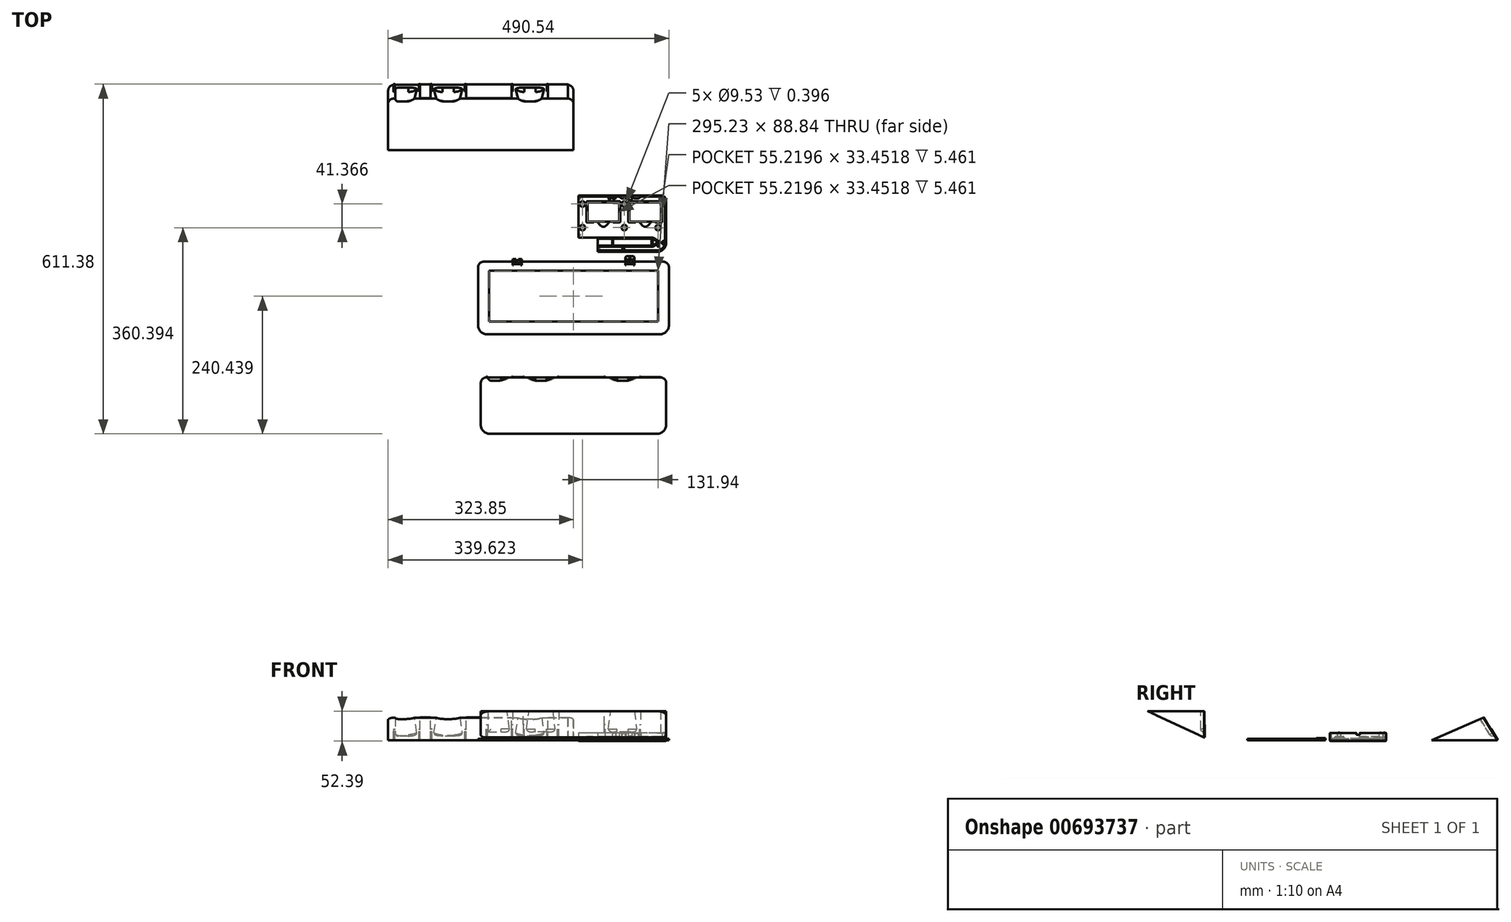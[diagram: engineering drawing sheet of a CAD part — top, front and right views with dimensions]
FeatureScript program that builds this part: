
annotation { "Feature Type Name" : "Feature", "Feature Type Description" : "" }
export const myFeature = defineFeature(function(context is Context, id is Id, definition is map)
    precondition{}
    {
        {
            var Q0;
            Q0=qCreatedBy(makeId("Top.planeOp"),FACE);
            var sketch = newSketch(context, id + "F0", { "sketchPlane" : qUnion([Q0])});
            skLineSegment(sketch, "E0.bottom", {"start": v(161.93, -49.21) * mm, "end": v(-161.93, -49.21) * mm});
            skLineSegment(sketch, "E0.top", {"start": v(161.93, 49.21) * mm, "end": v(-161.93, 49.21) * mm});
            skLineSegment(sketch, "E0.left", {"start": v(161.93, -49.21) * mm, "end": v(161.93, 49.21) * mm});
            skLineSegment(sketch, "E0.right", {"start": v(-161.93, -49.21) * mm, "end": v(-161.93, 49.21) * mm});
            skPoint(sketch, "E0.middle", {"position": v(0, 0) * mm});
            skSolve(sketch);
        }
        {
            var Q0;
            Q0=makeQuery(id+"F0.imprint","IMPRINT",FACE,{"disambiguationData":[TD([[makeQuery(id+"F0.imprint","IMPRINT",EDGE,{"derivedFrom":sQuery(id+"F0.wireOp",EDGE,"E0.bottom")}),-1.0]])]});
            extrude(context, id + "F1", {"entities" : qUnion([Q0]), "depth" : 3.17 * mm, "offsetDistance" : 25.4 * mm});
        }
        {
            var Q0;
            Q0=makeQuery(id+"F1.opExtrude","SWEPT_EDGE",EDGE,{"disambiguationData":[OSD([sQuery(id+"F0.wireOp",EDGE,"E0.bottom"),sQuery(id+"F0.wireOp",EDGE,"E0.right")])]});
            var Q1;
            Q1=makeQuery(id+"F1.opExtrude","SWEPT_EDGE",EDGE,{"disambiguationData":[OSD([sQuery(id+"F0.wireOp",EDGE,"E0.bottom"),sQuery(id+"F0.wireOp",EDGE,"E0.left")])]});
            fillet(context, id + "F2", {"entities" : qUnion([Q0, Q1]), "radius" : 15.88 * mm, "tangentPropagation" : true, "allowEdgeOverflow" : false});
        }
        {
            var Q0;
            Q0=makeQuery(id+"F1.opExtrude","SWEPT_EDGE",EDGE,{"disambiguationData":[OSD([sQuery(id+"F0.wireOp",EDGE,"E0.top"),sQuery(id+"F0.wireOp",EDGE,"E0.right")])]});
            var Q1;
            Q1=makeQuery(id+"F1.opExtrude","SWEPT_EDGE",EDGE,{"disambiguationData":[OSD([sQuery(id+"F0.wireOp",EDGE,"E0.top"),sQuery(id+"F0.wireOp",EDGE,"E0.left")])]});
            fillet(context, id + "F3", {"entities" : qUnion([Q0, Q1]), "radius" : 9.52 * mm, "tangentPropagation" : true, "allowEdgeOverflow" : false});
        }
        {
            var Q0;
            Q0=makeQuery(id+"F1.opExtrude","CAP_FACE",FACE,{"disambiguationData":[OSD([sQuery(id+"F0.wireOp",EDGE,"E0.bottom"),sQuery(id+"F0.wireOp",EDGE,"E0.top"),sQuery(id+"F0.wireOp",EDGE,"E0.left"),sQuery(id+"F0.wireOp",EDGE,"E0.right")])],"isStart":false});
            var sketch = newSketch(context, id + "F4", { "sketchPlane" : qUnion([Q0])});
            skArc(sketch, "E1.0", {"start": v(-152.4, 46.93) * mm, "mid": v(-157.52, 44.8) * mm, "end": v(-159.64, 39.69) * mm});
            skArc(sketch, "E2.0", {"start": v(-159.64, -33.34) * mm, "mid": v(-155.66, -42.95) * mm, "end": v(-146.05, -46.93) * mm});
            skLineSegment(sketch, "E3.0", {"start": v(-159.64, -33.34) * mm, "end": v(-159.64, 39.69) * mm});
            skArc(sketch, "E4.0", {"start": v(146.05, -46.93) * mm, "mid": v(155.66, -42.95) * mm, "end": v(159.64, -33.34) * mm});
            skArc(sketch, "E5.0", {"start": v(159.64, 39.69) * mm, "mid": v(157.52, 44.8) * mm, "end": v(152.4, 46.93) * mm});
            skLineSegment(sketch, "E6.0", {"start": v(159.64, -33.34) * mm, "end": v(159.64, 39.69) * mm});
            skLineSegment(sketch, "E7.0", {"start": v(152.4, 46.93) * mm, "end": v(-152.4, 46.93) * mm});
            skLineSegment(sketch, "E8.0", {"start": v(146.05, -46.93) * mm, "end": v(-146.05, -46.93) * mm});
            skSolve(sketch);
        }
        {
            var Q0;
            Q0=makeQuery(id+"F4.imprint","IMPRINT",FACE,{"disambiguationData":[TD([[makeQuery(id+"F4.imprint","IMPRINT",EDGE,{"derivedFrom":sQuery(id+"F4.wireOp",EDGE,"E1.0")}),-1.0]])]});
            extrude(context, id + "F5", {"entities" : qUnion([Q0]), "operationType" : NewBodyOperationType.ADD, "depth" : 9.52 * mm, "offsetDistance" : 25.4 * mm});
        }
        {
            var Q0;
            Q0=makeQuery(id+"F1.opExtrude","CAP_FACE",FACE,{"disambiguationData":[OSD([sQuery(id+"F0.wireOp",EDGE,"E0.bottom"),sQuery(id+"F0.wireOp",EDGE,"E0.top"),sQuery(id+"F0.wireOp",EDGE,"E0.left"),sQuery(id+"F0.wireOp",EDGE,"E0.right")])],"isStart":false});
            var sketch = newSketch(context, id + "F6", { "sketchPlane" : qUnion([Q0])});
            skCircle(sketch, "E9", {"center": v(-158.52, -33.34) * mm, "radius": 3.18 * mm});
            skLineSegment(sketch, "E10", {"start": v(-158.52, -33.34) * mm, "end": v(-158.52, 39.69) * mm, "construction": true});
            skCircle(sketch, "E11", {"center": v(-158.52, 39.69) * mm, "radius": 3.18 * mm});
            skCircle(sketch, "E12", {"center": v(158.23, 39.4) * mm, "radius": 3.18 * mm});
            skCircle(sketch, "E13", {"center": v(157.67, -33.34) * mm, "radius": 3.18 * mm});
            skCircle(sketch, "E14", {"center": v(70.74, 45.8) * mm, "radius": 3.18 * mm});
            skCircle(sketch, "E15", {"center": v(-2.29, 45.8) * mm, "radius": 3.29 * mm});
            skCircle(sketch, "E16", {"center": v(31.57, -45.8) * mm, "radius": 3.18 * mm});
            skCircle(sketch, "E17", {"center": v(-68.96, -45.8) * mm, "radius": 3.18 * mm});
            skSolve(sketch);
        }
        {
            var Q0;
            {var subQ0=sQuery(id+"F6.wireOp",EDGE,"E9");var subQ1=makeQuery(id+"F5.opExtrude","CAP_EDGE",EDGE,{"disambiguationData":[OSD([sQuery(id+"F4.wireOp",EDGE,"E2.0")])],"isStart":true});var subQ2=makeQuery(id+"F6.imprint","INTERSECT",VERTEX,{"derivedFrom":[subQ1,subQ0]});Q0=makeQuery(id+"F6.imprint","IMPRINT",FACE,{"disambiguationData":[TD([[makeQuery(id+"F6.imprint","IMPRINT",EDGE,{"disambiguationData":[TD([[subQ2,-1.0]])],"derivedFrom":subQ0}),1.0]])]});}
            var Q1;
            {var subQ0=sQuery(id+"F6.wireOp",EDGE,"E11");var subQ1=makeQuery(id+"F5.opExtrude","CAP_EDGE",EDGE,{"disambiguationData":[OSD([sQuery(id+"F4.wireOp",EDGE,"E1.0")])],"isStart":true});var subQ2=makeQuery(id+"F6.imprint","INTERSECT",VERTEX,{"derivedFrom":[subQ1,subQ0]});Q1=makeQuery(id+"F6.imprint","IMPRINT",FACE,{"disambiguationData":[TD([[makeQuery(id+"F6.imprint","IMPRINT",EDGE,{"disambiguationData":[TD([[subQ2,1.0]])],"derivedFrom":subQ0}),1.0]])]});}
            var Q2;
            {var subQ0=sQuery(id+"F6.wireOp",EDGE,"E15");var subQ1=makeQuery(id+"F5.opExtrude","CAP_EDGE",EDGE,{"disambiguationData":[OSD([sQuery(id+"F4.wireOp",EDGE,"E7.0")])],"isStart":true});var subQ2=makeQuery(id+"F6.imprint","INTERSECT",VERTEX,{"disambiguationData":[OD(0.0)],"derivedFrom":[subQ1,subQ0]});Q2=makeQuery(id+"F6.imprint","IMPRINT",FACE,{"disambiguationData":[TD([[makeQuery(id+"F6.imprint","IMPRINT",EDGE,{"disambiguationData":[TD([[subQ2,-1.0]])],"derivedFrom":subQ0}),1.0]])]});}
            var Q3;
            {var subQ0=sQuery(id+"F6.wireOp",EDGE,"E14");var subQ1=makeQuery(id+"F5.opExtrude","CAP_EDGE",EDGE,{"disambiguationData":[OSD([sQuery(id+"F4.wireOp",EDGE,"E7.0")])],"isStart":true});var subQ2=makeQuery(id+"F6.imprint","INTERSECT",VERTEX,{"disambiguationData":[OD(0.0)],"derivedFrom":[subQ1,subQ0]});Q3=makeQuery(id+"F6.imprint","IMPRINT",FACE,{"disambiguationData":[TD([[makeQuery(id+"F6.imprint","IMPRINT",EDGE,{"disambiguationData":[TD([[subQ2,1.0]])],"derivedFrom":subQ0}),1.0]])]});}
            var Q4;
            {var subQ0=sQuery(id+"F6.wireOp",EDGE,"E17");var subQ1=makeQuery(id+"F5.opExtrude","CAP_EDGE",EDGE,{"disambiguationData":[OSD([sQuery(id+"F4.wireOp",EDGE,"E8.0")])],"isStart":true});var subQ2=makeQuery(id+"F6.imprint","INTERSECT",VERTEX,{"disambiguationData":[OD(0.0)],"derivedFrom":[subQ1,subQ0]});Q4=makeQuery(id+"F6.imprint","IMPRINT",FACE,{"disambiguationData":[TD([[makeQuery(id+"F6.imprint","IMPRINT",EDGE,{"disambiguationData":[TD([[subQ2,1.0]])],"derivedFrom":subQ0}),1.0]])]});}
            var Q5;
            {var subQ0=sQuery(id+"F6.wireOp",EDGE,"E16");var subQ1=makeQuery(id+"F5.opExtrude","CAP_EDGE",EDGE,{"disambiguationData":[OSD([sQuery(id+"F4.wireOp",EDGE,"E8.0")])],"isStart":true});var subQ2=makeQuery(id+"F6.imprint","INTERSECT",VERTEX,{"disambiguationData":[OD(0.0)],"derivedFrom":[subQ1,subQ0]});Q5=makeQuery(id+"F6.imprint","IMPRINT",FACE,{"disambiguationData":[TD([[makeQuery(id+"F6.imprint","IMPRINT",EDGE,{"disambiguationData":[TD([[subQ2,-1.0]])],"derivedFrom":subQ0}),1.0]])]});}
            var Q6;
            {var subQ0=sQuery(id+"F6.wireOp",EDGE,"E13");var subQ1=makeQuery(id+"F5.opExtrude","CAP_EDGE",EDGE,{"disambiguationData":[OSD([sQuery(id+"F4.wireOp",EDGE,"E4.0")])],"isStart":true});var subQ2=makeQuery(id+"F6.imprint","INTERSECT",VERTEX,{"derivedFrom":[subQ1,subQ0]});Q6=makeQuery(id+"F6.imprint","IMPRINT",FACE,{"disambiguationData":[TD([[makeQuery(id+"F6.imprint","IMPRINT",EDGE,{"disambiguationData":[TD([[subQ2,1.0]])],"derivedFrom":subQ0}),1.0]])]});}
            var Q7;
            {var subQ0=sQuery(id+"F6.wireOp",EDGE,"E12");var subQ1=makeQuery(id+"F5.opExtrude","CAP_EDGE",EDGE,{"disambiguationData":[OSD([sQuery(id+"F4.wireOp",EDGE,"E5.0")])],"isStart":true});var subQ2=makeQuery(id+"F6.imprint","INTERSECT",VERTEX,{"derivedFrom":[subQ1,subQ0]});Q7=makeQuery(id+"F6.imprint","IMPRINT",FACE,{"disambiguationData":[TD([[makeQuery(id+"F6.imprint","IMPRINT",EDGE,{"disambiguationData":[TD([[subQ2,-1.0]])],"derivedFrom":subQ0}),1.0]])]});}
            extrude(context, id + "F7", {"entities" : qUnion([Q0, Q1, Q2, Q3, Q4, Q5, Q6, Q7]), "operationType" : NewBodyOperationType.ADD, "depth" : 9.52 * mm, "offsetDistance" : 25.4 * mm});
        }
        {
            var Q0;
            {var subQ0=sQuery(id+"F4.wireOp",EDGE,"E8.0");var subQ1=sQuery(id+"F4.wireOp",EDGE,"E7.0");var subQ2=sQuery(id+"F4.wireOp",EDGE,"E6.0");var subQ3=sQuery(id+"F4.wireOp",EDGE,"E4.0");var subQ4=sQuery(id+"F4.wireOp",EDGE,"E5.0");var subQ5=sQuery(id+"F4.wireOp",EDGE,"E3.0");var subQ6=sQuery(id+"F4.wireOp",EDGE,"E1.0");var subQ7=sQuery(id+"F4.wireOp",EDGE,"E2.0");Q0=makeQuery(id+"F7.boolean.opBoolean","MERGE",FACE,{"derivedFrom":[makeQuery(id+"F5.opExtrude","CAP_FACE",FACE,{"disambiguationData":[OSD([sQuery(id+"F0.wireOp",EDGE,"E0.bottom"),sQuery(id+"F0.wireOp",EDGE,"E0.top"),sQuery(id+"F0.wireOp",EDGE,"E0.left"),sQuery(id+"F0.wireOp",EDGE,"E0.right"),subQ6,subQ7,subQ5,subQ3,subQ4,subQ2,subQ1,subQ0])],"isStart":false}),makeQuery(id+"F7.opExtrude","CAP_FACE",FACE,{"disambiguationData":[OSD([subQ7,subQ5,sQuery(id+"F6.wireOp",EDGE,"E9")])],"isStart":false}),makeQuery(id+"F7.opExtrude","CAP_FACE",FACE,{"disambiguationData":[OSD([subQ6,subQ5,sQuery(id+"F6.wireOp",EDGE,"E11")])],"isStart":false}),makeQuery(id+"F7.opExtrude","CAP_FACE",FACE,{"disambiguationData":[OSD([subQ4,subQ2,sQuery(id+"F6.wireOp",EDGE,"E12")])],"isStart":false}),makeQuery(id+"F7.opExtrude","CAP_FACE",FACE,{"disambiguationData":[OSD([subQ3,subQ2,sQuery(id+"F6.wireOp",EDGE,"E13")])],"isStart":false}),makeQuery(id+"F7.opExtrude","CAP_FACE",FACE,{"disambiguationData":[OSD([subQ1,sQuery(id+"F6.wireOp",EDGE,"E14")])],"isStart":false}),makeQuery(id+"F7.opExtrude","CAP_FACE",FACE,{"disambiguationData":[OSD([subQ1,sQuery(id+"F6.wireOp",EDGE,"E15")])],"isStart":false}),makeQuery(id+"F7.opExtrude","CAP_FACE",FACE,{"disambiguationData":[OSD([subQ0,sQuery(id+"F6.wireOp",EDGE,"E16")])],"isStart":false}),makeQuery(id+"F7.opExtrude","CAP_FACE",FACE,{"disambiguationData":[OSD([subQ0,sQuery(id+"F6.wireOp",EDGE,"E17")])],"isStart":false})]});}
            var sketch = newSketch(context, id + "F8", { "sketchPlane" : qUnion([Q0])});
            skCircle(sketch, "E18", {"center": v(-2.29, 45.8) * mm, "radius": 1.03 * mm});
            skCircle(sketch, "E19", {"center": v(70.74, 45.8) * mm, "radius": 1.03 * mm});
            skCircle(sketch, "E20", {"center": v(158.23, 39.4) * mm, "radius": 1.03 * mm});
            skCircle(sketch, "E21", {"center": v(157.67, -33.34) * mm, "radius": 1.03 * mm});
            skCircle(sketch, "E22", {"center": v(31.57, -45.8) * mm, "radius": 1.03 * mm});
            skCircle(sketch, "E23", {"center": v(-68.96, -45.8) * mm, "radius": 1.03 * mm});
            skCircle(sketch, "E24", {"center": v(-158.52, -33.34) * mm, "radius": 1.03 * mm});
            skCircle(sketch, "E25", {"center": v(-158.52, 39.69) * mm, "radius": 1.03 * mm});
            skSolve(sketch);
        }
        {
            var Q0;
            Q0=makeQuery(id+"F8.imprint","IMPRINT",FACE,{"disambiguationData":[TD([[makeQuery(id+"F8.imprint","IMPRINT",EDGE,{"derivedFrom":sQuery(id+"F8.wireOp",EDGE,"E24")}),1.0]])]});
            var Q1;
            Q1=makeQuery(id+"F8.imprint","IMPRINT",FACE,{"disambiguationData":[TD([[makeQuery(id+"F8.imprint","IMPRINT",EDGE,{"derivedFrom":sQuery(id+"F8.wireOp",EDGE,"E23")}),1.0]])]});
            var Q2;
            Q2=makeQuery(id+"F8.imprint","IMPRINT",FACE,{"disambiguationData":[TD([[makeQuery(id+"F8.imprint","IMPRINT",EDGE,{"derivedFrom":sQuery(id+"F8.wireOp",EDGE,"E22")}),1.0]])]});
            var Q3;
            Q3=makeQuery(id+"F8.imprint","IMPRINT",FACE,{"disambiguationData":[TD([[makeQuery(id+"F8.imprint","IMPRINT",EDGE,{"derivedFrom":sQuery(id+"F8.wireOp",EDGE,"E21")}),1.0]])]});
            var Q4;
            Q4=makeQuery(id+"F8.imprint","IMPRINT",FACE,{"disambiguationData":[TD([[makeQuery(id+"F8.imprint","IMPRINT",EDGE,{"derivedFrom":sQuery(id+"F8.wireOp",EDGE,"E20")}),1.0]])]});
            var Q5;
            Q5=makeQuery(id+"F8.imprint","IMPRINT",FACE,{"disambiguationData":[TD([[makeQuery(id+"F8.imprint","IMPRINT",EDGE,{"derivedFrom":sQuery(id+"F8.wireOp",EDGE,"E19")}),1.0]])]});
            var Q6;
            Q6=makeQuery(id+"F8.imprint","IMPRINT",FACE,{"disambiguationData":[TD([[makeQuery(id+"F8.imprint","IMPRINT",EDGE,{"derivedFrom":sQuery(id+"F8.wireOp",EDGE,"E18")}),1.0]])]});
            var Q7;
            Q7=makeQuery(id+"F8.imprint","IMPRINT",FACE,{"disambiguationData":[TD([[makeQuery(id+"F8.imprint","IMPRINT",EDGE,{"derivedFrom":sQuery(id+"F8.wireOp",EDGE,"E25")}),1.0]])]});
            extrude(context, id + "F9", {"entities" : qUnion([Q0, Q1, Q2, Q3, Q4, Q5, Q6, Q7]), "operationType" : NewBodyOperationType.ADD, "depth" : 0.79 * mm, "offsetDistance" : 25.4 * mm});
        }
        {
            var Q0;
            Q0=makeQuery(id+"F1.opExtrude","CAP_FACE",FACE,{"disambiguationData":[OSD([sQuery(id+"F0.wireOp",EDGE,"E0.bottom"),sQuery(id+"F0.wireOp",EDGE,"E0.top"),sQuery(id+"F0.wireOp",EDGE,"E0.left"),sQuery(id+"F0.wireOp",EDGE,"E0.right")])],"isStart":false});
            var sketch = newSketch(context, id + "F10", { "sketchPlane" : qUnion([Q0])});
            skLineSegment(sketch, "E26", {"start": v(80.06, 46.93) * mm, "end": v(83.88, 43.75) * mm});
            skLineSegment(sketch, "E27", {"start": v(83.88, 43.75) * mm, "end": v(92.11, 43.75) * mm});
            skLineSegment(sketch, "E28", {"start": v(92.11, 43.75) * mm, "end": v(95.94, 46.93) * mm});
            skLineSegment(sketch, "E29", {"start": v(95.94, 46.93) * mm, "end": v(80.06, 46.93) * mm});
            skLineSegment(sketch, "E30", {"start": v(88, 46.93) * mm, "end": v(88, 43.23) * mm, "construction": true});
            skLineSegment(sketch, "E31", {"start": v(88, 43.75) * mm, "end": v(88, 44.46) * mm, "construction": true});
            skLineSegment(sketch, "E32", {"start": v(83.88, 45.62) * mm, "end": v(83.88, 43.16) * mm, "construction": true});
            skLineSegment(sketch, "E33", {"start": v(92.11, 45.79) * mm, "end": v(92.11, 43.52) * mm, "construction": true});
            skLineSegment(sketch, "E34", {"start": v(102.29, 46.93) * mm, "end": v(106.04, 43.75) * mm});
            skLineSegment(sketch, "E35", {"start": v(106.04, 43.75) * mm, "end": v(114.27, 43.75) * mm});
            skLineSegment(sketch, "E36", {"start": v(114.27, 43.75) * mm, "end": v(118.03, 46.93) * mm});
            skLineSegment(sketch, "E37", {"start": v(118.03, 46.93) * mm, "end": v(102.29, 46.93) * mm});
            skLineSegment(sketch, "E38", {"start": v(110.16, 46.93) * mm, "end": v(110.16, 43.75) * mm, "construction": true});
            skLineSegment(sketch, "E39", {"start": v(106.04, 45.04) * mm, "end": v(106.04, 42.78) * mm, "construction": true});
            skLineSegment(sketch, "E40", {"start": v(114.27, 44.82) * mm, "end": v(114.27, 43.03) * mm, "construction": true});
            skLineSegment(sketch, "E41", {"start": v(102.29, 47.44) * mm, "end": v(102.29, 46.4) * mm, "construction": true});
            skLineSegment(sketch, "E42", {"start": v(-67.48, 46.93) * mm, "end": v(-63.72, 43.75) * mm});
            skLineSegment(sketch, "E43", {"start": v(-63.72, 43.75) * mm, "end": v(-55.5, 43.75) * mm});
            skLineSegment(sketch, "E44", {"start": v(-55.5, 43.75) * mm, "end": v(-51.73, 46.93) * mm});
            skLineSegment(sketch, "E45", {"start": v(-51.73, 46.93) * mm, "end": v(-67.48, 46.93) * mm});
            skLineSegment(sketch, "E46", {"start": v(-59.6, 46.93) * mm, "end": v(-59.6, 41.87) * mm, "construction": true});
            skPoint(sketch, "E46.startSnap0", {"position": v(-59.6, 43.75) * mm});
            skLineSegment(sketch, "E47", {"start": v(-144.62, 46.93) * mm, "end": v(-140.86, 43.75) * mm});
            skLineSegment(sketch, "E48", {"start": v(-140.86, 43.75) * mm, "end": v(-132.63, 43.75) * mm});
            skLineSegment(sketch, "E49", {"start": v(-132.63, 43.75) * mm, "end": v(-128.87, 46.93) * mm});
            skLineSegment(sketch, "E50", {"start": v(-128.87, 46.93) * mm, "end": v(-144.62, 46.93) * mm});
            skLineSegment(sketch, "E51", {"start": v(-136.74, 46.93) * mm, "end": v(-136.74, 41.02) * mm, "construction": true});
            skSolve(sketch);
        }
        {
            var Q0;
            Q0=makeQuery(id+"F10.imprint","IMPRINT",FACE,{"disambiguationData":[TD([[makeQuery(id+"F10.imprint","IMPRINT",EDGE,{"derivedFrom":sQuery(id+"F10.wireOp",EDGE,"E47")}),1.0]])]});
            var Q1;
            Q1=makeQuery(id+"F10.imprint","IMPRINT",FACE,{"disambiguationData":[TD([[makeQuery(id+"F10.imprint","IMPRINT",EDGE,{"derivedFrom":sQuery(id+"F10.wireOp",EDGE,"E42")}),1.0]])]});
            var Q2;
            Q2=makeQuery(id+"F10.imprint","IMPRINT",FACE,{"disambiguationData":[TD([[makeQuery(id+"F10.imprint","IMPRINT",EDGE,{"derivedFrom":sQuery(id+"F10.wireOp",EDGE,"E26")}),1.0]])]});
            var Q3;
            Q3=makeQuery(id+"F10.imprint","IMPRINT",FACE,{"disambiguationData":[TD([[makeQuery(id+"F10.imprint","IMPRINT",EDGE,{"derivedFrom":sQuery(id+"F10.wireOp",EDGE,"E34")}),1.0]])]});
            extrude(context, id + "F11", {"entities" : qUnion([Q0, Q1, Q2, Q3]), "operationType" : NewBodyOperationType.ADD, "depth" : 9.52 * mm, "offsetDistance" : 25.4 * mm});
        }
        {
            var Q0;
            {var subQ0=sQuery(id+"F4.wireOp",EDGE,"E8.0");var subQ1=makeQuery(id+"F7.opExtrude","CAP_FACE",FACE,{"disambiguationData":[OSD([subQ0,sQuery(id+"F6.wireOp",EDGE,"E17")])],"isStart":false});var subQ2=makeQuery(id+"F7.opExtrude","CAP_FACE",FACE,{"disambiguationData":[OSD([subQ0,sQuery(id+"F6.wireOp",EDGE,"E16")])],"isStart":false});var subQ3=sQuery(id+"F4.wireOp",EDGE,"E7.0");var subQ4=makeQuery(id+"F7.opExtrude","CAP_FACE",FACE,{"disambiguationData":[OSD([subQ3,sQuery(id+"F6.wireOp",EDGE,"E15")])],"isStart":false});var subQ5=sQuery(id+"F6.wireOp",EDGE,"E14");var subQ6=makeQuery(id+"F7.opExtrude","CAP_FACE",FACE,{"disambiguationData":[OSD([subQ3,subQ5])],"isStart":false});var subQ7=sQuery(id+"F4.wireOp",EDGE,"E6.0");var subQ8=sQuery(id+"F4.wireOp",EDGE,"E4.0");var subQ9=makeQuery(id+"F7.opExtrude","CAP_FACE",FACE,{"disambiguationData":[OSD([subQ8,subQ7,sQuery(id+"F6.wireOp",EDGE,"E13")])],"isStart":false});var subQ11=sQuery(id+"F0.wireOp",EDGE,"E0.right");var subQ12=sQuery(id+"F0.wireOp",EDGE,"E0.left");var subQ13=sQuery(id+"F0.wireOp",EDGE,"E0.top");var subQ14=sQuery(id+"F0.wireOp",EDGE,"E0.bottom");var subQ15=makeQuery(id+"F1.opExtrude","CAP_FACE",FACE,{"disambiguationData":[OSD([subQ14,subQ13,subQ12,subQ11])],"isStart":false});var subQ16=sQuery(id+"F4.wireOp",EDGE,"E5.0");var subQ17=makeQuery(id+"F7.opExtrude","CAP_FACE",FACE,{"disambiguationData":[OSD([subQ16,subQ7,sQuery(id+"F6.wireOp",EDGE,"E12")])],"isStart":false});var subQ18=sQuery(id+"F4.wireOp",EDGE,"E3.0");var subQ19=sQuery(id+"F4.wireOp",EDGE,"E2.0");var subQ20=sQuery(id+"F4.wireOp",EDGE,"E1.0");var subQ21=makeQuery(id+"F5.opExtrude","CAP_FACE",FACE,{"disambiguationData":[OSD([subQ14,subQ13,subQ12,subQ11,subQ20,subQ19,subQ18,subQ8,subQ16,subQ7,subQ3,subQ0])],"isStart":false});var subQ22=makeQuery(id+"F7.opExtrude","CAP_FACE",FACE,{"disambiguationData":[OSD([subQ19,subQ18,sQuery(id+"F6.wireOp",EDGE,"E9")])],"isStart":false});var subQ23=makeQuery(id+"F7.opExtrude","CAP_FACE",FACE,{"disambiguationData":[OSD([subQ20,subQ18,sQuery(id+"F6.wireOp",EDGE,"E11")])],"isStart":false});var subQ24=sQuery(id+"F10.wireOp",EDGE,"E28");Q0=makeQuery(id+"F11.boolean.opBoolean","SPLIT",FACE,{"disambiguationData":[TD([makeQuery(id+"F11.opExtrude","SWEPT_FACE",FACE,{"disambiguationData":[OSD([subQ24])]})])],"derivedFrom":makeQuery(id+"F7.boolean.opBoolean","SPLIT",FACE,{"disambiguationData":[TD([subQ15,subQ21,makeQuery(id+"F5.opExtrude","SWEPT_FACE",FACE,{"disambiguationData":[OSD([subQ16])]}),subQ22,subQ23,subQ17,subQ9,makeQuery(id+"F7.opExtrude","SWEPT_FACE",FACE,{"disambiguationData":[OSD([subQ5])]}),subQ6,subQ4,subQ2,subQ1])],"derivedFrom":makeQuery(id+"F5.opExtrude","SWEPT_FACE",FACE,{"disambiguationData":[OSD([subQ3])]})})});}
            var sketch = newSketch(context, id + "F12", { "sketchPlane" : qUnion([Q0])});
            skCircle(sketch, "E52", {"center": v(-148.66, 3.04) * mm, "radius": 3.18 * mm});
            skCircle(sketch, "E53", {"center": v(99.9, 3.18) * mm, "radius": 3.18 * mm});
            skSolve(sketch);
        }
        {
            var Q0;
            Q0=makeQuery(id+"F12.imprint","IMPRINT",FACE,{"disambiguationData":[TD([[makeQuery(id+"F12.imprint","IMPRINT",EDGE,{"derivedFrom":sQuery(id+"F12.wireOp",EDGE,"E52")}),1.0]])]});
            extrude(context, id + "F13", {"entities" : qUnion([Q0]), "operationType" : NewBodyOperationType.ADD, "depth" : 6.35 * mm, "offsetDistance" : 25.4 * mm});
        }
        {
            var Q0;
            {var subQ0=sQuery(id+"F12.wireOp",EDGE,"E52");Q0=makeQuery(id+"F13.boolean.opBoolean","SPLIT",EDGE,{"disambiguationData":[TD([makeQuery(id+"F1.opExtrude","CAP_FACE",FACE,{"disambiguationData":[OSD([sQuery(id+"F0.wireOp",EDGE,"E0.bottom"),sQuery(id+"F0.wireOp",EDGE,"E0.top"),sQuery(id+"F0.wireOp",EDGE,"E0.left"),sQuery(id+"F0.wireOp",EDGE,"E0.right")])],"isStart":false})])],"derivedFrom":makeQuery(id+"F13.opExtrude","CAP_EDGE",EDGE,{"disambiguationData":[OSD([subQ0])],"isStart":false})});}
            fillet(context, id + "F14", {"entities" : qUnion([Q0]), "radius" : 2.54 * mm, "tangentPropagation" : true, "allowEdgeOverflow" : false});
        }
        {
            var Q0;
            {var subQ0=sQuery(id+"F4.wireOp",EDGE,"E8.0");var subQ1=makeQuery(id+"F7.opExtrude","CAP_FACE",FACE,{"disambiguationData":[OSD([subQ0,sQuery(id+"F6.wireOp",EDGE,"E17")])],"isStart":false});var subQ2=makeQuery(id+"F7.opExtrude","CAP_FACE",FACE,{"disambiguationData":[OSD([subQ0,sQuery(id+"F6.wireOp",EDGE,"E16")])],"isStart":false});var subQ3=sQuery(id+"F4.wireOp",EDGE,"E7.0");var subQ4=makeQuery(id+"F7.opExtrude","CAP_FACE",FACE,{"disambiguationData":[OSD([subQ3,sQuery(id+"F6.wireOp",EDGE,"E15")])],"isStart":false});var subQ5=sQuery(id+"F6.wireOp",EDGE,"E14");var subQ6=makeQuery(id+"F7.opExtrude","CAP_FACE",FACE,{"disambiguationData":[OSD([subQ3,subQ5])],"isStart":false});var subQ7=sQuery(id+"F4.wireOp",EDGE,"E6.0");var subQ8=sQuery(id+"F4.wireOp",EDGE,"E4.0");var subQ9=makeQuery(id+"F7.opExtrude","CAP_FACE",FACE,{"disambiguationData":[OSD([subQ8,subQ7,sQuery(id+"F6.wireOp",EDGE,"E13")])],"isStart":false});var subQ11=sQuery(id+"F0.wireOp",EDGE,"E0.right");var subQ12=sQuery(id+"F0.wireOp",EDGE,"E0.left");var subQ13=sQuery(id+"F0.wireOp",EDGE,"E0.top");var subQ14=sQuery(id+"F0.wireOp",EDGE,"E0.bottom");var subQ15=makeQuery(id+"F1.opExtrude","CAP_FACE",FACE,{"disambiguationData":[OSD([subQ14,subQ13,subQ12,subQ11])],"isStart":false});var subQ16=sQuery(id+"F4.wireOp",EDGE,"E5.0");var subQ17=makeQuery(id+"F7.opExtrude","CAP_FACE",FACE,{"disambiguationData":[OSD([subQ16,subQ7,sQuery(id+"F6.wireOp",EDGE,"E12")])],"isStart":false});var subQ18=sQuery(id+"F4.wireOp",EDGE,"E3.0");var subQ19=sQuery(id+"F4.wireOp",EDGE,"E2.0");var subQ20=sQuery(id+"F4.wireOp",EDGE,"E1.0");var subQ21=makeQuery(id+"F5.opExtrude","CAP_FACE",FACE,{"disambiguationData":[OSD([subQ14,subQ13,subQ12,subQ11,subQ20,subQ19,subQ18,subQ8,subQ16,subQ7,subQ3,subQ0])],"isStart":false});var subQ22=makeQuery(id+"F7.opExtrude","CAP_FACE",FACE,{"disambiguationData":[OSD([subQ19,subQ18,sQuery(id+"F6.wireOp",EDGE,"E9")])],"isStart":false});var subQ23=makeQuery(id+"F7.opExtrude","CAP_FACE",FACE,{"disambiguationData":[OSD([subQ20,subQ18,sQuery(id+"F6.wireOp",EDGE,"E11")])],"isStart":false});var subQ24=sQuery(id+"F10.wireOp",EDGE,"E28");Q0=makeQuery(id+"F11.boolean.opBoolean","SPLIT",FACE,{"disambiguationData":[TD([makeQuery(id+"F11.opExtrude","SWEPT_FACE",FACE,{"disambiguationData":[OSD([subQ24])]})])],"derivedFrom":makeQuery(id+"F7.boolean.opBoolean","SPLIT",FACE,{"disambiguationData":[TD([subQ15,subQ21,makeQuery(id+"F5.opExtrude","SWEPT_FACE",FACE,{"disambiguationData":[OSD([subQ16])]}),subQ22,subQ23,subQ17,subQ9,makeQuery(id+"F7.opExtrude","SWEPT_FACE",FACE,{"disambiguationData":[OSD([subQ5])]}),subQ6,subQ4,subQ2,subQ1])],"derivedFrom":makeQuery(id+"F5.opExtrude","SWEPT_FACE",FACE,{"disambiguationData":[OSD([subQ3])]})})});}
            var sketch = newSketch(context, id + "F15", { "sketchPlane" : qUnion([Q0])});
            skCircle(sketch, "E54", {"center": v(99.11, 3.18) * mm, "radius": 2.92 * mm});
            skSolve(sketch);
        }
        {
            var Q0;
            {var subQ0=sQuery(id+"F15.wireOp",EDGE,"E54");var subQ1=makeQuery(id+"F1.opExtrude","CAP_FACE",FACE,{"disambiguationData":[OSD([sQuery(id+"F0.wireOp",EDGE,"E0.bottom"),sQuery(id+"F0.wireOp",EDGE,"E0.top"),sQuery(id+"F0.wireOp",EDGE,"E0.left"),sQuery(id+"F0.wireOp",EDGE,"E0.right")])],"isStart":false});var subQ2=sQuery(id+"F4.wireOp",EDGE,"E7.0");var subQ3=makeQuery(id+"F5.opExtrude","SWEPT_FACE",FACE,{"disambiguationData":[OSD([subQ2])]});var subQ4=makeQuery(id+"F11.boolean.opBoolean","SPLIT",EDGE,{"disambiguationData":[TD([makeQuery(id+"F11.opExtrude","SWEPT_FACE",FACE,{"disambiguationData":[OSD([sQuery(id+"F10.wireOp",EDGE,"E28")])]})])],"derivedFrom":makeQuery(id+"F7.boolean.opBoolean","SPLIT",EDGE,{"disambiguationData":[TD([subQ1,makeQuery(id+"F5.opExtrude","SWEPT_FACE",FACE,{"disambiguationData":[OSD([sQuery(id+"F4.wireOp",EDGE,"E5.0")])]}),subQ3,makeQuery(id+"F7.opExtrude","SWEPT_FACE",FACE,{"disambiguationData":[OSD([sQuery(id+"F6.wireOp",EDGE,"E14")])]})])],"derivedFrom":makeQuery(id+"F5.opExtrude","CAP_EDGE",EDGE,{"disambiguationData":[OSD([subQ2])],"isStart":true})})});var subQ5=makeQuery(id+"F15.imprint","INTERSECT",VERTEX,{"disambiguationData":[OD(0.0)],"derivedFrom":[subQ4,subQ0]});Q0=makeQuery(id+"F15.imprint","IMPRINT",FACE,{"disambiguationData":[TD([[makeQuery(id+"F15.imprint","IMPRINT",EDGE,{"disambiguationData":[TD([[subQ5,1.0]])],"derivedFrom":subQ0}),1.0]])]});}
            var Q1;
            Q1=sQuery(id+"F15.wireOp",EDGE,"E54");
            extrude(context, id + "F16", {"entities" : qUnion([Q0]), "operationType" : NewBodyOperationType.ADD, "surfaceEntities" : qUnion([Q1]), "depth" : 6.35 * mm, "offsetDistance" : 25.4 * mm});
        }
        {
            var Q0;
            Q0=makeQuery(id+"F16.opExtrude","CAP_EDGE",EDGE,{"disambiguationData":[OSD([sQuery(id+"F15.wireOp",EDGE,"E54")])],"isStart":false});
            fillet(context, id + "F17", {"entities" : qUnion([Q0]), "radius" : 2.54 * mm, "tangentPropagation" : true, "allowEdgeOverflow" : false});
        }
        {
            var Q0;
            {var subQ0=sQuery(id+"F4.wireOp",EDGE,"E8.0");var subQ1=makeQuery(id+"F7.opExtrude","CAP_FACE",FACE,{"disambiguationData":[OSD([subQ0,sQuery(id+"F6.wireOp",EDGE,"E16")])],"isStart":false});var subQ2=sQuery(id+"F6.wireOp",EDGE,"E15");var subQ3=sQuery(id+"F4.wireOp",EDGE,"E7.0");var subQ4=makeQuery(id+"F7.opExtrude","CAP_FACE",FACE,{"disambiguationData":[OSD([subQ3,subQ2])],"isStart":false});var subQ6=makeQuery(id+"F7.opExtrude","SWEPT_FACE",FACE,{"disambiguationData":[OSD([subQ2])]});var subQ7=makeQuery(id+"F7.opExtrude","CAP_FACE",FACE,{"disambiguationData":[OSD([subQ3,sQuery(id+"F6.wireOp",EDGE,"E14")])],"isStart":false});var subQ8=sQuery(id+"F4.wireOp",EDGE,"E6.0");var subQ9=sQuery(id+"F4.wireOp",EDGE,"E4.0");var subQ10=makeQuery(id+"F7.opExtrude","CAP_FACE",FACE,{"disambiguationData":[OSD([subQ9,subQ8,sQuery(id+"F6.wireOp",EDGE,"E13")])],"isStart":false});var subQ11=sQuery(id+"F0.wireOp",EDGE,"E0.right");var subQ12=sQuery(id+"F0.wireOp",EDGE,"E0.left");var subQ13=sQuery(id+"F0.wireOp",EDGE,"E0.top");var subQ14=sQuery(id+"F0.wireOp",EDGE,"E0.bottom");var subQ15=makeQuery(id+"F1.opExtrude","CAP_FACE",FACE,{"disambiguationData":[OSD([subQ14,subQ13,subQ12,subQ11])],"isStart":false});var subQ16=sQuery(id+"F4.wireOp",EDGE,"E5.0");var subQ17=makeQuery(id+"F7.opExtrude","CAP_FACE",FACE,{"disambiguationData":[OSD([subQ16,subQ8,sQuery(id+"F6.wireOp",EDGE,"E12")])],"isStart":false});var subQ18=sQuery(id+"F4.wireOp",EDGE,"E3.0");var subQ19=sQuery(id+"F4.wireOp",EDGE,"E2.0");var subQ20=sQuery(id+"F4.wireOp",EDGE,"E1.0");var subQ21=makeQuery(id+"F5.opExtrude","CAP_FACE",FACE,{"disambiguationData":[OSD([subQ14,subQ13,subQ12,subQ11,subQ20,subQ19,subQ18,subQ9,subQ16,subQ8,subQ3,subQ0])],"isStart":false});var subQ22=makeQuery(id+"F7.opExtrude","CAP_FACE",FACE,{"disambiguationData":[OSD([subQ19,subQ18,sQuery(id+"F6.wireOp",EDGE,"E9")])],"isStart":false});var subQ23=makeQuery(id+"F7.opExtrude","CAP_FACE",FACE,{"disambiguationData":[OSD([subQ20,subQ18,sQuery(id+"F6.wireOp",EDGE,"E11")])],"isStart":false});var subQ24=makeQuery(id+"F7.opExtrude","CAP_FACE",FACE,{"disambiguationData":[OSD([subQ0,sQuery(id+"F6.wireOp",EDGE,"E17")])],"isStart":false});Q0=makeQuery(id+"F11.boolean.opBoolean","SPLIT",FACE,{"disambiguationData":[TD([subQ6])],"derivedFrom":makeQuery(id+"F7.boolean.opBoolean","SPLIT",FACE,{"disambiguationData":[TD([subQ15,makeQuery(id+"F5.opExtrude","SWEPT_FACE",FACE,{"disambiguationData":[OSD([subQ20])]}),subQ21,subQ22,subQ23,subQ17,subQ10,subQ7,subQ6,subQ4,subQ1,subQ24])],"derivedFrom":makeQuery(id+"F5.opExtrude","SWEPT_FACE",FACE,{"disambiguationData":[OSD([subQ3])]})})});}
            var sketch = newSketch(context, id + "F18", { "sketchPlane" : qUnion([Q0])});
            skCircle(sketch, "E55", {"center": v(-47.86, 3.18) * mm, "radius": 3.18 * mm});
            skSolve(sketch);
        }
        {
            var Q0;
            {var subQ0=sQuery(id+"F18.wireOp",EDGE,"E55");var subQ1=makeQuery(id+"F1.opExtrude","CAP_FACE",FACE,{"disambiguationData":[OSD([sQuery(id+"F0.wireOp",EDGE,"E0.bottom"),sQuery(id+"F0.wireOp",EDGE,"E0.top"),sQuery(id+"F0.wireOp",EDGE,"E0.left"),sQuery(id+"F0.wireOp",EDGE,"E0.right")])],"isStart":false});var subQ2=sQuery(id+"F4.wireOp",EDGE,"E7.0");var subQ3=makeQuery(id+"F5.opExtrude","SWEPT_FACE",FACE,{"disambiguationData":[OSD([subQ2])]});var subQ4=makeQuery(id+"F7.opExtrude","SWEPT_FACE",FACE,{"disambiguationData":[OSD([sQuery(id+"F6.wireOp",EDGE,"E15")])]});var subQ5=makeQuery(id+"F11.boolean.opBoolean","SPLIT",EDGE,{"disambiguationData":[TD([subQ4])],"derivedFrom":makeQuery(id+"F7.boolean.opBoolean","SPLIT",EDGE,{"disambiguationData":[TD([subQ1,makeQuery(id+"F5.opExtrude","SWEPT_FACE",FACE,{"disambiguationData":[OSD([sQuery(id+"F4.wireOp",EDGE,"E1.0")])]}),subQ3,subQ4])],"derivedFrom":makeQuery(id+"F5.opExtrude","CAP_EDGE",EDGE,{"disambiguationData":[OSD([subQ2])],"isStart":true})})});var subQ6=makeQuery(id+"F18.imprint","INTERSECT",VERTEX,{"disambiguationData":[OD(0.0)],"derivedFrom":[subQ5,subQ0]});Q0=makeQuery(id+"F18.imprint","IMPRINT",FACE,{"disambiguationData":[TD([[makeQuery(id+"F18.imprint","IMPRINT",EDGE,{"disambiguationData":[TD([[subQ6,-1.0]])],"derivedFrom":subQ0}),1.0]])]});}
            extrude(context, id + "F19", {"entities" : qUnion([Q0]), "operationType" : NewBodyOperationType.ADD, "depth" : 6.35 * mm, "offsetDistance" : 25.4 * mm});
        }
        {
            var Q0;
            Q0=makeQuery(id+"F19.opExtrude","CAP_EDGE",EDGE,{"disambiguationData":[OSD([sQuery(id+"F18.wireOp",EDGE,"E55")])],"isStart":false});
            fillet(context, id + "F20", {"entities" : qUnion([Q0]), "radius" : 2.54 * mm, "tangentPropagation" : true, "allowEdgeOverflow" : false});
        }
        {
            var Q0;
            Q0=makeQuery(id+"F1.opExtrude","CAP_FACE",FACE,{"disambiguationData":[OSD([sQuery(id+"F0.wireOp",EDGE,"E0.bottom"),sQuery(id+"F0.wireOp",EDGE,"E0.top"),sQuery(id+"F0.wireOp",EDGE,"E0.left"),sQuery(id+"F0.wireOp",EDGE,"E0.right")])],"isStart":false});
            var sketch = newSketch(context, id + "F21", { "sketchPlane" : qUnion([Q0])});
            skLineSegment(sketch, "E56.bottom", {"start": v(154.86, 38.99) * mm, "end": v(95.94, 38.99) * mm});
            skLineSegment(sketch, "E56.top", {"start": v(154.86, 1.83) * mm, "end": v(95.94, 1.83) * mm});
            skLineSegment(sketch, "E56.left", {"start": v(154.86, 38.99) * mm, "end": v(154.86, 1.83) * mm});
            skLineSegment(sketch, "E56.right", {"start": v(95.94, 38.99) * mm, "end": v(95.94, 1.83) * mm});
            skPoint(sketch, "E57.MirrorCS.start.orphan", {"position": v(95.94, 38.99) * mm});
            skPoint(sketch, "E58.MirrorCS.start.orphan", {"position": v(154.86, 38.99) * mm});
            skSolve(sketch);
        }
        {
            var Q0;
            Q0=makeQuery(id+"F21.imprint","IMPRINT",FACE,{"disambiguationData":[TD([[makeQuery(id+"F21.imprint","IMPRINT",EDGE,{"derivedFrom":sQuery(id+"F21.wireOp",EDGE,"E56.bottom")}),1.0]])]});
            extrude(context, id + "F22", {"entities" : qUnion([Q0]), "operationType" : NewBodyOperationType.ADD, "depth" : 2.83 * mm, "offsetDistance" : 25.4 * mm});
        }
        {
            var Q0;
            Q0=makeQuery(id+"F22.opExtrude","SWEPT_EDGE",EDGE,{"disambiguationData":[OSD([sQuery(id+"F21.wireOp",EDGE,"E56.top"),sQuery(id+"F21.wireOp",EDGE,"E56.right")])]});
            var Q1;
            Q1=makeQuery(id+"F22.opExtrude","SWEPT_EDGE",EDGE,{"disambiguationData":[OSD([sQuery(id+"F21.wireOp",EDGE,"E56.bottom"),sQuery(id+"F21.wireOp",EDGE,"E56.right")])]});
            var Q2;
            Q2=makeQuery(id+"F22.opExtrude","SWEPT_EDGE",EDGE,{"disambiguationData":[OSD([sQuery(id+"F21.wireOp",EDGE,"E56.bottom"),sQuery(id+"F21.wireOp",EDGE,"E56.left")])]});
            var Q3;
            Q3=makeQuery(id+"F22.opExtrude","SWEPT_EDGE",EDGE,{"disambiguationData":[OSD([sQuery(id+"F21.wireOp",EDGE,"E56.top"),sQuery(id+"F21.wireOp",EDGE,"E56.left")])]});
            fillet(context, id + "F23", {"entities" : qUnion([Q0, Q1, Q2, Q3]), "radius" : 1.27 * mm, "tangentPropagation" : true, "allowEdgeOverflow" : false});
        }
        {
            var Q0;
            Q0=makeQuery(id+"F22.opExtrude","CAP_FACE",FACE,{"disambiguationData":[OSD([sQuery(id+"F21.wireOp",EDGE,"E56.bottom"),sQuery(id+"F21.wireOp",EDGE,"E56.top"),sQuery(id+"F21.wireOp",EDGE,"E56.left"),sQuery(id+"F21.wireOp",EDGE,"E56.right")])],"isStart":false});
            var sketch = newSketch(context, id + "F24", { "sketchPlane" : qUnion([Q0])});
            skLineSegment(sketch, "E59.0", {"start": v(97.79, 3.68) * mm, "end": v(153, 3.68) * mm});
            skLineSegment(sketch, "E59.1", {"start": v(97.79, 37.13) * mm, "end": v(97.79, 3.68) * mm});
            skLineSegment(sketch, "E59.2", {"start": v(153, 37.13) * mm, "end": v(97.79, 37.13) * mm});
            skLineSegment(sketch, "E59.3", {"start": v(153, 3.68) * mm, "end": v(153, 37.13) * mm});
            skSolve(sketch);
        }
        {
            var Q0;
            Q0=makeQuery(id+"F24.imprint","IMPRINT",FACE,{"disambiguationData":[TD([[makeQuery(id+"F24.imprint","IMPRINT",EDGE,{"derivedFrom":sQuery(id+"F24.wireOp",EDGE,"E59.0")}),1.0]])]});
            extrude(context, id + "F25", {"entities" : qUnion([Q0]), "operationType" : NewBodyOperationType.REMOVE, "oppositeDirection" : true, "depth" : 5.7 * mm, "offsetDistance" : 25.4 * mm});
        }
        {
            var Q0;
            Q0=makeQuery(id+"F1.opExtrude","CAP_FACE",FACE,{"disambiguationData":[OSD([sQuery(id+"F0.wireOp",EDGE,"E0.bottom"),sQuery(id+"F0.wireOp",EDGE,"E0.top"),sQuery(id+"F0.wireOp",EDGE,"E0.left"),sQuery(id+"F0.wireOp",EDGE,"E0.right")])],"isStart":false});
            var sketch = newSketch(context, id + "F26", { "sketchPlane" : qUnion([Q0])});
            skLineSegment(sketch, "E60.bottom", {"start": v(81.65, 38.98) * mm, "end": v(22.72, 38.98) * mm});
            skLineSegment(sketch, "E60.top", {"start": v(81.65, 1.82) * mm, "end": v(22.72, 1.82) * mm});
            skLineSegment(sketch, "E60.left", {"start": v(81.65, 38.98) * mm, "end": v(81.65, 1.82) * mm});
            skLineSegment(sketch, "E60.right", {"start": v(22.72, 38.98) * mm, "end": v(22.72, 1.82) * mm});
            skSolve(sketch);
        }
        {
            var Q0;
            Q0=makeQuery(id+"F26.imprint","IMPRINT",FACE,{"disambiguationData":[TD([[makeQuery(id+"F26.imprint","IMPRINT",EDGE,{"derivedFrom":sQuery(id+"F26.wireOp",EDGE,"E60.bottom")}),1.0]])]});
            extrude(context, id + "F27", {"entities" : qUnion([Q0]), "operationType" : NewBodyOperationType.ADD, "depth" : 2.84 * mm, "offsetDistance" : 25.4 * mm});
        }
        {
            var Q0;
            Q0=makeQuery(id+"F27.opExtrude","SWEPT_EDGE",EDGE,{"disambiguationData":[OSD([sQuery(id+"F26.wireOp",EDGE,"E60.top"),sQuery(id+"F26.wireOp",EDGE,"E60.right")])]});
            var Q1;
            Q1=makeQuery(id+"F27.opExtrude","SWEPT_EDGE",EDGE,{"disambiguationData":[OSD([sQuery(id+"F26.wireOp",EDGE,"E60.top"),sQuery(id+"F26.wireOp",EDGE,"E60.left")])]});
            var Q2;
            Q2=makeQuery(id+"F27.opExtrude","SWEPT_EDGE",EDGE,{"disambiguationData":[OSD([sQuery(id+"F26.wireOp",EDGE,"E60.bottom"),sQuery(id+"F26.wireOp",EDGE,"E60.left")])]});
            var Q3;
            Q3=makeQuery(id+"F27.opExtrude","SWEPT_EDGE",EDGE,{"disambiguationData":[OSD([sQuery(id+"F26.wireOp",EDGE,"E60.bottom"),sQuery(id+"F26.wireOp",EDGE,"E60.right")])]});
            fillet(context, id + "F28", {"entities" : qUnion([Q0, Q1, Q2, Q3]), "radius" : 1.27 * mm, "tangentPropagation" : true, "allowEdgeOverflow" : false});
        }
        {
            var Q0;
            Q0=makeQuery(id+"F27.opExtrude","CAP_FACE",FACE,{"disambiguationData":[OSD([sQuery(id+"F26.wireOp",EDGE,"E60.bottom"),sQuery(id+"F26.wireOp",EDGE,"E60.top"),sQuery(id+"F26.wireOp",EDGE,"E60.left"),sQuery(id+"F26.wireOp",EDGE,"E60.right")])],"isStart":false});
            var sketch = newSketch(context, id + "F29", { "sketchPlane" : qUnion([Q0])});
            skLineSegment(sketch, "E61.0", {"start": v(24.57, 3.67) * mm, "end": v(79.8, 3.67) * mm});
            skLineSegment(sketch, "E61.1", {"start": v(24.57, 37.12) * mm, "end": v(24.57, 3.67) * mm});
            skLineSegment(sketch, "E61.2", {"start": v(79.8, 37.12) * mm, "end": v(24.57, 37.12) * mm});
            skLineSegment(sketch, "E61.3", {"start": v(79.8, 3.67) * mm, "end": v(79.8, 37.12) * mm});
            skSolve(sketch);
        }
        {
            var Q0;
            Q0=makeQuery(id+"F29.imprint","IMPRINT",FACE,{"disambiguationData":[TD([[makeQuery(id+"F29.imprint","IMPRINT",EDGE,{"derivedFrom":sQuery(id+"F29.wireOp",EDGE,"E61.0")}),1.0]])]});
            extrude(context, id + "F30", {"entities" : qUnion([Q0]), "operationType" : NewBodyOperationType.REMOVE, "oppositeDirection" : true, "depth" : 5.7 * mm, "offsetDistance" : 25.4 * mm});
        }
        {
            var Q0;
            Q0=makeQuery(id+"F22.opExtrude","SWEPT_FACE",FACE,{"disambiguationData":[OSD([sQuery(id+"F21.wireOp",EDGE,"E56.top")])]});
            var sketch = newSketch(context, id + "F31", { "sketchPlane" : qUnion([Q0])});
            skLineSegment(sketch, "E62.bottom", {"start": v(103.17, 3.18) * mm, "end": v(147.62, 3.18) * mm});
            skLineSegment(sketch, "E62.top", {"start": v(103.17, 17.48) * mm, "end": v(147.62, 17.48) * mm});
            skLineSegment(sketch, "E62.left", {"start": v(103.17, 3.17) * mm, "end": v(103.17, 17.48) * mm});
            skLineSegment(sketch, "E62.right", {"start": v(147.62, 3.18) * mm, "end": v(147.62, 17.48) * mm});
            skLineSegment(sketch, "E63", {"start": v(125.4, 6) * mm, "end": v(124.34, 16.54) * mm, "construction": true});
            skLineSegment(sketch, "E64", {"start": v(125.4, 17.48) * mm, "end": v(125.4, 3.18) * mm, "construction": true});
            skSolve(sketch);
        }
        {
            var Q0;
            Q0=makeQuery(id+"F27.opExtrude","SWEPT_FACE",FACE,{"disambiguationData":[OSD([sQuery(id+"F26.wireOp",EDGE,"E60.top")])]});
            var sketch = newSketch(context, id + "F32", { "sketchPlane" : qUnion([Q0])});
            skLineSegment(sketch, "E65.bottom", {"start": v(29.96, 3.18) * mm, "end": v(74.4, 3.18) * mm});
            skLineSegment(sketch, "E65.top", {"start": v(29.96, 17.48) * mm, "end": v(74.4, 17.48) * mm});
            skLineSegment(sketch, "E65.left", {"start": v(29.96, 3.17) * mm, "end": v(29.96, 17.48) * mm});
            skLineSegment(sketch, "E65.right", {"start": v(74.4, 3.18) * mm, "end": v(74.4, 17.48) * mm});
            skPoint(sketch, "E66.orphan", {"position": v(52.18, 17.48) * mm});
            skPoint(sketch, "E67.start.orphan", {"position": v(52.18, 3.18) * mm});
            skSolve(sketch);
        }
        {
            var Q0;
            {var subQ0=sQuery(id+"F31.wireOp",EDGE,"E62.top");Q0=makeQuery(id+"F31.imprint","IMPRINT",FACE,{"disambiguationData":[TD([[makeQuery(id+"F31.imprint","IMPRINT",EDGE,{"derivedFrom":subQ0}),-1.0]])]});}
            var Q1;
            {var subQ0=sQuery(id+"F32.wireOp",EDGE,"E65.top");Q1=makeQuery(id+"F32.imprint","IMPRINT",FACE,{"disambiguationData":[TD([[makeQuery(id+"F32.imprint","IMPRINT",EDGE,{"derivedFrom":subQ0}),-1.0]])]});}
            extrude(context, id + "F33", {"entities" : qUnion([Q0, Q1]), "operationType" : NewBodyOperationType.ADD, "oppositeDirection" : true, "depth" : 2.3 * mm, "offsetDistance" : 25.4 * mm});
        }
        {
            var Q0;
            {var subQ0=sQuery(id+"F21.wireOp",EDGE,"E56.top");Q0=makeQuery(id+"F33.boolean.opBoolean","MERGE",FACE,{"derivedFrom":[makeQuery(id+"F22.opExtrude","SWEPT_FACE",FACE,{"disambiguationData":[OSD([subQ0])]}),makeQuery(id+"F33.opExtrude","CAP_FACE",FACE,{"disambiguationData":[OSD([subQ0,sQuery(id+"F31.wireOp",EDGE,"E62.top"),sQuery(id+"F31.wireOp",EDGE,"E62.left"),sQuery(id+"F31.wireOp",EDGE,"E62.right")])],"isStart":true})]});}
            var sketch = newSketch(context, id + "F34", { "sketchPlane" : qUnion([Q0])});
            skArc(sketch, "E68", {"start": v(103.17, 6) * mm, "mid": v(105.54, 3.9) * mm, "end": v(108.64, 3.17) * mm});
            skArc(sketch, "E69", {"start": v(142.16, 3.18) * mm, "mid": v(145.26, 3.9) * mm, "end": v(147.62, 6) * mm});
            skLineSegment(sketch, "E70", {"start": v(108.64, 3.17) * mm, "end": v(142.16, 3.18) * mm});
            skLineSegment(sketch, "E71", {"start": v(147.62, 6) * mm, "end": v(147.62, 17.48) * mm});
            skLineSegment(sketch, "E72", {"start": v(147.62, 17.48) * mm, "end": v(103.17, 17.48) * mm});
            skLineSegment(sketch, "E73", {"start": v(103.17, 17.48) * mm, "end": v(103.17, 6) * mm});
            skSolve(sketch);
        }
        {
            var Q0;
            {var subQ0=sQuery(id+"F26.wireOp",EDGE,"E60.top");Q0=makeQuery(id+"F33.boolean.opBoolean","MERGE",FACE,{"derivedFrom":[makeQuery(id+"F27.opExtrude","SWEPT_FACE",FACE,{"disambiguationData":[OSD([subQ0])]}),makeQuery(id+"F33.opExtrude","CAP_FACE",FACE,{"disambiguationData":[OSD([subQ0,sQuery(id+"F32.wireOp",EDGE,"E65.top"),sQuery(id+"F32.wireOp",EDGE,"E65.left"),sQuery(id+"F32.wireOp",EDGE,"E65.right")])],"isStart":true})]});}
            var sketch = newSketch(context, id + "F35", { "sketchPlane" : qUnion([Q0])});
            skPoint(sketch, "E74.end.orphan", {"position": v(35.42, 3.18) * mm});
            skArc(sketch, "E75", {"start": v(29.96, 6.02) * mm, "mid": v(32.33, 3.9) * mm, "end": v(35.42, 3.17) * mm});
            skPoint(sketch, "E76.start.orphan", {"position": v(68.95, 3.18) * mm});
            skArc(sketch, "E77", {"start": v(68.95, 3.18) * mm, "mid": v(72.04, 3.9) * mm, "end": v(74.4, 6.02) * mm});
            skLineSegment(sketch, "E78", {"start": v(35.42, 3.18) * mm, "end": v(68.95, 3.18) * mm});
            skLineSegment(sketch, "E79", {"start": v(74.4, 6.02) * mm, "end": v(74.4, 17.48) * mm});
            skLineSegment(sketch, "E80", {"start": v(74.4, 17.48) * mm, "end": v(29.96, 17.48) * mm});
            skLineSegment(sketch, "E81", {"start": v(29.96, 17.48) * mm, "end": v(29.96, 6.02) * mm});
            skSolve(sketch);
        }
        {
            var Q0;
            {var subQ0=sQuery(id+"F35.wireOp",EDGE,"E78");Q0=makeQuery(id+"F35.imprint","IMPRINT",FACE,{"disambiguationData":[TD([[makeQuery(id+"F35.imprint","IMPRINT",EDGE,{"derivedFrom":subQ0}),-1.0]])]});}
            extrude(context, id + "F36", {"entities" : qUnion([Q0]), "operationType" : NewBodyOperationType.REMOVE, "oppositeDirection" : true, "depth" : 2.54 * mm, "offsetDistance" : 25.4 * mm});
        }
        {
            var Q0;
            {var subQ0=sQuery(id+"F34.wireOp",EDGE,"E70");Q0=makeQuery(id+"F34.imprint","IMPRINT",FACE,{"disambiguationData":[TD([[makeQuery(id+"F34.imprint","IMPRINT",EDGE,{"derivedFrom":subQ0}),-1.0]])]});}
            extrude(context, id + "F37", {"entities" : qUnion([Q0]), "operationType" : NewBodyOperationType.REMOVE, "oppositeDirection" : true, "depth" : 2.54 * mm, "offsetDistance" : 25.4 * mm});
        }
        {
            var Q0;
            Q0=makeQuery(id+"F37.boolean.opBoolean","MERGE",FACE,{"derivedFrom":[makeQuery(id+"F36.boolean.opBoolean","MERGE",FACE,{"derivedFrom":[makeQuery(id+"F1.opExtrude","CAP_FACE",FACE,{"disambiguationData":[OSD([sQuery(id+"F0.wireOp",EDGE,"E0.bottom"),sQuery(id+"F0.wireOp",EDGE,"E0.top"),sQuery(id+"F0.wireOp",EDGE,"E0.left"),sQuery(id+"F0.wireOp",EDGE,"E0.right")])],"isStart":false}),makeQuery(id+"F36.opExtrude","SWEPT_FACE",FACE,{"disambiguationData":[OSD([sQuery(id+"F26.wireOp",EDGE,"E60.top"),sQuery(id+"F35.wireOp",EDGE,"E78")])]})]}),makeQuery(id+"F37.opExtrude","SWEPT_FACE",FACE,{"disambiguationData":[OSD([sQuery(id+"F21.wireOp",EDGE,"E56.top"),sQuery(id+"F34.wireOp",EDGE,"E70")])]})]});
            var sketch = newSketch(context, id + "F38", { "sketchPlane" : qUnion([Q0])});
            skLineSegment(sketch, "E82.bottom", {"start": v(8.62, 38.98) * mm, "end": v(-50.44, 38.98) * mm});
            skLineSegment(sketch, "E82.top", {"start": v(8.62, -16.01) * mm, "end": v(-50.44, -16.01) * mm});
            skLineSegment(sketch, "E82.left", {"start": v(8.62, 38.98) * mm, "end": v(8.62, -16.01) * mm});
            skLineSegment(sketch, "E82.right", {"start": v(-50.44, 38.98) * mm, "end": v(-50.44, -16.01) * mm});
            skSolve(sketch);
        }
        {
            var Q0;
            Q0=makeQuery(id+"F38.imprint","IMPRINT",FACE,{"disambiguationData":[TD([[makeQuery(id+"F38.imprint","IMPRINT",EDGE,{"derivedFrom":sQuery(id+"F38.wireOp",EDGE,"E82.bottom")}),1.0]])]});
            extrude(context, id + "F39", {"entities" : qUnion([Q0]), "operationType" : NewBodyOperationType.ADD, "depth" : 2.84 * mm, "offsetDistance" : 25.4 * mm});
        }
        {
            var Q0;
            Q0=makeQuery(id+"F39.opExtrude","SWEPT_EDGE",EDGE,{"disambiguationData":[OSD([sQuery(id+"F38.wireOp",EDGE,"E82.top"),sQuery(id+"F38.wireOp",EDGE,"E82.left")])]});
            var Q1;
            Q1=makeQuery(id+"F39.opExtrude","SWEPT_EDGE",EDGE,{"disambiguationData":[OSD([sQuery(id+"F38.wireOp",EDGE,"E82.top"),sQuery(id+"F38.wireOp",EDGE,"E82.right")])]});
            var Q2;
            Q2=makeQuery(id+"F39.opExtrude","SWEPT_EDGE",EDGE,{"disambiguationData":[OSD([sQuery(id+"F38.wireOp",EDGE,"E82.bottom"),sQuery(id+"F38.wireOp",EDGE,"E82.left")])]});
            var Q3;
            Q3=makeQuery(id+"F39.opExtrude","SWEPT_EDGE",EDGE,{"disambiguationData":[OSD([sQuery(id+"F38.wireOp",EDGE,"E82.bottom"),sQuery(id+"F38.wireOp",EDGE,"E82.right")])]});
            fillet(context, id + "F40", {"entities" : qUnion([Q0, Q1, Q2, Q3]), "radius" : 1.27 * mm, "tangentPropagation" : true, "allowEdgeOverflow" : false});
        }
        {
            var Q0;
            Q0=makeQuery(id+"F39.opExtrude","CAP_FACE",FACE,{"disambiguationData":[OSD([sQuery(id+"F38.wireOp",EDGE,"E82.bottom"),sQuery(id+"F38.wireOp",EDGE,"E82.top"),sQuery(id+"F38.wireOp",EDGE,"E82.left"),sQuery(id+"F38.wireOp",EDGE,"E82.right")])],"isStart":false});
            var sketch = newSketch(context, id + "F41", { "sketchPlane" : qUnion([Q0])});
            skLineSegment(sketch, "E83.bottom", {"start": v(-48.6, 37.12) * mm, "end": v(6.77, 37.12) * mm});
            skLineSegment(sketch, "E83.top", {"start": v(-48.6, -14.16) * mm, "end": v(6.77, -14.16) * mm});
            skLineSegment(sketch, "E83.left", {"start": v(-48.6, 37.12) * mm, "end": v(-48.6, -14.16) * mm});
            skLineSegment(sketch, "E83.right", {"start": v(6.77, 37.12) * mm, "end": v(6.77, -14.16) * mm});
            skSolve(sketch);
        }
        {
            var Q0;
            Q0=makeQuery(id+"F41.imprint","IMPRINT",FACE,{"disambiguationData":[TD([[makeQuery(id+"F41.imprint","IMPRINT",EDGE,{"derivedFrom":sQuery(id+"F41.wireOp",EDGE,"E83.bottom")}),-1.0]])]});
            extrude(context, id + "F42", {"entities" : qUnion([Q0]), "operationType" : NewBodyOperationType.REMOVE, "oppositeDirection" : true, "depth" : 5.7 * mm, "offsetDistance" : 25.4 * mm});
        }
        {
            var Q0;
            Q0=makeQuery(id+"F37.boolean.opBoolean","MERGE",FACE,{"derivedFrom":[makeQuery(id+"F36.boolean.opBoolean","MERGE",FACE,{"derivedFrom":[makeQuery(id+"F1.opExtrude","CAP_FACE",FACE,{"disambiguationData":[OSD([sQuery(id+"F0.wireOp",EDGE,"E0.bottom"),sQuery(id+"F0.wireOp",EDGE,"E0.top"),sQuery(id+"F0.wireOp",EDGE,"E0.left"),sQuery(id+"F0.wireOp",EDGE,"E0.right")])],"isStart":false}),makeQuery(id+"F36.opExtrude","SWEPT_FACE",FACE,{"disambiguationData":[OSD([sQuery(id+"F26.wireOp",EDGE,"E60.top"),sQuery(id+"F35.wireOp",EDGE,"E78")])]})]}),makeQuery(id+"F37.opExtrude","SWEPT_FACE",FACE,{"disambiguationData":[OSD([sQuery(id+"F21.wireOp",EDGE,"E56.top"),sQuery(id+"F34.wireOp",EDGE,"E70")])]})]});
            var sketch = newSketch(context, id + "F43", { "sketchPlane" : qUnion([Q0])});
            skLineSegment(sketch, "E84.bottom", {"start": v(-64.54, 38.98) * mm, "end": v(-153.44, 38.98) * mm});
            skLineSegment(sketch, "E84.top", {"start": v(-64.54, -40.4) * mm, "end": v(-100.58, -40.4) * mm});
            skLineSegment(sketch, "E84.left", {"start": v(-64.54, 38.98) * mm, "end": v(-64.54, -40.4) * mm});
            skLineSegment(sketch, "E84.right", {"start": v(-153.44, 38.98) * mm, "end": v(-153.44, -40.4) * mm});
            skLineSegment(sketch, "E85.top", {"start": v(-117.37, -31.61) * mm, "end": v(-100.58, -31.61) * mm});
            skLineSegment(sketch, "E85.left", {"start": v(-117.37, -40.4) * mm, "end": v(-117.37, -31.61) * mm});
            skLineSegment(sketch, "E85.right", {"start": v(-100.58, -40.4) * mm, "end": v(-100.58, -31.61) * mm});
            skLineSegment(sketch, "E86.trimOffspring", {"start": v(-117.37, -40.4) * mm, "end": v(-153.44, -40.4) * mm});
            skSolve(sketch);
        }
        {
            var Q0;
            Q0=makeQuery(id+"F43.imprint","IMPRINT",FACE,{"disambiguationData":[TD([[makeQuery(id+"F43.imprint","IMPRINT",EDGE,{"derivedFrom":sQuery(id+"F43.wireOp",EDGE,"E84.bottom")}),1.0]])]});
            extrude(context, id + "F44", {"entities" : qUnion([Q0]), "operationType" : NewBodyOperationType.ADD, "depth" : 2.84 * mm, "offsetDistance" : 25.4 * mm});
        }
        {
            var Q0;
            Q0=makeQuery(id+"F44.opExtrude","SWEPT_EDGE",EDGE,{"disambiguationData":[OSD([sQuery(id+"F43.wireOp",EDGE,"E84.top"),sQuery(id+"F43.wireOp",EDGE,"E84.left")])]});
            var Q1;
            Q1=makeQuery(id+"F44.opExtrude","SWEPT_EDGE",EDGE,{"disambiguationData":[OSD([sQuery(id+"F43.wireOp",EDGE,"E84.top"),sQuery(id+"F43.wireOp",EDGE,"E85.right")])]});
            var Q2;
            Q2=makeQuery(id+"F44.opExtrude","SWEPT_EDGE",EDGE,{"disambiguationData":[OSD([sQuery(id+"F43.wireOp",EDGE,"E85.top"),sQuery(id+"F43.wireOp",EDGE,"E85.right")])]});
            var Q3;
            Q3=makeQuery(id+"F44.opExtrude","SWEPT_EDGE",EDGE,{"disambiguationData":[OSD([sQuery(id+"F43.wireOp",EDGE,"E85.top"),sQuery(id+"F43.wireOp",EDGE,"E85.left")])]});
            var Q4;
            Q4=makeQuery(id+"F44.opExtrude","SWEPT_EDGE",EDGE,{"disambiguationData":[OSD([sQuery(id+"F43.wireOp",EDGE,"E85.left"),sQuery(id+"F43.wireOp",EDGE,"E86.trimOffspring")])]});
            var Q5;
            Q5=makeQuery(id+"F44.opExtrude","SWEPT_EDGE",EDGE,{"disambiguationData":[OSD([sQuery(id+"F43.wireOp",EDGE,"E84.right"),sQuery(id+"F43.wireOp",EDGE,"E86.trimOffspring")])]});
            var Q6;
            Q6=makeQuery(id+"F44.opExtrude","SWEPT_EDGE",EDGE,{"disambiguationData":[OSD([sQuery(id+"F43.wireOp",EDGE,"E84.bottom"),sQuery(id+"F43.wireOp",EDGE,"E84.left")])]});
            var Q7;
            Q7=makeQuery(id+"F44.opExtrude","SWEPT_EDGE",EDGE,{"disambiguationData":[OSD([sQuery(id+"F43.wireOp",EDGE,"E84.bottom"),sQuery(id+"F43.wireOp",EDGE,"E84.right")])]});
            fillet(context, id + "F45", {"entities" : qUnion([Q0, Q1, Q2, Q3, Q4, Q5, Q6, Q7]), "radius" : 1.27 * mm, "tangentPropagation" : true, "allowEdgeOverflow" : false});
        }
        {
            var Q0;
            Q0=makeQuery(id+"F44.opExtrude","CAP_FACE",FACE,{"disambiguationData":[OSD([sQuery(id+"F43.wireOp",EDGE,"E84.bottom"),sQuery(id+"F43.wireOp",EDGE,"E84.top"),sQuery(id+"F43.wireOp",EDGE,"E84.left"),sQuery(id+"F43.wireOp",EDGE,"E84.right"),sQuery(id+"F43.wireOp",EDGE,"E85.top"),sQuery(id+"F43.wireOp",EDGE,"E85.left"),sQuery(id+"F43.wireOp",EDGE,"E85.right"),sQuery(id+"F43.wireOp",EDGE,"E86.trimOffspring")])],"isStart":false});
            var sketch = newSketch(context, id + "F46", { "sketchPlane" : qUnion([Q0])});
            skArc(sketch, "E87.0", {"start": v(-101.85, -29.76) * mm, "mid": v(-99.64, -30.67) * mm, "end": v(-98.73, -32.88) * mm});
            skLineSegment(sketch, "E87.1", {"start": v(-116.1, -29.76) * mm, "end": v(-101.85, -29.76) * mm});
            skLineSegment(sketch, "E87.2", {"start": v(-98.73, -32.88) * mm, "end": v(-98.73, -38.54) * mm});
            skArc(sketch, "E87.3", {"start": v(-119.23, -32.88) * mm, "mid": v(-118.31, -30.67) * mm, "end": v(-116.1, -29.76) * mm});
            skLineSegment(sketch, "E87.4", {"start": v(-119.23, -38.54) * mm, "end": v(-119.23, -32.88) * mm});
            skLineSegment(sketch, "E87.5", {"start": v(-151.59, -38.54) * mm, "end": v(-119.23, -38.54) * mm});
            skLineSegment(sketch, "E87.6", {"start": v(-98.73, -38.54) * mm, "end": v(-66.4, -38.54) * mm});
            skLineSegment(sketch, "E87.7", {"start": v(-66.4, -38.54) * mm, "end": v(-66.4, 37.12) * mm});
            skLineSegment(sketch, "E87.8", {"start": v(-66.4, 37.12) * mm, "end": v(-151.59, 37.12) * mm});
            skLineSegment(sketch, "E87.9", {"start": v(-151.59, 37.12) * mm, "end": v(-151.59, -38.54) * mm});
            skSolve(sketch);
        }
        {
            var Q0;
            Q0=makeQuery(id+"F46.imprint","IMPRINT",FACE,{"disambiguationData":[TD([[makeQuery(id+"F46.imprint","IMPRINT",EDGE,{"derivedFrom":sQuery(id+"F46.wireOp",EDGE,"E87.0")}),1.0]])]});
            extrude(context, id + "F47", {"entities" : qUnion([Q0]), "operationType" : NewBodyOperationType.REMOVE, "oppositeDirection" : true, "depth" : 5.7 * mm, "offsetDistance" : 25.4 * mm});
        }
        {
            var Q0;
            Q0=makeQuery(id+"F37.boolean.opBoolean","MERGE",FACE,{"derivedFrom":[makeQuery(id+"F36.boolean.opBoolean","MERGE",FACE,{"derivedFrom":[makeQuery(id+"F1.opExtrude","CAP_FACE",FACE,{"disambiguationData":[OSD([sQuery(id+"F0.wireOp",EDGE,"E0.bottom"),sQuery(id+"F0.wireOp",EDGE,"E0.top"),sQuery(id+"F0.wireOp",EDGE,"E0.left"),sQuery(id+"F0.wireOp",EDGE,"E0.right")])],"isStart":false}),makeQuery(id+"F36.opExtrude","SWEPT_FACE",FACE,{"disambiguationData":[OSD([sQuery(id+"F26.wireOp",EDGE,"E60.top"),sQuery(id+"F35.wireOp",EDGE,"E78")])]})]}),makeQuery(id+"F37.opExtrude","SWEPT_FACE",FACE,{"disambiguationData":[OSD([sQuery(id+"F21.wireOp",EDGE,"E56.top"),sQuery(id+"F34.wireOp",EDGE,"E70")])]})]});
            var sketch = newSketch(context, id + "F48", { "sketchPlane" : qUnion([Q0])});
            skLineSegment(sketch, "E88", {"start": v(63.1, 3.67) * mm, "end": v(52.18, -9.03) * mm});
            skPoint(sketch, "E88.endSnap0", {"position": v(52.18, 3.67) * mm});
            skLineSegment(sketch, "E89", {"start": v(52.18, -9.03) * mm, "end": v(41.26, 3.67) * mm});
            skLineSegment(sketch, "E90", {"start": v(41.26, 3.67) * mm, "end": v(63.1, 3.67) * mm});
            skLineSegment(sketch, "E91", {"start": v(136.33, 3.68) * mm, "end": v(125.4, -9.02) * mm});
            skLineSegment(sketch, "E92", {"start": v(125.4, -9.02) * mm, "end": v(114.48, 3.68) * mm});
            skSolve(sketch);
        }
        {
            var Q0;
            Q0=makeQuery(id+"F48.imprint","IMPRINT",FACE,{"disambiguationData":[TD([[makeQuery(id+"F48.imprint","IMPRINT",EDGE,{"derivedFrom":sQuery(id+"F48.wireOp",EDGE,"E88")}),-1.0]])]});
            var Q1;
            {var subQ0=sQuery(id+"F48.wireOp",EDGE,"E91");Q1=makeQuery(id+"F48.imprint","IMPRINT",FACE,{"disambiguationData":[TD([[makeQuery(id+"F48.imprint","IMPRINT",EDGE,{"derivedFrom":subQ0}),-1.0]])]});}
            extrude(context, id + "F49", {"entities" : qUnion([Q0, Q1]), "operationType" : NewBodyOperationType.REMOVE, "oppositeDirection" : true, "depth" : 0.4 * mm, "offsetDistance" : 25.4 * mm});
        }
        {
            var Q0;
            Q0=makeQuery(id+"F49.boolean.opBoolean","COPY",EDGE,{"derivedFrom":makeQuery(id+"F49.opExtrude","SWEPT_EDGE",EDGE,{"disambiguationData":[OSD([sQuery(id+"F48.wireOp",EDGE,"E91"),sQuery(id+"F48.wireOp",EDGE,"E92")])]})});
            var Q1;
            Q1=makeQuery(id+"F49.boolean.opBoolean","COPY",EDGE,{"derivedFrom":makeQuery(id+"F49.opExtrude","SWEPT_EDGE",EDGE,{"disambiguationData":[OSD([sQuery(id+"F48.wireOp",EDGE,"E88"),sQuery(id+"F48.wireOp",EDGE,"E89")])]})});
            fillet(context, id + "F50", {"entities" : qUnion([Q0, Q1]), "radius" : 6.35 * mm, "tangentPropagation" : true, "allowEdgeOverflow" : false});
        }
        {
            var Q0;
            Q0=makeQuery(id+"F37.boolean.opBoolean","MERGE",FACE,{"derivedFrom":[makeQuery(id+"F36.boolean.opBoolean","MERGE",FACE,{"derivedFrom":[makeQuery(id+"F1.opExtrude","CAP_FACE",FACE,{"disambiguationData":[OSD([sQuery(id+"F0.wireOp",EDGE,"E0.bottom"),sQuery(id+"F0.wireOp",EDGE,"E0.top"),sQuery(id+"F0.wireOp",EDGE,"E0.left"),sQuery(id+"F0.wireOp",EDGE,"E0.right")])],"isStart":false}),makeQuery(id+"F36.opExtrude","SWEPT_FACE",FACE,{"disambiguationData":[OSD([sQuery(id+"F26.wireOp",EDGE,"E60.top"),sQuery(id+"F35.wireOp",EDGE,"E78")])]})]}),makeQuery(id+"F37.opExtrude","SWEPT_FACE",FACE,{"disambiguationData":[OSD([sQuery(id+"F21.wireOp",EDGE,"E56.top"),sQuery(id+"F34.wireOp",EDGE,"E70")])]})]});
            var sketch = newSketch(context, id + "F51", { "sketchPlane" : qUnion([Q0])});
            skCircle(sketch, "E93", {"center": v(-57.4, 34.24) * mm, "radius": 4.76 * mm});
            skCircle(sketch, "E94", {"center": v(-57.4, -7.04) * mm, "radius": 4.76 * mm});
            skCircle(sketch, "E95", {"center": v(15.77, -7.05) * mm, "radius": 4.76 * mm});
            skCircle(sketch, "E96", {"center": v(15.77, 34.23) * mm, "radius": 4.76 * mm});
            skCircle(sketch, "E97", {"center": v(88.8, 34.24) * mm, "radius": 4.76 * mm});
            skCircle(sketch, "E98", {"center": v(88.8, -7.04) * mm, "radius": 4.76 * mm});
            skCircle(sketch, "E99", {"center": v(147.71, -7.13) * mm, "radius": 4.76 * mm});
            skLineSegment(sketch, "E100", {"start": v(16.63, -2.36) * mm, "end": v(152.77, -2.36) * mm, "construction": true});
            skSolve(sketch);
        }
        {
            var Q0;
            Q0=makeQuery(id+"F51.imprint","IMPRINT",FACE,{"disambiguationData":[TD([[makeQuery(id+"F51.imprint","IMPRINT",EDGE,{"derivedFrom":sQuery(id+"F51.wireOp",EDGE,"E93")}),1.0]])]});
            var Q1;
            Q1=makeQuery(id+"F51.imprint","IMPRINT",FACE,{"disambiguationData":[TD([[makeQuery(id+"F51.imprint","IMPRINT",EDGE,{"derivedFrom":sQuery(id+"F51.wireOp",EDGE,"E94")}),1.0]])]});
            var Q2;
            Q2=makeQuery(id+"F51.imprint","IMPRINT",FACE,{"disambiguationData":[TD([[makeQuery(id+"F51.imprint","IMPRINT",EDGE,{"derivedFrom":sQuery(id+"F51.wireOp",EDGE,"E96")}),1.0]])]});
            var Q3;
            Q3=makeQuery(id+"F51.imprint","IMPRINT",FACE,{"disambiguationData":[TD([[makeQuery(id+"F51.imprint","IMPRINT",EDGE,{"derivedFrom":sQuery(id+"F51.wireOp",EDGE,"E95")}),1.0]])]});
            var Q4;
            Q4=makeQuery(id+"F51.imprint","IMPRINT",FACE,{"disambiguationData":[TD([[makeQuery(id+"F51.imprint","IMPRINT",EDGE,{"derivedFrom":sQuery(id+"F51.wireOp",EDGE,"E98")}),1.0]])]});
            var Q5;
            Q5=makeQuery(id+"F51.imprint","IMPRINT",FACE,{"disambiguationData":[TD([[makeQuery(id+"F51.imprint","IMPRINT",EDGE,{"derivedFrom":sQuery(id+"F51.wireOp",EDGE,"E97")}),1.0]])]});
            var Q6;
            Q6=makeQuery(id+"F51.imprint","IMPRINT",FACE,{"disambiguationData":[TD([[makeQuery(id+"F51.imprint","IMPRINT",EDGE,{"derivedFrom":sQuery(id+"F51.wireOp",EDGE,"E99")}),1.0]])]});
            extrude(context, id + "F52", {"entities" : qUnion([Q0, Q1, Q2, Q3, Q4, Q5, Q6]), "operationType" : NewBodyOperationType.REMOVE, "oppositeDirection" : true, "depth" : 0.4 * mm, "offsetDistance" : 25.4 * mm});
        }
        {
            var Q0;
            Q0=makeQuery(id+"F37.boolean.opBoolean","MERGE",FACE,{"derivedFrom":[makeQuery(id+"F36.boolean.opBoolean","MERGE",FACE,{"derivedFrom":[makeQuery(id+"F1.opExtrude","CAP_FACE",FACE,{"disambiguationData":[OSD([sQuery(id+"F0.wireOp",EDGE,"E0.bottom"),sQuery(id+"F0.wireOp",EDGE,"E0.top"),sQuery(id+"F0.wireOp",EDGE,"E0.left"),sQuery(id+"F0.wireOp",EDGE,"E0.right")])],"isStart":false}),makeQuery(id+"F36.opExtrude","SWEPT_FACE",FACE,{"disambiguationData":[OSD([sQuery(id+"F26.wireOp",EDGE,"E60.top"),sQuery(id+"F35.wireOp",EDGE,"E78")])]})]}),makeQuery(id+"F37.opExtrude","SWEPT_FACE",FACE,{"disambiguationData":[OSD([sQuery(id+"F21.wireOp",EDGE,"E56.top"),sQuery(id+"F34.wireOp",EDGE,"E70")])]})]});
            var sketch = newSketch(context, id + "F53", { "sketchPlane" : qUnion([Q0])});
            skCircle(sketch, "E101", {"center": v(-108.98, -37.17) * mm, "radius": 2.39 * mm});
            skPoint(sketch, "E101.centerSnap0", {"position": v(-108.98, -31.61) * mm});
            skSolve(sketch);
        }
        {
            var Q0;
            Q0=makeQuery(id+"F53.imprint","IMPRINT",FACE,{"disambiguationData":[TD([[makeQuery(id+"F53.imprint","IMPRINT",EDGE,{"derivedFrom":sQuery(id+"F53.wireOp",EDGE,"E101")}),1.0]])]});
            extrude(context, id + "F54", {"entities" : qUnion([Q0]), "operationType" : NewBodyOperationType.REMOVE, "oppositeDirection" : true, "depth" : 2.54 * mm, "offsetDistance" : 25.4 * mm});
        }
        {
            var Q0;
            Q0=makeQuery(id+"F37.boolean.opBoolean","MERGE",FACE,{"derivedFrom":[makeQuery(id+"F36.boolean.opBoolean","MERGE",FACE,{"derivedFrom":[makeQuery(id+"F1.opExtrude","CAP_FACE",FACE,{"disambiguationData":[OSD([sQuery(id+"F0.wireOp",EDGE,"E0.bottom"),sQuery(id+"F0.wireOp",EDGE,"E0.top"),sQuery(id+"F0.wireOp",EDGE,"E0.left"),sQuery(id+"F0.wireOp",EDGE,"E0.right")])],"isStart":false}),makeQuery(id+"F36.opExtrude","SWEPT_FACE",FACE,{"disambiguationData":[OSD([sQuery(id+"F26.wireOp",EDGE,"E60.top"),sQuery(id+"F35.wireOp",EDGE,"E78")])]})]}),makeQuery(id+"F37.opExtrude","SWEPT_FACE",FACE,{"disambiguationData":[OSD([sQuery(id+"F21.wireOp",EDGE,"E56.top"),sQuery(id+"F34.wireOp",EDGE,"E70")])]})]});
            var sketch = newSketch(context, id + "F55", { "sketchPlane" : qUnion([Q0])});
            skLineSegment(sketch, "E102.bottom", {"start": v(-29.34, -24.7) * mm, "end": v(138.93, -24.7) * mm});
            skLineSegment(sketch, "E102.top", {"start": v(-29.34, -40.58) * mm, "end": v(138.93, -40.58) * mm});
            skLineSegment(sketch, "E103", {"start": v(-29.34, -40.58) * mm, "end": v(-42.04, -32.64) * mm});
            skPoint(sketch, "E103.endSnap0", {"position": v(-29.34, -32.64) * mm});
            skLineSegment(sketch, "E104", {"start": v(-42.04, -32.64) * mm, "end": v(-29.34, -24.7) * mm});
            skLineSegment(sketch, "E105", {"start": v(138.93, -40.58) * mm, "end": v(151.63, -32.64) * mm});
            skPoint(sketch, "E105.endSnap0", {"position": v(138.93, -32.64) * mm});
            skLineSegment(sketch, "E106", {"start": v(151.63, -32.64) * mm, "end": v(138.93, -24.7) * mm});
            skSolve(sketch);
        }
        {
            var Q0;
            Q0=makeQuery(id+"F55.imprint","IMPRINT",FACE,{"disambiguationData":[TD([[makeQuery(id+"F55.imprint","IMPRINT",EDGE,{"derivedFrom":sQuery(id+"F55.wireOp",EDGE,"E102.bottom")}),-1.0]])]});
            extrude(context, id + "F56", {"entities" : qUnion([Q0]), "operationType" : NewBodyOperationType.ADD, "depth" : 2.84 * mm, "offsetDistance" : 25.4 * mm});
        }
        {
            var Q0;
            Q0=makeQuery(id+"F56.opExtrude","SWEPT_EDGE",EDGE,{"disambiguationData":[OSD([sQuery(id+"F55.wireOp",EDGE,"E103"),sQuery(id+"F55.wireOp",EDGE,"E104")])]});
            var Q1;
            Q1=makeQuery(id+"F56.opExtrude","SWEPT_EDGE",EDGE,{"disambiguationData":[OSD([sQuery(id+"F55.wireOp",EDGE,"E102.top"),sQuery(id+"F55.wireOp",EDGE,"E103")])]});
            var Q2;
            Q2=makeQuery(id+"F56.opExtrude","SWEPT_EDGE",EDGE,{"disambiguationData":[OSD([sQuery(id+"F55.wireOp",EDGE,"E102.bottom"),sQuery(id+"F55.wireOp",EDGE,"E104")])]});
            var Q3;
            Q3=makeQuery(id+"F56.opExtrude","SWEPT_EDGE",EDGE,{"disambiguationData":[OSD([sQuery(id+"F55.wireOp",EDGE,"E105"),sQuery(id+"F55.wireOp",EDGE,"E106")])]});
            var Q4;
            Q4=makeQuery(id+"F56.opExtrude","SWEPT_EDGE",EDGE,{"disambiguationData":[OSD([sQuery(id+"F55.wireOp",EDGE,"E102.top"),sQuery(id+"F55.wireOp",EDGE,"E105")])]});
            var Q5;
            Q5=makeQuery(id+"F56.opExtrude","SWEPT_EDGE",EDGE,{"disambiguationData":[OSD([sQuery(id+"F55.wireOp",EDGE,"E102.bottom"),sQuery(id+"F55.wireOp",EDGE,"E106")])]});
            fillet(context, id + "F57", {"entities" : qUnion([Q0, Q1, Q2, Q3, Q4, Q5]), "radius" : 1.27 * mm, "tangentPropagation" : true, "allowEdgeOverflow" : false});
        }
        {
            var Q0;
            Q0=makeQuery(id+"F56.opExtrude","CAP_FACE",FACE,{"disambiguationData":[OSD([sQuery(id+"F55.wireOp",EDGE,"E102.bottom"),sQuery(id+"F55.wireOp",EDGE,"E102.top"),sQuery(id+"F55.wireOp",EDGE,"E103"),sQuery(id+"F55.wireOp",EDGE,"E104"),sQuery(id+"F55.wireOp",EDGE,"E105"),sQuery(id+"F55.wireOp",EDGE,"E106")])],"isStart":false});
            var sketch = newSketch(context, id + "F58", { "sketchPlane" : qUnion([Q0])});
            skLineSegment(sketch, "E107", {"start": v(54.8, -24.7) * mm, "end": v(54.8, -40.58) * mm, "construction": true});
            skLineSegment(sketch, "E108.bottom", {"start": v(67.5, -26.56) * mm, "end": v(42.1, -26.56) * mm});
            skLineSegment(sketch, "E108.top", {"start": v(67.5, -38.72) * mm, "end": v(42.1, -38.72) * mm});
            skLineSegment(sketch, "E108.left", {"start": v(67.5, -26.56) * mm, "end": v(67.5, -38.72) * mm});
            skLineSegment(sketch, "E108.right", {"start": v(42.1, -26.56) * mm, "end": v(42.1, -38.72) * mm});
            skPoint(sketch, "E108.middle", {"position": v(54.8, -32.64) * mm});
            skLineSegment(sketch, "E109.bottom", {"start": v(69.35, -26.56) * mm, "end": v(136.56, -26.56) * mm});
            skLineSegment(sketch, "E109.top", {"start": v(69.35, -38.72) * mm, "end": v(136.56, -38.72) * mm});
            skLineSegment(sketch, "E109.left", {"start": v(69.35, -26.56) * mm, "end": v(69.35, -38.72) * mm});
            skLineSegment(sketch, "E109.right", {"start": v(136.56, -26.56) * mm, "end": v(136.56, -38.72) * mm});
            skLineSegment(sketch, "E110.bottom", {"start": v(40.24, -26.56) * mm, "end": v(-27.12, -26.56) * mm});
            skLineSegment(sketch, "E110.top", {"start": v(40.24, -38.72) * mm, "end": v(-27.12, -38.72) * mm});
            skLineSegment(sketch, "E110.left", {"start": v(40.24, -26.56) * mm, "end": v(40.24, -38.72) * mm});
            skLineSegment(sketch, "E110.right", {"start": v(-27.12, -26.56) * mm, "end": v(-27.12, -38.72) * mm});
            skLineSegment(sketch, "E111", {"start": v(138.42, -38.72) * mm, "end": v(138.42, -26.56) * mm});
            skLineSegment(sketch, "E112", {"start": v(138.42, -26.56) * mm, "end": v(148.12, -32.64) * mm});
            skPoint(sketch, "E112.endSnap0", {"position": v(138.42, -32.64) * mm});
            skLineSegment(sketch, "E113", {"start": v(148.12, -32.64) * mm, "end": v(138.42, -38.72) * mm});
            skLineSegment(sketch, "E114", {"start": v(-28.98, -38.72) * mm, "end": v(-28.98, -26.56) * mm});
            skLineSegment(sketch, "E115", {"start": v(-28.98, -26.56) * mm, "end": v(-38.4, -32.64) * mm});
            skPoint(sketch, "E115.endSnap0", {"position": v(-27.12, -32.64) * mm});
            skLineSegment(sketch, "E116", {"start": v(-38.4, -32.64) * mm, "end": v(-28.98, -38.72) * mm});
            skSolve(sketch);
        }
        {
            var Q0;
            Q0=makeQuery(id+"F58.imprint","IMPRINT",FACE,{"disambiguationData":[TD([[makeQuery(id+"F58.imprint","IMPRINT",EDGE,{"derivedFrom":sQuery(id+"F58.wireOp",EDGE,"E114")}),1.0]])]});
            var Q1;
            Q1=makeQuery(id+"F58.imprint","IMPRINT",FACE,{"disambiguationData":[TD([[makeQuery(id+"F58.imprint","IMPRINT",EDGE,{"derivedFrom":sQuery(id+"F58.wireOp",EDGE,"E110.bottom")}),1.0]])]});
            var Q2;
            Q2=makeQuery(id+"F58.imprint","IMPRINT",FACE,{"disambiguationData":[TD([[makeQuery(id+"F58.imprint","IMPRINT",EDGE,{"derivedFrom":sQuery(id+"F58.wireOp",EDGE,"E108.bottom")}),1.0]])]});
            var Q3;
            Q3=makeQuery(id+"F58.imprint","IMPRINT",FACE,{"disambiguationData":[TD([[makeQuery(id+"F58.imprint","IMPRINT",EDGE,{"derivedFrom":sQuery(id+"F58.wireOp",EDGE,"E109.bottom")}),-1.0]])]});
            var Q4;
            Q4=makeQuery(id+"F58.imprint","IMPRINT",FACE,{"disambiguationData":[TD([[makeQuery(id+"F58.imprint","IMPRINT",EDGE,{"derivedFrom":sQuery(id+"F58.wireOp",EDGE,"E111")}),-1.0]])]});
            extrude(context, id + "F59", {"entities" : qUnion([Q0, Q1, Q2, Q3, Q4]), "operationType" : NewBodyOperationType.REMOVE, "oppositeDirection" : true, "depth" : 5.7 * mm, "offsetDistance" : 25.4 * mm});
        }
        {
            var Q0;
            Q0=makeQuery(id+"F59.boolean.opBoolean","COPY",EDGE,{"derivedFrom":makeQuery(id+"F59.opExtrude","SWEPT_EDGE",EDGE,{"disambiguationData":[OSD([sQuery(id+"F58.wireOp",EDGE,"E115"),sQuery(id+"F58.wireOp",EDGE,"E116")])]})});
            var Q1;
            Q1=makeQuery(id+"F59.boolean.opBoolean","COPY",EDGE,{"derivedFrom":makeQuery(id+"F59.opExtrude","SWEPT_EDGE",EDGE,{"disambiguationData":[OSD([sQuery(id+"F58.wireOp",EDGE,"E114"),sQuery(id+"F58.wireOp",EDGE,"E116")])]})});
            var Q2;
            Q2=makeQuery(id+"F59.boolean.opBoolean","COPY",EDGE,{"derivedFrom":makeQuery(id+"F59.opExtrude","SWEPT_EDGE",EDGE,{"disambiguationData":[OSD([sQuery(id+"F58.wireOp",EDGE,"E114"),sQuery(id+"F58.wireOp",EDGE,"E115")])]})});
            var Q3;
            Q3=makeQuery(id+"F59.boolean.opBoolean","COPY",EDGE,{"derivedFrom":makeQuery(id+"F59.opExtrude","SWEPT_EDGE",EDGE,{"disambiguationData":[OSD([sQuery(id+"F58.wireOp",EDGE,"E110.bottom"),sQuery(id+"F58.wireOp",EDGE,"E110.right")])]})});
            var Q4;
            Q4=makeQuery(id+"F59.boolean.opBoolean","COPY",EDGE,{"derivedFrom":makeQuery(id+"F59.opExtrude","SWEPT_EDGE",EDGE,{"disambiguationData":[OSD([sQuery(id+"F58.wireOp",EDGE,"E110.top"),sQuery(id+"F58.wireOp",EDGE,"E110.right")])]})});
            var Q5;
            Q5=makeQuery(id+"F59.boolean.opBoolean","COPY",EDGE,{"derivedFrom":makeQuery(id+"F59.opExtrude","SWEPT_EDGE",EDGE,{"disambiguationData":[OSD([sQuery(id+"F58.wireOp",EDGE,"E109.top"),sQuery(id+"F58.wireOp",EDGE,"E109.left")])]})});
            var Q6;
            Q6=makeQuery(id+"F59.boolean.opBoolean","COPY",EDGE,{"derivedFrom":makeQuery(id+"F59.opExtrude","SWEPT_EDGE",EDGE,{"disambiguationData":[OSD([sQuery(id+"F58.wireOp",EDGE,"E108.top"),sQuery(id+"F58.wireOp",EDGE,"E108.right")])]})});
            var Q7;
            Q7=makeQuery(id+"F59.boolean.opBoolean","COPY",EDGE,{"derivedFrom":makeQuery(id+"F59.opExtrude","SWEPT_EDGE",EDGE,{"disambiguationData":[OSD([sQuery(id+"F58.wireOp",EDGE,"E108.bottom"),sQuery(id+"F58.wireOp",EDGE,"E108.right")])]})});
            var Q8;
            Q8=makeQuery(id+"F59.boolean.opBoolean","COPY",EDGE,{"derivedFrom":makeQuery(id+"F59.opExtrude","SWEPT_EDGE",EDGE,{"disambiguationData":[OSD([sQuery(id+"F58.wireOp",EDGE,"E109.bottom"),sQuery(id+"F58.wireOp",EDGE,"E109.left")])]})});
            var Q9;
            Q9=makeQuery(id+"F59.boolean.opBoolean","COPY",EDGE,{"derivedFrom":makeQuery(id+"F59.opExtrude","SWEPT_EDGE",EDGE,{"disambiguationData":[OSD([sQuery(id+"F58.wireOp",EDGE,"E108.bottom"),sQuery(id+"F58.wireOp",EDGE,"E108.left")])]})});
            var Q10;
            Q10=makeQuery(id+"F59.boolean.opBoolean","COPY",EDGE,{"derivedFrom":makeQuery(id+"F59.opExtrude","SWEPT_EDGE",EDGE,{"disambiguationData":[OSD([sQuery(id+"F58.wireOp",EDGE,"E110.bottom"),sQuery(id+"F58.wireOp",EDGE,"E110.left")])]})});
            var Q11;
            Q11=makeQuery(id+"F59.boolean.opBoolean","COPY",EDGE,{"derivedFrom":makeQuery(id+"F59.opExtrude","SWEPT_EDGE",EDGE,{"disambiguationData":[OSD([sQuery(id+"F58.wireOp",EDGE,"E110.top"),sQuery(id+"F58.wireOp",EDGE,"E110.left")])]})});
            var Q12;
            Q12=makeQuery(id+"F59.boolean.opBoolean","COPY",EDGE,{"derivedFrom":makeQuery(id+"F59.opExtrude","SWEPT_EDGE",EDGE,{"disambiguationData":[OSD([sQuery(id+"F58.wireOp",EDGE,"E108.top"),sQuery(id+"F58.wireOp",EDGE,"E108.left")])]})});
            var Q13;
            Q13=makeQuery(id+"F59.boolean.opBoolean","COPY",EDGE,{"derivedFrom":makeQuery(id+"F59.opExtrude","SWEPT_EDGE",EDGE,{"disambiguationData":[OSD([sQuery(id+"F58.wireOp",EDGE,"E109.top"),sQuery(id+"F58.wireOp",EDGE,"E109.right")])]})});
            var Q14;
            Q14=makeQuery(id+"F59.boolean.opBoolean","COPY",EDGE,{"derivedFrom":makeQuery(id+"F59.opExtrude","SWEPT_EDGE",EDGE,{"disambiguationData":[OSD([sQuery(id+"F58.wireOp",EDGE,"E109.bottom"),sQuery(id+"F58.wireOp",EDGE,"E109.right")])]})});
            var Q15;
            Q15=makeQuery(id+"F59.boolean.opBoolean","COPY",EDGE,{"derivedFrom":makeQuery(id+"F59.opExtrude","SWEPT_EDGE",EDGE,{"disambiguationData":[OSD([sQuery(id+"F58.wireOp",EDGE,"E112"),sQuery(id+"F58.wireOp",EDGE,"E113")])]})});
            var Q16;
            Q16=makeQuery(id+"F59.boolean.opBoolean","COPY",EDGE,{"derivedFrom":makeQuery(id+"F59.opExtrude","SWEPT_EDGE",EDGE,{"disambiguationData":[OSD([sQuery(id+"F58.wireOp",EDGE,"E111"),sQuery(id+"F58.wireOp",EDGE,"E112")])]})});
            var Q17;
            Q17=makeQuery(id+"F59.boolean.opBoolean","COPY",EDGE,{"derivedFrom":makeQuery(id+"F59.opExtrude","SWEPT_EDGE",EDGE,{"disambiguationData":[OSD([sQuery(id+"F58.wireOp",EDGE,"E111"),sQuery(id+"F58.wireOp",EDGE,"E113")])]})});
            fillet(context, id + "F60", {"entities" : qUnion([Q0, Q1, Q2, Q3, Q4, Q5, Q6, Q7, Q8, Q9, Q10, Q11, Q12, Q13, Q14, Q15, Q16, Q17]), "radius" : 0.25 * mm, "tangentPropagation" : true, "allowEdgeOverflow" : false});
        }
        {
            var Q0;
            Q0=makeQuery(id+"F37.boolean.opBoolean","MERGE",FACE,{"derivedFrom":[makeQuery(id+"F36.boolean.opBoolean","MERGE",FACE,{"derivedFrom":[makeQuery(id+"F1.opExtrude","CAP_FACE",FACE,{"disambiguationData":[OSD([sQuery(id+"F0.wireOp",EDGE,"E0.bottom"),sQuery(id+"F0.wireOp",EDGE,"E0.top"),sQuery(id+"F0.wireOp",EDGE,"E0.left"),sQuery(id+"F0.wireOp",EDGE,"E0.right")])],"isStart":false}),makeQuery(id+"F36.opExtrude","SWEPT_FACE",FACE,{"disambiguationData":[OSD([sQuery(id+"F26.wireOp",EDGE,"E60.top"),sQuery(id+"F35.wireOp",EDGE,"E78")])]})]}),makeQuery(id+"F37.opExtrude","SWEPT_FACE",FACE,{"disambiguationData":[OSD([sQuery(id+"F21.wireOp",EDGE,"E56.top"),sQuery(id+"F34.wireOp",EDGE,"E70")])]})]});
            var sketch = newSketch(context, id + "F61", { "sketchPlane" : qUnion([Q0])});
            skCircle(sketch, "E117", {"center": v(-57.47, -40.58) * mm, "radius": 3.18 * mm});
            skCircle(sketch, "E118", {"center": v(23.9, -43.74) * mm, "radius": 1.59 * mm});
            skCircle(sketch, "E119", {"center": v(39.23, -43.74) * mm, "radius": 1.59 * mm});
            skCircle(sketch, "E120", {"center": v(86.86, -43.74) * mm, "radius": 1.59 * mm});
            skCircle(sketch, "E121", {"center": v(147.88, -38.74) * mm, "radius": 1.59 * mm});
            skCircle(sketch, "E122", {"center": v(-10.07, 43.74) * mm, "radius": 1.59 * mm});
            skCircle(sketch, "E123", {"center": v(5.5, 43.74) * mm, "radius": 1.59 * mm});
            skCircle(sketch, "E124", {"center": v(63.08, 43.74) * mm, "radius": 1.59 * mm});
            skCircle(sketch, "E125", {"center": v(-109, 43.74) * mm, "radius": 1.59 * mm});
            skPoint(sketch, "E125.centerSnap0", {"position": v(-109, 38.98) * mm});
            skSolve(sketch);
        }
        {
            var Q0;
            Q0=makeQuery(id+"F61.imprint","IMPRINT",FACE,{"disambiguationData":[TD([[makeQuery(id+"F61.imprint","IMPRINT",EDGE,{"derivedFrom":sQuery(id+"F61.wireOp",EDGE,"E125")}),1.0]])]});
            var Q1;
            Q1=makeQuery(id+"F61.imprint","IMPRINT",FACE,{"disambiguationData":[TD([[makeQuery(id+"F61.imprint","IMPRINT",EDGE,{"derivedFrom":sQuery(id+"F61.wireOp",EDGE,"E122")}),1.0]])]});
            var Q2;
            Q2=makeQuery(id+"F61.imprint","IMPRINT",FACE,{"disambiguationData":[TD([[makeQuery(id+"F61.imprint","IMPRINT",EDGE,{"derivedFrom":sQuery(id+"F61.wireOp",EDGE,"E123")}),1.0]])]});
            var Q3;
            Q3=makeQuery(id+"F61.imprint","IMPRINT",FACE,{"disambiguationData":[TD([[makeQuery(id+"F61.imprint","IMPRINT",EDGE,{"derivedFrom":sQuery(id+"F61.wireOp",EDGE,"E117")}),1.0]])]});
            var Q4;
            Q4=makeQuery(id+"F61.imprint","IMPRINT",FACE,{"disambiguationData":[TD([[makeQuery(id+"F61.imprint","IMPRINT",EDGE,{"derivedFrom":sQuery(id+"F61.wireOp",EDGE,"E118")}),1.0]])]});
            var Q5;
            Q5=makeQuery(id+"F61.imprint","IMPRINT",FACE,{"disambiguationData":[TD([[makeQuery(id+"F61.imprint","IMPRINT",EDGE,{"derivedFrom":sQuery(id+"F61.wireOp",EDGE,"E119")}),1.0]])]});
            var Q6;
            Q6=makeQuery(id+"F61.imprint","IMPRINT",FACE,{"disambiguationData":[TD([[makeQuery(id+"F61.imprint","IMPRINT",EDGE,{"derivedFrom":sQuery(id+"F61.wireOp",EDGE,"E120")}),1.0]])]});
            var Q7;
            Q7=makeQuery(id+"F61.imprint","IMPRINT",FACE,{"disambiguationData":[TD([[makeQuery(id+"F61.imprint","IMPRINT",EDGE,{"derivedFrom":sQuery(id+"F61.wireOp",EDGE,"E124")}),1.0]])]});
            var Q8;
            Q8=makeQuery(id+"F61.imprint","IMPRINT",FACE,{"disambiguationData":[TD([[makeQuery(id+"F61.imprint","IMPRINT",EDGE,{"derivedFrom":sQuery(id+"F61.wireOp",EDGE,"E121")}),1.0]])]});
            extrude(context, id + "F62", {"entities" : qUnion([Q0, Q1, Q2, Q3, Q4, Q5, Q6, Q7, Q8]), "operationType" : NewBodyOperationType.REMOVE, "oppositeDirection" : true, "depth" : 0.4 * mm, "offsetDistance" : 25.4 * mm});
        }
        {
            var Q0;
            {var subQ0=sQuery(id+"F0.wireOp",EDGE,"E0.bottom");Q0=makeQuery(id+"F5.boolean.opBoolean","MERGE",FACE,{"derivedFrom":[makeQuery(id+"F1.opExtrude","SWEPT_FACE",FACE,{"disambiguationData":[OSD([subQ0])]}),makeQuery(id+"F5.opExtrude","SWEPT_FACE",FACE,{"disambiguationData":[OSD([subQ0])]})]});}
            var sketch = newSketch(context, id + "F63", { "sketchPlane" : qUnion([Q0])});
            skLineSegment(sketch, "E126.bottom", {"start": v(-8.04, 12.7) * mm, "end": v(-1.7, 12.7) * mm});
            skLineSegment(sketch, "E126.top", {"start": v(-8.04, 9.53) * mm, "end": v(-1.7, 9.53) * mm});
            skLineSegment(sketch, "E126.left", {"start": v(-8.04, 12.7) * mm, "end": v(-8.04, 9.53) * mm});
            skLineSegment(sketch, "E126.right", {"start": v(-1.7, 12.7) * mm, "end": v(-1.7, 9.53) * mm});
            skSolve(sketch);
        }
        {
            var Q0;
            Q0=makeQuery(id+"F63.imprint","IMPRINT",FACE,{"disambiguationData":[TD([[makeQuery(id+"F63.imprint","IMPRINT",EDGE,{"derivedFrom":sQuery(id+"F63.wireOp",EDGE,"E126.bottom")}),1.0]])]});
            extrude(context, id + "F64", {"entities" : qUnion([Q0]), "operationType" : NewBodyOperationType.REMOVE, "oppositeDirection" : true, "depth" : 2.54 * mm, "offsetDistance" : 25.4 * mm});
        }
        {
            var Q0;
            {var subQ0=sQuery(id+"F0.wireOp",EDGE,"E0.top");Q0=makeQuery(id+"F5.boolean.opBoolean","MERGE",FACE,{"derivedFrom":[makeQuery(id+"F1.opExtrude","SWEPT_FACE",FACE,{"disambiguationData":[OSD([subQ0])]}),makeQuery(id+"F5.opExtrude","SWEPT_FACE",FACE,{"disambiguationData":[OSD([subQ0])]})]});}
            var sketch = newSketch(context, id + "F65", { "sketchPlane" : qUnion([Q0])});
            skLineSegment(sketch, "E127.bottom", {"start": v(4.01, 12.7) * mm, "end": v(0.84, 12.7) * mm});
            skLineSegment(sketch, "E127.top", {"start": v(4.01, 0) * mm, "end": v(0.84, 0) * mm});
            skLineSegment(sketch, "E127.left", {"start": v(4.01, 12.7) * mm, "end": v(4.01, 0) * mm});
            skLineSegment(sketch, "E127.right", {"start": v(0.84, 12.7) * mm, "end": v(0.84, 0) * mm});
            skSolve(sketch);
        }
        {
            var Q0;
            Q0=makeQuery(id+"F65.imprint","IMPRINT",FACE,{"disambiguationData":[TD([[makeQuery(id+"F65.imprint","IMPRINT",EDGE,{"derivedFrom":sQuery(id+"F65.wireOp",EDGE,"E127.bottom")}),-1.0]])]});
            extrude(context, id + "F66", {"entities" : qUnion([Q0]), "operationType" : NewBodyOperationType.REMOVE, "oppositeDirection" : true, "depth" : 1.27 * mm, "offsetDistance" : 25.4 * mm});
        }
        {
            var Q0;
            {var subQ0=sQuery(id+"F0.wireOp",EDGE,"E0.left");Q0=makeQuery(id+"F5.boolean.opBoolean","MERGE",FACE,{"derivedFrom":[makeQuery(id+"F1.opExtrude","SWEPT_FACE",FACE,{"disambiguationData":[OSD([subQ0])]}),makeQuery(id+"F5.opExtrude","SWEPT_FACE",FACE,{"disambiguationData":[OSD([subQ0])]})]});}
            var sketch = newSketch(context, id + "F67", { "sketchPlane" : qUnion([Q0])});
            skLineSegment(sketch, "E128.top", {"start": v(3.18, 9.53) * mm, "end": v(-3.17, 9.53) * mm});
            skLineSegment(sketch, "E128.left", {"start": v(3.18, 15.88) * mm, "end": v(3.18, 9.53) * mm});
            skLineSegment(sketch, "E128.right", {"start": v(-3.17, 15.88) * mm, "end": v(-3.17, 9.53) * mm});
            skPoint(sketch, "E128.middle", {"position": v(0, 12.7) * mm});
            skSolve(sketch);
        }
        {
            var Q0;
            {var subQ0=sQuery(id+"F67.wireOp",EDGE,"E128.bottom");Q0=makeQuery(id+"F67.imprint","IMPRINT",FACE,{"disambiguationData":[TD([[makeQuery(id+"F67.imprint","IMPRINT",EDGE,{"derivedFrom":subQ0}),1.0]])]});}
            var Q1;
            {var subQ0=sQuery(id+"F67.wireOp",EDGE,"E128.top");Q1=makeQuery(id+"F67.imprint","IMPRINT",FACE,{"disambiguationData":[TD([[makeQuery(id+"F67.imprint","IMPRINT",EDGE,{"derivedFrom":subQ0}),-1.0]])]});}
            extrude(context, id + "F68", {"entities" : qUnion([Q0, Q1]), "operationType" : NewBodyOperationType.REMOVE, "endBound" : BoundingType.THROUGH_ALL, "oppositeDirection" : true, "depth" : 25.4 * mm, "offsetDistance" : 25.4 * mm});
        }
        {
            var Q0;
            {var subQ7=sQuery(id+"F0.wireOp",EDGE,"E0.top");Q0=makeQuery(id+"F66.boolean.opBoolean","SPLIT",FACE,{"disambiguationData":[TD([makeQuery(id+"F66.opExtrude","SWEPT_FACE",FACE,{"disambiguationData":[OSD([sQuery(id+"F65.wireOp",EDGE,"E127.left")])]})])],"derivedFrom":makeQuery(id+"F5.boolean.opBoolean","MERGE",FACE,{"derivedFrom":[makeQuery(id+"F1.opExtrude","SWEPT_FACE",FACE,{"disambiguationData":[OSD([subQ7])]}),makeQuery(id+"F5.opExtrude","SWEPT_FACE",FACE,{"disambiguationData":[OSD([subQ7])]})]})});}
            var sketch = newSketch(context, id + "F69", { "sketchPlane" : qUnion([Q0])});
            skLineSegment(sketch, "E129.bottom", {"start": v(132.57, 11.1) * mm, "end": v(140.5, 11.1) * mm});
            skLineSegment(sketch, "E129.top", {"start": v(132.57, 0) * mm, "end": v(140.5, 0) * mm});
            skLineSegment(sketch, "E129.left", {"start": v(132.57, 11.1) * mm, "end": v(132.57, 0) * mm});
            skLineSegment(sketch, "E129.right", {"start": v(140.5, 11.1) * mm, "end": v(140.5, 0) * mm});
            skLineSegment(sketch, "E130.bottom", {"start": v(55.43, 11.1) * mm, "end": v(63.37, 11.1) * mm});
            skLineSegment(sketch, "E130.top", {"start": v(55.43, 0) * mm, "end": v(63.37, 0) * mm});
            skLineSegment(sketch, "E130.left", {"start": v(55.43, 11.1) * mm, "end": v(55.43, 0) * mm});
            skLineSegment(sketch, "E130.right", {"start": v(63.37, 11.1) * mm, "end": v(63.37, 0) * mm});
            skLineSegment(sketch, "E131.bottom", {"start": v(-91.79, 11.1) * mm, "end": v(-83.85, 11.1) * mm});
            skLineSegment(sketch, "E131.top", {"start": v(-91.79, 0) * mm, "end": v(-83.85, 0) * mm});
            skLineSegment(sketch, "E131.left", {"start": v(-91.79, 11.1) * mm, "end": v(-91.79, 0) * mm});
            skLineSegment(sketch, "E131.right", {"start": v(-83.85, 11.1) * mm, "end": v(-83.85, 0) * mm});
            skLineSegment(sketch, "E132.bottom", {"start": v(-114.17, 11.1) * mm, "end": v(-106.23, 11.1) * mm});
            skLineSegment(sketch, "E132.top", {"start": v(-114.17, 0) * mm, "end": v(-106.23, 0) * mm});
            skLineSegment(sketch, "E132.left", {"start": v(-114.17, 11.1) * mm, "end": v(-114.17, 0) * mm});
            skLineSegment(sketch, "E132.right", {"start": v(-106.23, 11.1) * mm, "end": v(-106.23, 0) * mm});
            skSolve(sketch);
        }
        {
            var Q0;
            Q0=makeQuery(id+"F69.imprint","IMPRINT",FACE,{"disambiguationData":[TD([[makeQuery(id+"F69.imprint","IMPRINT",EDGE,{"derivedFrom":sQuery(id+"F69.wireOp",EDGE,"E132.bottom")}),-1.0]])]});
            var Q1;
            Q1=makeQuery(id+"F69.imprint","IMPRINT",FACE,{"disambiguationData":[TD([[makeQuery(id+"F69.imprint","IMPRINT",EDGE,{"derivedFrom":sQuery(id+"F69.wireOp",EDGE,"E131.bottom")}),-1.0]])]});
            var Q2;
            Q2=makeQuery(id+"F69.imprint","IMPRINT",FACE,{"disambiguationData":[TD([[makeQuery(id+"F69.imprint","IMPRINT",EDGE,{"derivedFrom":sQuery(id+"F69.wireOp",EDGE,"E130.bottom")}),-1.0]])]});
            var Q3;
            Q3=makeQuery(id+"F69.imprint","IMPRINT",FACE,{"disambiguationData":[TD([[makeQuery(id+"F69.imprint","IMPRINT",EDGE,{"derivedFrom":sQuery(id+"F69.wireOp",EDGE,"E129.bottom")}),-1.0]])]});
            extrude(context, id + "F70", {"entities" : qUnion([Q0, Q1, Q2, Q3]), "operationType" : NewBodyOperationType.REMOVE, "oppositeDirection" : true, "depth" : 1.6 * mm, "offsetDistance" : 25.4 * mm});
        }
        {
            var Q0;
            Q0=makeQuery(id+"F70.boolean.opBoolean","COPY",EDGE,{"derivedFrom":makeQuery(id+"F70.opExtrude","CAP_EDGE",EDGE,{"disambiguationData":[OSD([sQuery(id+"F69.wireOp",EDGE,"E132.left")])],"isStart":false})});
            var Q1;
            Q1=makeQuery(id+"F70.boolean.opBoolean","COPY",EDGE,{"derivedFrom":makeQuery(id+"F70.opExtrude","CAP_EDGE",EDGE,{"disambiguationData":[OSD([sQuery(id+"F69.wireOp",EDGE,"E131.left")])],"isStart":false})});
            var Q2;
            Q2=makeQuery(id+"F70.boolean.opBoolean","COPY",EDGE,{"derivedFrom":makeQuery(id+"F70.opExtrude","CAP_EDGE",EDGE,{"disambiguationData":[OSD([sQuery(id+"F69.wireOp",EDGE,"E130.left")])],"isStart":false})});
            var Q3;
            Q3=makeQuery(id+"F70.boolean.opBoolean","COPY",EDGE,{"derivedFrom":makeQuery(id+"F70.opExtrude","CAP_EDGE",EDGE,{"disambiguationData":[OSD([sQuery(id+"F69.wireOp",EDGE,"E129.left")])],"isStart":false})});
            var Q4;
            Q4=makeQuery(id+"F70.boolean.opBoolean","COPY",EDGE,{"derivedFrom":makeQuery(id+"F70.opExtrude","CAP_EDGE",EDGE,{"disambiguationData":[OSD([sQuery(id+"F69.wireOp",EDGE,"E129.right")])],"isStart":false})});
            var Q5;
            Q5=makeQuery(id+"F70.boolean.opBoolean","COPY",EDGE,{"derivedFrom":makeQuery(id+"F70.opExtrude","CAP_EDGE",EDGE,{"disambiguationData":[OSD([sQuery(id+"F69.wireOp",EDGE,"E130.right")])],"isStart":false})});
            var Q6;
            Q6=makeQuery(id+"F70.boolean.opBoolean","COPY",EDGE,{"derivedFrom":makeQuery(id+"F70.opExtrude","CAP_EDGE",EDGE,{"disambiguationData":[OSD([sQuery(id+"F69.wireOp",EDGE,"E131.right")])],"isStart":false})});
            var Q7;
            Q7=makeQuery(id+"F70.boolean.opBoolean","COPY",EDGE,{"derivedFrom":makeQuery(id+"F70.opExtrude","CAP_EDGE",EDGE,{"disambiguationData":[OSD([sQuery(id+"F69.wireOp",EDGE,"E132.right")])],"isStart":false})});
            chamfer(context, id + "F71", {"entities" : qUnion([Q0, Q1, Q2, Q3, Q4, Q5, Q6, Q7]), "width" : 1.6 * mm, "tangentPropagation" : true});
        }
        {
            var Q0;
            {var subQ7=sQuery(id+"F0.wireOp",EDGE,"E0.top");Q0=makeQuery(id+"F66.boolean.opBoolean","SPLIT",FACE,{"disambiguationData":[TD([makeQuery(id+"F66.opExtrude","SWEPT_FACE",FACE,{"disambiguationData":[OSD([sQuery(id+"F65.wireOp",EDGE,"E127.left")])]})])],"derivedFrom":makeQuery(id+"F5.boolean.opBoolean","MERGE",FACE,{"derivedFrom":[makeQuery(id+"F1.opExtrude","SWEPT_FACE",FACE,{"disambiguationData":[OSD([subQ7])]}),makeQuery(id+"F5.opExtrude","SWEPT_FACE",FACE,{"disambiguationData":[OSD([subQ7])]})]})});}
            var sketch = newSketch(context, id + "F72", { "sketchPlane" : qUnion([Q0])});
            skCircle(sketch, "E133", {"center": v(148.63, 3.96) * mm, "radius": 3.3 * mm});
            skCircle(sketch, "E134", {"center": v(47.74, 3.96) * mm, "radius": 3.3 * mm});
            skCircle(sketch, "E135", {"center": v(-99.24, 3.96) * mm, "radius": 3.3 * mm});
            skSolve(sketch);
        }
        {
            var Q0;
            Q0=makeQuery(id+"F72.imprint","IMPRINT",FACE,{"disambiguationData":[TD([[makeQuery(id+"F72.imprint","IMPRINT",EDGE,{"derivedFrom":sQuery(id+"F72.wireOp",EDGE,"E135")}),1.0]])]});
            var Q1;
            Q1=makeQuery(id+"F72.imprint","IMPRINT",FACE,{"disambiguationData":[TD([[makeQuery(id+"F72.imprint","IMPRINT",EDGE,{"derivedFrom":sQuery(id+"F72.wireOp",EDGE,"E134")}),1.0]])]});
            var Q2;
            Q2=makeQuery(id+"F72.imprint","IMPRINT",FACE,{"disambiguationData":[TD([[makeQuery(id+"F72.imprint","IMPRINT",EDGE,{"derivedFrom":sQuery(id+"F72.wireOp",EDGE,"E133")}),1.0]])]});
            extrude(context, id + "F73", {"entities" : qUnion([Q0, Q1, Q2]), "operationType" : NewBodyOperationType.REMOVE, "oppositeDirection" : true, "depth" : 1.52 * mm, "offsetDistance" : 25.4 * mm});
        }
        {
            var Q0;
            Q0=qCreatedBy(makeId("Top.planeOp"),FACE);
            var sketch = newSketch(context, id + "F74", { "sketchPlane" : qUnion([Q0])});
            skLineSegment(sketch, "E136.bottom", {"start": v(166.69, -66.76) * mm, "end": v(-166.69, -66.76) * mm});
            skLineSegment(sketch, "E136.top", {"start": v(166.69, -193.76) * mm, "end": v(-166.69, -193.76) * mm});
            skLineSegment(sketch, "E136.left", {"start": v(166.69, -66.76) * mm, "end": v(166.69, -193.76) * mm});
            skLineSegment(sketch, "E136.right", {"start": v(-166.69, -66.76) * mm, "end": v(-166.69, -193.76) * mm});
            skPoint(sketch, "E136.middle", {"position": v(0, -130.26) * mm});
            skLineSegment(sketch, "E137.bottom", {"start": v(-106.36, -66.76) * mm, "end": v(-90.49, -66.76) * mm});
            skLineSegment(sketch, "E137.top", {"start": v(-106.36, -57.23) * mm, "end": v(-90.49, -57.23) * mm});
            skLineSegment(sketch, "E137.left", {"start": v(-106.36, -66.76) * mm, "end": v(-106.36, -57.23) * mm});
            skLineSegment(sketch, "E137.right", {"start": v(-90.49, -66.76) * mm, "end": v(-90.49, -57.23) * mm});
            skLineSegment(sketch, "E138.bottom", {"start": v(90.49, -66.76) * mm, "end": v(106.36, -66.76) * mm});
            skLineSegment(sketch, "E138.top", {"start": v(90.49, -57.23) * mm, "end": v(106.36, -57.23) * mm});
            skLineSegment(sketch, "E138.left", {"start": v(90.49, -66.76) * mm, "end": v(90.49, -57.23) * mm});
            skLineSegment(sketch, "E138.right", {"start": v(106.36, -66.76) * mm, "end": v(106.36, -57.23) * mm});
            skSolve(sketch);
        }
        {
            var Q0;
            Q0=makeQuery(id+"F74.imprint","IMPRINT",FACE,{"disambiguationData":[TD([[makeQuery(id+"F74.imprint","IMPRINT",EDGE,{"derivedFrom":sQuery(id+"F74.wireOp",EDGE,"E137.top")}),-1.0]])]});
            var Q1;
            Q1=makeQuery(id+"F74.imprint","IMPRINT",FACE,{"disambiguationData":[TD([[makeQuery(id+"F74.imprint","IMPRINT",EDGE,{"derivedFrom":sQuery(id+"F74.wireOp",EDGE,"E138.top")}),-1.0]])]});
            var Q2;
            Q2=makeQuery(id+"F74.imprint","IMPRINT",FACE,{"disambiguationData":[TD([[makeQuery(id+"F74.imprint","IMPRINT",EDGE,{"derivedFrom":sQuery(id+"F74.wireOp",EDGE,"E136.top")}),-1.0]])]});
            extrude(context, id + "F75", {"entities" : qUnion([Q0, Q1, Q2]), "depth" : 2.38 * mm, "offsetDistance" : 25.4 * mm});
        }
        {
            var Q0;
            Q0=makeQuery(id+"F75.opExtrude","CAP_FACE",FACE,{"disambiguationData":[OSD([sQuery(id+"F74.wireOp",EDGE,"E136.bottom"),sQuery(id+"F74.wireOp",EDGE,"E136.top"),sQuery(id+"F74.wireOp",EDGE,"E136.left"),sQuery(id+"F74.wireOp",EDGE,"E136.right"),sQuery(id+"F74.wireOp",EDGE,"E137.top"),sQuery(id+"F74.wireOp",EDGE,"E137.left"),sQuery(id+"F74.wireOp",EDGE,"E137.right"),sQuery(id+"F74.wireOp",EDGE,"E138.top"),sQuery(id+"F74.wireOp",EDGE,"E138.left"),sQuery(id+"F74.wireOp",EDGE,"E138.right")])],"isStart":false});
            var sketch = newSketch(context, id + "F76", { "sketchPlane" : qUnion([Q0])});
            skPoint(sketch, "E139.oppositeSnap0", {"position": v(-90.49, -62) * mm});
            skLineSegment(sketch, "E139.bottom", {"start": v(-106.36, -57.23) * mm, "end": v(-90.49, -57.23) * mm});
            skLineSegment(sketch, "E139.top", {"start": v(-106.36, -73.1) * mm, "end": v(-90.49, -73.1) * mm});
            skLineSegment(sketch, "E139.left", {"start": v(-106.36, -57.23) * mm, "end": v(-106.36, -73.1) * mm});
            skLineSegment(sketch, "E139.right", {"start": v(-90.49, -57.23) * mm, "end": v(-90.49, -73.1) * mm});
            skLineSegment(sketch, "E140.bottom", {"start": v(106.36, -57.23) * mm, "end": v(90.49, -57.23) * mm});
            skLineSegment(sketch, "E140.top", {"start": v(106.36, -73.1) * mm, "end": v(90.49, -73.1) * mm});
            skLineSegment(sketch, "E140.left", {"start": v(106.36, -57.23) * mm, "end": v(106.36, -73.1) * mm});
            skLineSegment(sketch, "E140.right", {"start": v(90.49, -57.23) * mm, "end": v(90.49, -73.1) * mm});
            skLineSegment(sketch, "E141", {"start": v(92.07, -73.1) * mm, "end": v(92.07, -62) * mm});
            skLineSegment(sketch, "E142", {"start": v(92.07, -62) * mm, "end": v(93.66, -62) * mm});
            skLineSegment(sketch, "E143", {"start": v(93.66, -62) * mm, "end": v(93.66, -70.72) * mm});
            skLineSegment(sketch, "E144", {"start": v(93.66, -70.72) * mm, "end": v(103.19, -70.72) * mm});
            skLineSegment(sketch, "E145", {"start": v(103.19, -70.72) * mm, "end": v(103.19, -62) * mm});
            skLineSegment(sketch, "E146", {"start": v(103.19, -62) * mm, "end": v(104.77, -62) * mm});
            skLineSegment(sketch, "E147", {"start": v(104.77, -62) * mm, "end": v(104.77, -73.1) * mm});
            skLineSegment(sketch, "E148", {"start": v(-104.76, -73.1) * mm, "end": v(-104.76, -62) * mm});
            skLineSegment(sketch, "E149", {"start": v(-104.76, -62) * mm, "end": v(-103.16, -62) * mm});
            skLineSegment(sketch, "E150", {"start": v(-103.16, -62) * mm, "end": v(-103.16, -70.72) * mm});
            skLineSegment(sketch, "E151", {"start": v(-103.16, -70.72) * mm, "end": v(-93.69, -70.72) * mm});
            skLineSegment(sketch, "E152", {"start": v(-93.69, -70.72) * mm, "end": v(-93.69, -62) * mm});
            skLineSegment(sketch, "E153", {"start": v(-93.69, -62) * mm, "end": v(-92.09, -62) * mm});
            skLineSegment(sketch, "E154", {"start": v(-92.09, -62) * mm, "end": v(-92.09, -73.1) * mm});
            skSolve(sketch);
        }
        {
            var Q0;
            {var subQ9=sQuery(id+"F76.wireOp",EDGE,"E139.bottom");Q0=makeQuery(id+"F76.imprint","IMPRINT",FACE,{"disambiguationData":[TD([[makeQuery(id+"F76.imprint","IMPRINT",EDGE,{"derivedFrom":subQ9}),-1.0]])]});}
            var Q1;
            {var subQ7=sQuery(id+"F76.wireOp",EDGE,"E140.bottom");Q1=makeQuery(id+"F76.imprint","IMPRINT",FACE,{"disambiguationData":[TD([[makeQuery(id+"F76.imprint","IMPRINT",EDGE,{"derivedFrom":subQ7}),-1.0]])]});}
            extrude(context, id + "F77", {"entities" : qUnion([Q0, Q1]), "operationType" : NewBodyOperationType.ADD, "depth" : 1.59 * mm, "offsetDistance" : 25.4 * mm});
        }
        {
            var Q0;
            Q0=makeQuery(id+"F77.opExtrude","CAP_EDGE",EDGE,{"disambiguationData":[OSD([sQuery(id+"F76.wireOp",EDGE,"E151")])],"isStart":false});
            var Q1;
            Q1=makeQuery(id+"F77.opExtrude","CAP_EDGE",EDGE,{"disambiguationData":[OSD([sQuery(id+"F76.wireOp",EDGE,"E144")])],"isStart":false});
            var Q2;
            Q2=makeQuery(id+"F77.opExtrude","CAP_EDGE",EDGE,{"disambiguationData":[OSD([sQuery(id+"F76.wireOp",EDGE,"E142")])],"isStart":true});
            var Q3;
            Q3=makeQuery(id+"F77.opExtrude","CAP_EDGE",EDGE,{"disambiguationData":[OSD([sQuery(id+"F76.wireOp",EDGE,"E146")])],"isStart":true});
            var Q4;
            Q4=makeQuery(id+"F77.opExtrude","CAP_EDGE",EDGE,{"disambiguationData":[OSD([sQuery(id+"F76.wireOp",EDGE,"E153")])],"isStart":true});
            var Q5;
            Q5=makeQuery(id+"F77.opExtrude","CAP_EDGE",EDGE,{"disambiguationData":[OSD([sQuery(id+"F76.wireOp",EDGE,"E149")])],"isStart":true});
            chamfer(context, id + "F78", {"entities" : qUnion([Q0, Q1, Q2, Q3, Q4, Q5]), "width" : 1.65 * mm, "tangentPropagation" : true});
        }
        {
            var Q0;
            Q0=makeQuery(id+"F77.boolean.opBoolean","MERGE",EDGE,{"derivedFrom":[makeQuery(id+"F75.opExtrude","SWEPT_EDGE",EDGE,{"disambiguationData":[OSD([sQuery(id+"F74.wireOp",EDGE,"E137.top"),sQuery(id+"F74.wireOp",EDGE,"E137.left")])]}),makeQuery(id+"F77.opExtrude","SWEPT_EDGE",EDGE,{"disambiguationData":[OSD([sQuery(id+"F76.wireOp",EDGE,"E139.bottom"),sQuery(id+"F76.wireOp",EDGE,"E139.left")])]})]});
            var Q1;
            Q1=makeQuery(id+"F77.boolean.opBoolean","MERGE",EDGE,{"derivedFrom":[makeQuery(id+"F75.opExtrude","SWEPT_EDGE",EDGE,{"disambiguationData":[OSD([sQuery(id+"F74.wireOp",EDGE,"E137.top"),sQuery(id+"F74.wireOp",EDGE,"E137.right")])]}),makeQuery(id+"F77.opExtrude","SWEPT_EDGE",EDGE,{"disambiguationData":[OSD([sQuery(id+"F76.wireOp",EDGE,"E139.bottom"),sQuery(id+"F76.wireOp",EDGE,"E139.right")])]})]});
            var Q2;
            Q2=makeQuery(id+"F77.boolean.opBoolean","MERGE",EDGE,{"derivedFrom":[makeQuery(id+"F75.opExtrude","SWEPT_EDGE",EDGE,{"disambiguationData":[OSD([sQuery(id+"F74.wireOp",EDGE,"E138.top"),sQuery(id+"F74.wireOp",EDGE,"E138.right")])]}),makeQuery(id+"F77.opExtrude","SWEPT_EDGE",EDGE,{"disambiguationData":[OSD([sQuery(id+"F76.wireOp",EDGE,"E140.bottom"),sQuery(id+"F76.wireOp",EDGE,"E140.left")])]})]});
            var Q3;
            Q3=makeQuery(id+"F77.boolean.opBoolean","MERGE",EDGE,{"derivedFrom":[makeQuery(id+"F75.opExtrude","SWEPT_EDGE",EDGE,{"disambiguationData":[OSD([sQuery(id+"F74.wireOp",EDGE,"E138.top"),sQuery(id+"F74.wireOp",EDGE,"E138.left")])]}),makeQuery(id+"F77.opExtrude","SWEPT_EDGE",EDGE,{"disambiguationData":[OSD([sQuery(id+"F76.wireOp",EDGE,"E140.bottom"),sQuery(id+"F76.wireOp",EDGE,"E140.right")])]})]});
            chamfer(context, id + "F79", {"entities" : qUnion([Q0, Q1, Q2, Q3]), "width" : 1.9 * mm, "tangentPropagation" : true});
        }
        {
            var Q0;
            Q0=makeQuery(id+"F77.opExtrude","CAP_FACE",FACE,{"disambiguationData":[OSD([sQuery(id+"F76.wireOp",EDGE,"E139.bottom"),sQuery(id+"F76.wireOp",EDGE,"E139.top"),sQuery(id+"F76.wireOp",EDGE,"E139.left"),sQuery(id+"F76.wireOp",EDGE,"E139.right"),sQuery(id+"F76.wireOp",EDGE,"E148"),sQuery(id+"F76.wireOp",EDGE,"E149"),sQuery(id+"F76.wireOp",EDGE,"E150"),sQuery(id+"F76.wireOp",EDGE,"E151"),sQuery(id+"F76.wireOp",EDGE,"E152"),sQuery(id+"F76.wireOp",EDGE,"E153"),sQuery(id+"F76.wireOp",EDGE,"E154")])],"isStart":false});
            var sketch = newSketch(context, id + "F80", { "sketchPlane" : qUnion([Q0])});
            skCircle(sketch, "E155", {"center": v(-98.43, -62.8) * mm, "radius": 2.39 * mm});
            skSolve(sketch);
        }
        {
            var Q0;
            Q0=makeQuery(id+"F80.imprint","IMPRINT",FACE,{"disambiguationData":[TD([[makeQuery(id+"F80.imprint","IMPRINT",EDGE,{"derivedFrom":sQuery(id+"F80.wireOp",EDGE,"E155")}),1.0]])]});
            extrude(context, id + "F81", {"entities" : qUnion([Q0]), "operationType" : NewBodyOperationType.REMOVE, "endBound" : BoundingType.THROUGH_ALL, "oppositeDirection" : true, "depth" : 25.4 * mm, "offsetDistance" : 25.4 * mm});
        }
        {
            var Q0;
            Q0=makeQuery(id+"F77.opExtrude","CAP_FACE",FACE,{"disambiguationData":[OSD([sQuery(id+"F76.wireOp",EDGE,"E140.bottom"),sQuery(id+"F76.wireOp",EDGE,"E140.top"),sQuery(id+"F76.wireOp",EDGE,"E140.left"),sQuery(id+"F76.wireOp",EDGE,"E140.right"),sQuery(id+"F76.wireOp",EDGE,"E141"),sQuery(id+"F76.wireOp",EDGE,"E142"),sQuery(id+"F76.wireOp",EDGE,"E143"),sQuery(id+"F76.wireOp",EDGE,"E144"),sQuery(id+"F76.wireOp",EDGE,"E145"),sQuery(id+"F76.wireOp",EDGE,"E146"),sQuery(id+"F76.wireOp",EDGE,"E147")])],"isStart":false});
            var sketch = newSketch(context, id + "F82", { "sketchPlane" : qUnion([Q0])});
            skCircle(sketch, "E156", {"center": v(98.42, -62.8) * mm, "radius": 2.39 * mm});
            skPoint(sketch, "E156.centerSnap0", {"position": v(98.42, -57.23) * mm});
            skSolve(sketch);
        }
        {
            var Q0;
            Q0=makeQuery(id+"F82.imprint","IMPRINT",FACE,{"disambiguationData":[TD([[makeQuery(id+"F82.imprint","IMPRINT",EDGE,{"derivedFrom":sQuery(id+"F82.wireOp",EDGE,"E156")}),1.0]])]});
            extrude(context, id + "F83", {"entities" : qUnion([Q0]), "operationType" : NewBodyOperationType.REMOVE, "endBound" : BoundingType.THROUGH_ALL, "oppositeDirection" : true, "depth" : 25.4 * mm, "offsetDistance" : 25.4 * mm});
        }
        {
            var Q0;
            Q0=makeQuery(id+"F75.opExtrude","SWEPT_EDGE",EDGE,{"disambiguationData":[OSD([sQuery(id+"F74.wireOp",EDGE,"E136.top"),sQuery(id+"F74.wireOp",EDGE,"E136.right")])]});
            var Q1;
            Q1=makeQuery(id+"F75.opExtrude","SWEPT_EDGE",EDGE,{"disambiguationData":[OSD([sQuery(id+"F74.wireOp",EDGE,"E136.top"),sQuery(id+"F74.wireOp",EDGE,"E136.left")])]});
            fillet(context, id + "F84", {"entities" : qUnion([Q0, Q1]), "radius" : 15.88 * mm, "tangentPropagation" : true, "allowEdgeOverflow" : false});
        }
        {
            var Q0;
            Q0=makeQuery(id+"F75.opExtrude","SWEPT_EDGE",EDGE,{"disambiguationData":[OSD([sQuery(id+"F74.wireOp",EDGE,"E136.bottom"),sQuery(id+"F74.wireOp",EDGE,"E136.right")])]});
            var Q1;
            Q1=makeQuery(id+"F75.opExtrude","SWEPT_EDGE",EDGE,{"disambiguationData":[OSD([sQuery(id+"F74.wireOp",EDGE,"E136.bottom"),sQuery(id+"F74.wireOp",EDGE,"E136.left")])]});
            fillet(context, id + "F85", {"entities" : qUnion([Q0, Q1]), "radius" : 9.52 * mm, "tangentPropagation" : true, "allowEdgeOverflow" : false});
        }
        {
            var Q0;
            Q0=qCreatedBy(makeId("Right.planeOp"),FACE);
            var sketch = newSketch(context, id + "F86", { "sketchPlane" : qUnion([Q0])});
            skLineSegment(sketch, "E157", {"start": v(128.21, 0) * mm, "end": v(242.51, 0) * mm});
            skLineSegment(sketch, "E158", {"start": v(242.51, 0) * mm, "end": v(218.47, 39.26) * mm});
            skLineSegment(sketch, "E159", {"start": v(218.47, 39.26) * mm, "end": v(242.51, 0) * mm, "construction": true});
            skLineSegment(sketch, "E160", {"start": v(218.47, 39.26) * mm, "end": v(128.21, 0) * mm});
            skSolve(sketch);
        }
        {
            var Q0;
            Q0=makeQuery(id+"F86.imprint","IMPRINT",FACE,{"disambiguationData":[TD([[makeQuery(id+"F86.imprint","IMPRINT",EDGE,{"derivedFrom":sQuery(id+"F86.wireOp",EDGE,"E157")}),1.0]])]});
            extrude(context, id + "F87", {"entities" : qUnion([Q0]), "oppositeDirection" : true, "depth" : 323.85 * mm, "offsetDistance" : 25.4 * mm});
        }
        {
            var Q0;
            Q0=makeQuery(id+"F87.opExtrude","CAP_EDGE",EDGE,{"disambiguationData":[OSD([sQuery(id+"F86.wireOp",EDGE,"E158")])],"isStart":true});
            var Q1;
            Q1=makeQuery(id+"F87.opExtrude","CAP_EDGE",EDGE,{"disambiguationData":[OSD([sQuery(id+"F86.wireOp",EDGE,"E158")])],"isStart":false});
            fillet(context, id + "F88", {"entities" : qUnion([Q0, Q1]), "radius" : 9.52 * mm, "tangentPropagation" : true, "allowEdgeOverflow" : false});
        }
        {
            var Q0;
            Q0=makeQuery(id+"F87.opExtrude","SWEPT_FACE",FACE,{"disambiguationData":[OSD([sQuery(id+"F86.wireOp",EDGE,"E158")])]});
            var sketch = newSketch(context, id + "F89", { "sketchPlane" : qUnion([Q0])});
            skLineSegment(sketch, "E161", {"start": v(55.56, -80.62) * mm, "end": v(50.8, -117.13) * mm});
            skLineSegment(sketch, "E162", {"start": v(50.8, -117.13) * mm, "end": v(101.6, -117.13) * mm});
            skLineSegment(sketch, "E163", {"start": v(101.6, -117.13) * mm, "end": v(96.84, -80.62) * mm});
            skLineSegment(sketch, "E164", {"start": v(96.84, -80.62) * mm, "end": v(55.56, -80.62) * mm});
            skLineSegment(sketch, "E165", {"start": v(76.2, -117.13) * mm, "end": v(76.2, -80.62) * mm, "construction": true});
            skLineSegment(sketch, "E166", {"start": v(50.8, -117.13) * mm, "end": v(50.8, -84.8) * mm, "construction": true});
            skLineSegment(sketch, "E167", {"start": v(101.6, -117.13) * mm, "end": v(101.6, -56.53) * mm, "construction": true});
            skLineSegment(sketch, "E168", {"start": v(198.45, -80.62) * mm, "end": v(193.67, -117.13) * mm});
            skLineSegment(sketch, "E169", {"start": v(193.67, -117.13) * mm, "end": v(244.47, -117.13) * mm});
            skLineSegment(sketch, "E170", {"start": v(244.48, -117.13) * mm, "end": v(239.7, -80.62) * mm});
            skLineSegment(sketch, "E171", {"start": v(239.7, -80.62) * mm, "end": v(198.45, -80.62) * mm});
            skLineSegment(sketch, "E172", {"start": v(193.67, -117.13) * mm, "end": v(193.67, -89.33) * mm, "construction": true});
            skLineSegment(sketch, "E173", {"start": v(244.48, -117.13) * mm, "end": v(244.48, -53.54) * mm, "construction": true});
            skLineSegment(sketch, "E174", {"start": v(311.15, -80.62) * mm, "end": v(311.15, -117.13) * mm});
            skLineSegment(sketch, "E175", {"start": v(311.15, -117.13) * mm, "end": v(273.05, -117.13) * mm});
            skLineSegment(sketch, "E176", {"start": v(273.05, -117.13) * mm, "end": v(277.83, -80.62) * mm});
            skLineSegment(sketch, "E177", {"start": v(277.83, -80.62) * mm, "end": v(311.15, -80.62) * mm});
            skLineSegment(sketch, "E178", {"start": v(273.05, -117.13) * mm, "end": v(273.05, -50.37) * mm, "construction": true});
            skSolve(sketch);
        }
        {
            var Q0;
            Q0=makeQuery(id+"F89.imprint","IMPRINT",FACE,{"disambiguationData":[TD([[makeQuery(id+"F89.imprint","IMPRINT",EDGE,{"derivedFrom":sQuery(id+"F89.wireOp",EDGE,"E161")}),1.0]])]});
            var Q1;
            Q1=makeQuery(id+"F89.imprint","IMPRINT",FACE,{"disambiguationData":[TD([[makeQuery(id+"F89.imprint","IMPRINT",EDGE,{"derivedFrom":sQuery(id+"F89.wireOp",EDGE,"E168")}),1.0]])]});
            var Q2;
            Q2=makeQuery(id+"F89.imprint","IMPRINT",FACE,{"disambiguationData":[TD([[makeQuery(id+"F89.imprint","IMPRINT",EDGE,{"derivedFrom":sQuery(id+"F89.wireOp",EDGE,"E174")}),-1.0]])]});
            extrude(context, id + "F90", {"entities" : qUnion([Q0, Q1, Q2]), "operationType" : NewBodyOperationType.REMOVE, "oppositeDirection" : true, "depth" : 5.5 * mm, "offsetDistance" : 25.4 * mm});
        }
        {
            var Q0;
            Q0=makeQuery(id+"F90.boolean.opBoolean","COPY",EDGE,{"derivedFrom":makeQuery(id+"F90.opExtrude","CAP_EDGE",EDGE,{"disambiguationData":[OSD([sQuery(id+"F89.wireOp",EDGE,"E161")])],"isStart":false})});
            var Q1;
            Q1=makeQuery(id+"F90.boolean.opBoolean","COPY",EDGE,{"derivedFrom":makeQuery(id+"F90.opExtrude","CAP_EDGE",EDGE,{"disambiguationData":[OSD([sQuery(id+"F89.wireOp",EDGE,"E163")])],"isStart":false})});
            var Q2;
            Q2=makeQuery(id+"F90.boolean.opBoolean","COPY",EDGE,{"derivedFrom":makeQuery(id+"F90.opExtrude","CAP_EDGE",EDGE,{"disambiguationData":[OSD([sQuery(id+"F89.wireOp",EDGE,"E170")])],"isStart":false})});
            var Q3;
            Q3=makeQuery(id+"F90.boolean.opBoolean","COPY",EDGE,{"derivedFrom":makeQuery(id+"F90.opExtrude","CAP_EDGE",EDGE,{"disambiguationData":[OSD([sQuery(id+"F89.wireOp",EDGE,"E168")])],"isStart":false})});
            var Q4;
            Q4=makeQuery(id+"F90.boolean.opBoolean","COPY",EDGE,{"derivedFrom":makeQuery(id+"F90.opExtrude","CAP_EDGE",EDGE,{"disambiguationData":[OSD([sQuery(id+"F89.wireOp",EDGE,"E176")])],"isStart":false})});
            fillet(context, id + "F91", {"entities" : qUnion([Q0, Q1, Q2, Q3, Q4]), "radius" : 22.86 * mm, "tangentPropagation" : true, "allowEdgeOverflow" : false});
        }
        {
            var Q0;
            Q0=makeQuery(id+"F90.boolean.opBoolean","COPY",EDGE,{"derivedFrom":makeQuery(id+"F90.opExtrude","CAP_EDGE",EDGE,{"disambiguationData":[OSD([sQuery(id+"F89.wireOp",EDGE,"E174")])],"isStart":false})});
            fillet(context, id + "F92", {"entities" : qUnion([Q0]), "radius" : 5.08 * mm, "tangentPropagation" : true, "allowEdgeOverflow" : false});
        }
        {
            var Q0;
            Q0=makeQuery(id+"F90.boolean.opBoolean","COPY",EDGE,{"derivedFrom":makeQuery(id+"F90.opExtrude","CAP_EDGE",EDGE,{"disambiguationData":[OSD([sQuery(id+"F89.wireOp",EDGE,"E169")])],"isStart":false})});
            var Q1;
            Q1=makeQuery(id+"F90.boolean.opBoolean","COPY",EDGE,{"derivedFrom":makeQuery(id+"F90.opExtrude","CAP_EDGE",EDGE,{"disambiguationData":[OSD([sQuery(id+"F89.wireOp",EDGE,"E175")])],"isStart":false})});
            var Q2;
            Q2=makeQuery(id+"F90.boolean.opBoolean","COPY",EDGE,{"derivedFrom":makeQuery(id+"F90.opExtrude","CAP_EDGE",EDGE,{"disambiguationData":[OSD([sQuery(id+"F89.wireOp",EDGE,"E162")])],"isStart":false})});
            fillet(context, id + "F93", {"entities" : qUnion([Q0, Q1, Q2]), "radius" : 5.08 * mm, "tangentPropagation" : true, "allowEdgeOverflow" : false});
        }
        {
            var Q0;
            Q0=makeQuery(id+"F90.boolean.opBoolean","COPY",FACE,{"derivedFrom":makeQuery(id+"F90.opExtrude","SWEPT_FACE",FACE,{"disambiguationData":[OSD([sQuery(id+"F89.wireOp",EDGE,"E164")])]})});
            var Q1;
            Q1=makeQuery(id+"F90.boolean.opBoolean","COPY",FACE,{"derivedFrom":makeQuery(id+"F90.opExtrude","SWEPT_FACE",FACE,{"disambiguationData":[OSD([sQuery(id+"F89.wireOp",EDGE,"E171")])]})});
            var Q2;
            Q2=makeQuery(id+"F90.boolean.opBoolean","COPY",FACE,{"derivedFrom":makeQuery(id+"F90.opExtrude","SWEPT_FACE",FACE,{"disambiguationData":[OSD([sQuery(id+"F89.wireOp",EDGE,"E177")])]})});
            extrude(context, id + "F94", {"entities" : qUnion([Q0, Q1, Q2]), "operationType" : NewBodyOperationType.REMOVE, "endBound" : BoundingType.THROUGH_ALL, "oppositeDirection" : true, "depth" : 25.4 * mm, "offsetDistance" : 25.4 * mm});
        }
        {
            var Q0;
            Q0=makeQuery(id+"F87.opExtrude","SWEPT_FACE",FACE,{"disambiguationData":[OSD([sQuery(id+"F86.wireOp",EDGE,"E158")])]});
            var sketch = newSketch(context, id + "F95", { "sketchPlane" : qUnion([Q0])});
            skLineSegment(sketch, "E179.bottom", {"start": v(46.8, -126.66) * mm, "end": v(44.42, -126.66) * mm});
            skLineSegment(sketch, "E179.top", {"start": v(46.8, -104.43) * mm, "end": v(44.42, -104.43) * mm});
            skLineSegment(sketch, "E179.left", {"start": v(46.8, -126.66) * mm, "end": v(46.8, -104.43) * mm});
            skLineSegment(sketch, "E179.right", {"start": v(44.42, -126.66) * mm, "end": v(44.42, -104.43) * mm});
            skLineSegment(sketch, "E180.bottom", {"start": v(106.05, -126.66) * mm, "end": v(108.44, -126.66) * mm});
            skLineSegment(sketch, "E180.top", {"start": v(106.05, -104.43) * mm, "end": v(108.44, -104.43) * mm});
            skLineSegment(sketch, "E180.left", {"start": v(106.05, -126.66) * mm, "end": v(106.05, -104.43) * mm});
            skLineSegment(sketch, "E180.right", {"start": v(108.44, -126.66) * mm, "end": v(108.44, -104.43) * mm});
            skLineSegment(sketch, "E181.bottom", {"start": v(190.06, -126.66) * mm, "end": v(187.68, -126.66) * mm});
            skLineSegment(sketch, "E181.top", {"start": v(190.06, -104.43) * mm, "end": v(187.68, -104.43) * mm});
            skLineSegment(sketch, "E181.left", {"start": v(190.06, -126.66) * mm, "end": v(190.06, -104.43) * mm});
            skLineSegment(sketch, "E181.right", {"start": v(187.68, -126.66) * mm, "end": v(187.68, -104.43) * mm});
            skLineSegment(sketch, "E182.bottom", {"start": v(247.48, -126.66) * mm, "end": v(249.87, -126.66) * mm});
            skLineSegment(sketch, "E182.top", {"start": v(247.48, -104.43) * mm, "end": v(249.87, -104.43) * mm});
            skLineSegment(sketch, "E182.left", {"start": v(247.48, -126.66) * mm, "end": v(247.48, -104.43) * mm});
            skLineSegment(sketch, "E182.right", {"start": v(249.87, -126.66) * mm, "end": v(249.87, -104.43) * mm});
            skLineSegment(sketch, "E183.bottom", {"start": v(270.26, -126.66) * mm, "end": v(267.87, -126.66) * mm});
            skLineSegment(sketch, "E183.top", {"start": v(270.26, -104.43) * mm, "end": v(267.87, -104.43) * mm});
            skLineSegment(sketch, "E183.left", {"start": v(270.26, -126.66) * mm, "end": v(270.26, -104.43) * mm});
            skLineSegment(sketch, "E183.right", {"start": v(267.87, -126.66) * mm, "end": v(267.87, -104.43) * mm});
            skLineSegment(sketch, "E184.bottom", {"start": v(314.33, -126.66) * mm, "end": v(311.94, -126.66) * mm});
            skLineSegment(sketch, "E184.top", {"start": v(314.33, -104.43) * mm, "end": v(311.94, -104.43) * mm});
            skLineSegment(sketch, "E184.left", {"start": v(314.33, -126.66) * mm, "end": v(314.33, -104.43) * mm});
            skLineSegment(sketch, "E184.right", {"start": v(311.94, -126.66) * mm, "end": v(311.94, -104.43) * mm});
            skSolve(sketch);
        }
        {
            var Q0;
            Q0=makeQuery(id+"F95.imprint","IMPRINT",FACE,{"disambiguationData":[TD([[makeQuery(id+"F95.imprint","IMPRINT",EDGE,{"derivedFrom":sQuery(id+"F95.wireOp",EDGE,"E179.bottom")}),-1.0]])]});
            var Q1;
            Q1=makeQuery(id+"F95.imprint","IMPRINT",FACE,{"disambiguationData":[TD([[makeQuery(id+"F95.imprint","IMPRINT",EDGE,{"derivedFrom":sQuery(id+"F95.wireOp",EDGE,"E180.bottom")}),-1.0]])]});
            var Q2;
            Q2=makeQuery(id+"F95.imprint","IMPRINT",FACE,{"disambiguationData":[TD([[makeQuery(id+"F95.imprint","IMPRINT",EDGE,{"derivedFrom":sQuery(id+"F95.wireOp",EDGE,"E181.bottom")}),-1.0]])]});
            var Q3;
            Q3=makeQuery(id+"F95.imprint","IMPRINT",FACE,{"disambiguationData":[TD([[makeQuery(id+"F95.imprint","IMPRINT",EDGE,{"derivedFrom":sQuery(id+"F95.wireOp",EDGE,"E182.bottom")}),-1.0]])]});
            var Q4;
            Q4=makeQuery(id+"F95.imprint","IMPRINT",FACE,{"disambiguationData":[TD([[makeQuery(id+"F95.imprint","IMPRINT",EDGE,{"derivedFrom":sQuery(id+"F95.wireOp",EDGE,"E183.bottom")}),-1.0]])]});
            var Q5;
            Q5=makeQuery(id+"F95.imprint","IMPRINT",FACE,{"disambiguationData":[TD([[makeQuery(id+"F95.imprint","IMPRINT",EDGE,{"derivedFrom":sQuery(id+"F95.wireOp",EDGE,"E184.bottom")}),-1.0]])]});
            extrude(context, id + "F96", {"entities" : qUnion([Q0, Q1, Q2, Q3, Q4, Q5]), "operationType" : NewBodyOperationType.ADD, "depth" : 1.59 * mm, "offsetDistance" : 25.4 * mm});
        }
        {
            var Q0;
            Q0=makeQuery(id+"F87.opExtrude","SWEPT_FACE",FACE,{"disambiguationData":[OSD([sQuery(id+"F86.wireOp",EDGE,"E158")])]});
            var sketch = newSketch(context, id + "F97", { "sketchPlane" : qUnion([Q0])});
            skLineSegment(sketch, "E185.bottom", {"start": v(108.44, -126.66) * mm, "end": v(187.68, -126.66) * mm});
            skLineSegment(sketch, "E185.top", {"start": v(108.44, -80.62) * mm, "end": v(187.68, -80.62) * mm});
            skLineSegment(sketch, "E185.left", {"start": v(108.44, -126.66) * mm, "end": v(108.44, -80.62) * mm});
            skLineSegment(sketch, "E185.right", {"start": v(187.68, -126.66) * mm, "end": v(187.68, -80.62) * mm});
            skLineSegment(sketch, "E186.bottom", {"start": v(249.87, -126.66) * mm, "end": v(267.87, -126.66) * mm});
            skLineSegment(sketch, "E186.top", {"start": v(249.87, -80.62) * mm, "end": v(267.87, -80.62) * mm});
            skLineSegment(sketch, "E186.left", {"start": v(249.87, -126.66) * mm, "end": v(249.87, -80.62) * mm});
            skLineSegment(sketch, "E186.right", {"start": v(267.87, -126.66) * mm, "end": v(267.87, -80.62) * mm});
            skLineSegment(sketch, "E187.bottom", {"start": v(44.42, -126.66) * mm, "end": v(9.53, -126.66) * mm});
            skLineSegment(sketch, "E187.top", {"start": v(44.42, -80.62) * mm, "end": v(9.53, -80.62) * mm});
            skLineSegment(sketch, "E187.left", {"start": v(44.42, -126.66) * mm, "end": v(44.42, -80.62) * mm});
            skLineSegment(sketch, "E187.right", {"start": v(9.53, -126.66) * mm, "end": v(9.53, -80.62) * mm});
            skSolve(sketch);
        }
        {
            var Q0;
            {var subQ5=sQuery(id+"F97.wireOp",EDGE,"E187.bottom");Q0=makeQuery(id+"F97.imprint","IMPRINT",FACE,{"disambiguationData":[TD([[makeQuery(id+"F97.imprint","IMPRINT",EDGE,{"derivedFrom":subQ5}),-1.0]])]});}
            var Q1;
            {var subQ6=sQuery(id+"F97.wireOp",EDGE,"E185.bottom");Q1=makeQuery(id+"F97.imprint","IMPRINT",FACE,{"disambiguationData":[TD([[makeQuery(id+"F97.imprint","IMPRINT",EDGE,{"derivedFrom":subQ6}),-1.0]])]});}
            var Q2;
            {var subQ6=sQuery(id+"F97.wireOp",EDGE,"E186.bottom");Q2=makeQuery(id+"F97.imprint","IMPRINT",FACE,{"disambiguationData":[TD([[makeQuery(id+"F97.imprint","IMPRINT",EDGE,{"derivedFrom":subQ6}),-1.0]])]});}
            extrude(context, id + "F98", {"entities" : qUnion([Q0, Q1, Q2]), "operationType" : NewBodyOperationType.ADD, "depth" : 0.8 * mm, "offsetDistance" : 25.4 * mm});
        }
        {
            var Q0;
            Q0=makeQuery(id+"F96.opExtrude","CAP_EDGE",EDGE,{"disambiguationData":[OSD([sQuery(id+"F95.wireOp",EDGE,"E179.left")])],"isStart":false});
            var Q1;
            Q1=makeQuery(id+"F96.opExtrude","CAP_EDGE",EDGE,{"disambiguationData":[OSD([sQuery(id+"F95.wireOp",EDGE,"E179.left")])],"isStart":true});
            var Q2;
            Q2=makeQuery(id+"F96.opExtrude","CAP_EDGE",EDGE,{"disambiguationData":[OSD([sQuery(id+"F95.wireOp",EDGE,"E179.right")])],"isStart":false});
            var Q3;
            Q3=makeQuery(id+"F98.opExtrude","CAP_EDGE",EDGE,{"disambiguationData":[OSD([sQuery(id+"F97.wireOp",EDGE,"E187.top")])],"isStart":false});
            var Q4;
            Q4=makeQuery(id+"F98.opExtrude","CAP_EDGE",EDGE,{"disambiguationData":[OSD([sQuery(id+"F97.wireOp",EDGE,"E187.right")])],"isStart":false});
            var Q5;
            {var subQ0=sQuery(id+"F86.wireOp",EDGE,"E158");Q5=makeQuery(id+"F98.boolean.opBoolean","MERGE",EDGE,{"derivedFrom":[makeQuery(id+"F88.opFillet","BLEND_EDGE",EDGE,{"blendedFrom":[makeQuery(id+"F87.opExtrude","CAP_EDGE",EDGE,{"disambiguationData":[OSD([subQ0])],"isStart":true}),makeQuery(id+"F87.opExtrude","SWEPT_FACE",FACE,{"disambiguationData":[OSD([subQ0])]})],"blendedInto":[makeQuery(id+"F87.opExtrude","SWEPT_FACE",FACE,{"disambiguationData":[OSD([subQ0])]})]}),makeQuery(id+"F98.opExtrude","CAP_EDGE",EDGE,{"disambiguationData":[OSD([sQuery(id+"F97.wireOp",EDGE,"E187.right")])],"isStart":true})]});}
            var Q6;
            Q6=makeQuery(id+"F98.opExtrude","CAP_EDGE",EDGE,{"disambiguationData":[OSD([sQuery(id+"F97.wireOp",EDGE,"E187.bottom")])],"isStart":false});
            var Q7;
            Q7=makeQuery(id+"F96.opExtrude","CAP_EDGE",EDGE,{"disambiguationData":[OSD([sQuery(id+"F95.wireOp",EDGE,"E180.left")])],"isStart":true});
            var Q8;
            Q8=makeQuery(id+"F96.opExtrude","CAP_EDGE",EDGE,{"disambiguationData":[OSD([sQuery(id+"F95.wireOp",EDGE,"E180.left")])],"isStart":false});
            var Q9;
            Q9=makeQuery(id+"F96.opExtrude","CAP_EDGE",EDGE,{"disambiguationData":[OSD([sQuery(id+"F95.wireOp",EDGE,"E180.right")])],"isStart":false});
            var Q10;
            Q10=makeQuery(id+"F96.opExtrude","CAP_EDGE",EDGE,{"disambiguationData":[OSD([sQuery(id+"F95.wireOp",EDGE,"E181.right")])],"isStart":false});
            var Q11;
            Q11=makeQuery(id+"F96.opExtrude","CAP_EDGE",EDGE,{"disambiguationData":[OSD([sQuery(id+"F95.wireOp",EDGE,"E181.left")])],"isStart":false});
            var Q12;
            Q12=makeQuery(id+"F96.opExtrude","CAP_EDGE",EDGE,{"disambiguationData":[OSD([sQuery(id+"F95.wireOp",EDGE,"E181.left")])],"isStart":true});
            var Q13;
            Q13=makeQuery(id+"F96.opExtrude","CAP_EDGE",EDGE,{"disambiguationData":[OSD([sQuery(id+"F95.wireOp",EDGE,"E183.left")])],"isStart":true});
            var Q14;
            Q14=makeQuery(id+"F96.opExtrude","CAP_EDGE",EDGE,{"disambiguationData":[OSD([sQuery(id+"F95.wireOp",EDGE,"E183.left")])],"isStart":false});
            var Q15;
            {var subQ0=sQuery(id+"F97.wireOp",EDGE,"E186.left");Q15=makeQuery(id+"F98.boolean.opBoolean","SPLIT",EDGE,{"disambiguationData":[topologyDisambiguationEdgeConnected([makeQuery(id+"F96.opExtrude","SWEPT_FACE",FACE,{"disambiguationData":[OSD([sQuery(id+"F95.wireOp",EDGE,"E182.right")])]})])],"derivedFrom":makeQuery(id+"F98.opExtrude","CAP_EDGE",EDGE,{"disambiguationData":[OSD([subQ0])],"isStart":false})});}
            var Q16;
            Q16=makeQuery(id+"F96.opExtrude","CAP_EDGE",EDGE,{"disambiguationData":[OSD([sQuery(id+"F95.wireOp",EDGE,"E182.right")])],"isStart":false});
            var Q17;
            Q17=makeQuery(id+"F96.opExtrude","CAP_EDGE",EDGE,{"disambiguationData":[OSD([sQuery(id+"F95.wireOp",EDGE,"E183.right")])],"isStart":false});
            var Q18;
            Q18=makeQuery(id+"F96.opExtrude","CAP_EDGE",EDGE,{"disambiguationData":[OSD([sQuery(id+"F95.wireOp",EDGE,"E182.left")])],"isStart":true});
            var Q19;
            Q19=makeQuery(id+"F96.opExtrude","CAP_EDGE",EDGE,{"disambiguationData":[OSD([sQuery(id+"F95.wireOp",EDGE,"E182.left")])],"isStart":false});
            var Q20;
            {var subQ0=sQuery(id+"F97.wireOp",EDGE,"E186.right");Q20=makeQuery(id+"F98.boolean.opBoolean","SPLIT",EDGE,{"disambiguationData":[topologyDisambiguationEdgeConnected([makeQuery(id+"F96.opExtrude","SWEPT_FACE",FACE,{"disambiguationData":[OSD([sQuery(id+"F95.wireOp",EDGE,"E183.right")])]})])],"derivedFrom":makeQuery(id+"F98.opExtrude","CAP_EDGE",EDGE,{"disambiguationData":[OSD([subQ0])],"isStart":false})});}
            var Q21;
            Q21=makeQuery(id+"F96.opExtrude","CAP_EDGE",EDGE,{"disambiguationData":[OSD([sQuery(id+"F95.wireOp",EDGE,"E184.right")])],"isStart":true});
            var Q22;
            Q22=makeQuery(id+"F96.opExtrude","CAP_EDGE",EDGE,{"disambiguationData":[OSD([sQuery(id+"F95.wireOp",EDGE,"E184.right")])],"isStart":false});
            var Q23;
            Q23=makeQuery(id+"F96.opExtrude","CAP_EDGE",EDGE,{"disambiguationData":[OSD([sQuery(id+"F95.wireOp",EDGE,"E184.left")])],"isStart":false});
            var Q24;
            {var subQ0=sQuery(id+"F86.wireOp",EDGE,"E158");Q24=makeQuery(id+"F96.boolean.opBoolean","MERGE",EDGE,{"derivedFrom":[makeQuery(id+"F88.opFillet","BLEND_EDGE",EDGE,{"blendedFrom":[makeQuery(id+"F87.opExtrude","CAP_EDGE",EDGE,{"disambiguationData":[OSD([subQ0])],"isStart":false}),makeQuery(id+"F87.opExtrude","SWEPT_FACE",FACE,{"disambiguationData":[OSD([subQ0])]})],"blendedInto":[makeQuery(id+"F87.opExtrude","SWEPT_FACE",FACE,{"disambiguationData":[OSD([subQ0])]})]}),makeQuery(id+"F96.opExtrude","CAP_EDGE",EDGE,{"disambiguationData":[OSD([sQuery(id+"F95.wireOp",EDGE,"E184.left")])],"isStart":true})]});}
            var Q25;
            {var subQ0=sQuery(id+"F97.wireOp",EDGE,"E185.left");Q25=makeQuery(id+"F98.boolean.opBoolean","SPLIT",EDGE,{"disambiguationData":[topologyDisambiguationEdgeConnected([makeQuery(id+"F96.opExtrude","SWEPT_FACE",FACE,{"disambiguationData":[OSD([sQuery(id+"F95.wireOp",EDGE,"E180.right")])]})])],"derivedFrom":makeQuery(id+"F98.opExtrude","CAP_EDGE",EDGE,{"disambiguationData":[OSD([subQ0])],"isStart":false})});}
            var Q26;
            {var subQ0=sQuery(id+"F97.wireOp",EDGE,"E187.left");Q26=makeQuery(id+"F98.boolean.opBoolean","SPLIT",EDGE,{"disambiguationData":[topologyDisambiguationEdgeConnected([makeQuery(id+"F96.opExtrude","SWEPT_FACE",FACE,{"disambiguationData":[OSD([sQuery(id+"F95.wireOp",EDGE,"E179.right")])]})])],"derivedFrom":makeQuery(id+"F98.opExtrude","CAP_EDGE",EDGE,{"disambiguationData":[OSD([subQ0])],"isStart":false})});}
            fillet(context, id + "F99", {"entities" : qUnion([Q0, Q1, Q2, Q3, Q4, Q5, Q6, Q7, Q8, Q9, Q10, Q11, Q12, Q13, Q14, Q15, Q16, Q17, Q18, Q19, Q20, Q21, Q22, Q23, Q24, Q25, Q26]), "radius" : 0.25 * mm, "tangentPropagation" : true, "allowEdgeOverflow" : false});
        }
        {
            var Q0;
            {var subQ0=sQuery(id+"F6.wireOp",EDGE,"E9");var subQ1=sQuery(id+"F0.wireOp",EDGE,"E0.right");var subQ2=sQuery(id+"F0.wireOp",EDGE,"E0.bottom");var subQ3=sQuery(id+"F0.wireOp",EDGE,"E0.left");var subQ4=sQuery(id+"F0.wireOp",EDGE,"E0.top");var subQ5=sQuery(id+"F6.wireOp",EDGE,"E17");var subQ6=sQuery(id+"F4.wireOp",EDGE,"E8.0");var subQ7=sQuery(id+"F4.wireOp",EDGE,"E3.0");var subQ8=sQuery(id+"F4.wireOp",EDGE,"E2.0");var subQ9=sQuery(id+"F4.wireOp",EDGE,"E7.0");var subQ10=sQuery(id+"F4.wireOp",EDGE,"E6.0");var subQ11=sQuery(id+"F4.wireOp",EDGE,"E4.0");var subQ12=sQuery(id+"F4.wireOp",EDGE,"E5.0");var subQ13=sQuery(id+"F4.wireOp",EDGE,"E1.0");Q0=makeQuery(id+"F68.boolean.opBoolean","SPLIT",FACE,{"disambiguationData":[TD([makeQuery(id+"F5.opExtrude","SWEPT_FACE",FACE,{"disambiguationData":[OSD([subQ8])]})])],"derivedFrom":makeQuery(id+"F11.boolean.opBoolean","MERGE",FACE,{"derivedFrom":[makeQuery(id+"F7.boolean.opBoolean","MERGE",FACE,{"derivedFrom":[makeQuery(id+"F5.opExtrude","CAP_FACE",FACE,{"disambiguationData":[OSD([subQ2,subQ4,subQ3,subQ1,subQ13,subQ8,subQ7,subQ11,subQ12,subQ10,subQ9,subQ6])],"isStart":false}),makeQuery(id+"F7.opExtrude","CAP_FACE",FACE,{"disambiguationData":[OSD([subQ8,subQ7,subQ0])],"isStart":false}),makeQuery(id+"F7.opExtrude","CAP_FACE",FACE,{"disambiguationData":[OSD([subQ13,subQ7,sQuery(id+"F6.wireOp",EDGE,"E11")])],"isStart":false}),makeQuery(id+"F7.opExtrude","CAP_FACE",FACE,{"disambiguationData":[OSD([subQ12,subQ10,sQuery(id+"F6.wireOp",EDGE,"E12")])],"isStart":false}),makeQuery(id+"F7.opExtrude","CAP_FACE",FACE,{"disambiguationData":[OSD([subQ11,subQ10,sQuery(id+"F6.wireOp",EDGE,"E13")])],"isStart":false}),makeQuery(id+"F7.opExtrude","CAP_FACE",FACE,{"disambiguationData":[OSD([subQ9,sQuery(id+"F6.wireOp",EDGE,"E14")])],"isStart":false}),makeQuery(id+"F7.opExtrude","CAP_FACE",FACE,{"disambiguationData":[OSD([subQ9,sQuery(id+"F6.wireOp",EDGE,"E15")])],"isStart":false}),makeQuery(id+"F7.opExtrude","CAP_FACE",FACE,{"disambiguationData":[OSD([subQ6,sQuery(id+"F6.wireOp",EDGE,"E16")])],"isStart":false}),makeQuery(id+"F7.opExtrude","CAP_FACE",FACE,{"disambiguationData":[OSD([subQ6,subQ5])],"isStart":false})]}),makeQuery(id+"F11.opExtrude","CAP_FACE",FACE,{"disambiguationData":[OSD([sQuery(id+"F10.wireOp",EDGE,"E26"),sQuery(id+"F10.wireOp",EDGE,"E27"),sQuery(id+"F10.wireOp",EDGE,"E28"),sQuery(id+"F10.wireOp",EDGE,"E29")])],"isStart":false}),makeQuery(id+"F11.opExtrude","CAP_FACE",FACE,{"disambiguationData":[OSD([sQuery(id+"F10.wireOp",EDGE,"E34"),sQuery(id+"F10.wireOp",EDGE,"E35"),sQuery(id+"F10.wireOp",EDGE,"E36"),sQuery(id+"F10.wireOp",EDGE,"E37")])],"isStart":false}),makeQuery(id+"F11.opExtrude","CAP_FACE",FACE,{"disambiguationData":[OSD([sQuery(id+"F10.wireOp",EDGE,"E42"),sQuery(id+"F10.wireOp",EDGE,"E43"),sQuery(id+"F10.wireOp",EDGE,"E44"),sQuery(id+"F10.wireOp",EDGE,"E45")])],"isStart":false}),makeQuery(id+"F11.opExtrude","CAP_FACE",FACE,{"disambiguationData":[OSD([sQuery(id+"F10.wireOp",EDGE,"E47"),sQuery(id+"F10.wireOp",EDGE,"E48"),sQuery(id+"F10.wireOp",EDGE,"E49"),sQuery(id+"F10.wireOp",EDGE,"E50")])],"isStart":false})]})});}
            var Q1;
            Q1=makeQuery(id+"F44.opExtrude","CAP_FACE",FACE,{"disambiguationData":[OSD([sQuery(id+"F43.wireOp",EDGE,"E84.bottom"),sQuery(id+"F43.wireOp",EDGE,"E84.top"),sQuery(id+"F43.wireOp",EDGE,"E84.left"),sQuery(id+"F43.wireOp",EDGE,"E84.right"),sQuery(id+"F43.wireOp",EDGE,"E85.top"),sQuery(id+"F43.wireOp",EDGE,"E85.left"),sQuery(id+"F43.wireOp",EDGE,"E85.right"),sQuery(id+"F43.wireOp",EDGE,"E86.trimOffspring")])],"isStart":false});
            var Q2;
            Q2=makeQuery(id+"F39.opExtrude","CAP_FACE",FACE,{"disambiguationData":[OSD([sQuery(id+"F38.wireOp",EDGE,"E82.bottom"),sQuery(id+"F38.wireOp",EDGE,"E82.top"),sQuery(id+"F38.wireOp",EDGE,"E82.left"),sQuery(id+"F38.wireOp",EDGE,"E82.right")])],"isStart":false});
            var Q3;
            Q3=makeQuery(id+"F56.opExtrude","CAP_FACE",FACE,{"disambiguationData":[OSD([sQuery(id+"F55.wireOp",EDGE,"E102.bottom"),sQuery(id+"F55.wireOp",EDGE,"E102.top"),sQuery(id+"F55.wireOp",EDGE,"E103"),sQuery(id+"F55.wireOp",EDGE,"E104"),sQuery(id+"F55.wireOp",EDGE,"E105"),sQuery(id+"F55.wireOp",EDGE,"E106")])],"isStart":false});
            var Q4;
            Q4=makeQuery(id+"F27.opExtrude","CAP_FACE",FACE,{"disambiguationData":[OSD([sQuery(id+"F26.wireOp",EDGE,"E60.bottom"),sQuery(id+"F26.wireOp",EDGE,"E60.top"),sQuery(id+"F26.wireOp",EDGE,"E60.left"),sQuery(id+"F26.wireOp",EDGE,"E60.right")])],"isStart":false});
            var Q5;
            Q5=makeQuery(id+"F22.opExtrude","CAP_FACE",FACE,{"disambiguationData":[OSD([sQuery(id+"F21.wireOp",EDGE,"E56.bottom"),sQuery(id+"F21.wireOp",EDGE,"E56.top"),sQuery(id+"F21.wireOp",EDGE,"E56.left"),sQuery(id+"F21.wireOp",EDGE,"E56.right")])],"isStart":false});
            var Q6;
            {var subQ0=sQuery(id+"F6.wireOp",EDGE,"E13");var subQ1=sQuery(id+"F0.wireOp",EDGE,"E0.bottom");var subQ2=sQuery(id+"F0.wireOp",EDGE,"E0.right");var subQ3=sQuery(id+"F0.wireOp",EDGE,"E0.left");var subQ4=sQuery(id+"F0.wireOp",EDGE,"E0.top");var subQ5=sQuery(id+"F4.wireOp",EDGE,"E8.0");var subQ6=sQuery(id+"F4.wireOp",EDGE,"E6.0");var subQ7=sQuery(id+"F4.wireOp",EDGE,"E4.0");var subQ8=sQuery(id+"F6.wireOp",EDGE,"E16");var subQ9=sQuery(id+"F4.wireOp",EDGE,"E7.0");var subQ10=sQuery(id+"F4.wireOp",EDGE,"E5.0");var subQ11=sQuery(id+"F4.wireOp",EDGE,"E3.0");var subQ12=sQuery(id+"F4.wireOp",EDGE,"E1.0");var subQ13=sQuery(id+"F4.wireOp",EDGE,"E2.0");Q6=makeQuery(id+"F68.boolean.opBoolean","SPLIT",FACE,{"disambiguationData":[TD([makeQuery(id+"F5.opExtrude","SWEPT_FACE",FACE,{"disambiguationData":[OSD([subQ7])]})])],"derivedFrom":makeQuery(id+"F11.boolean.opBoolean","MERGE",FACE,{"derivedFrom":[makeQuery(id+"F7.boolean.opBoolean","MERGE",FACE,{"derivedFrom":[makeQuery(id+"F5.opExtrude","CAP_FACE",FACE,{"disambiguationData":[OSD([subQ1,subQ4,subQ3,subQ2,subQ12,subQ13,subQ11,subQ7,subQ10,subQ6,subQ9,subQ5])],"isStart":false}),makeQuery(id+"F7.opExtrude","CAP_FACE",FACE,{"disambiguationData":[OSD([subQ13,subQ11,sQuery(id+"F6.wireOp",EDGE,"E9")])],"isStart":false}),makeQuery(id+"F7.opExtrude","CAP_FACE",FACE,{"disambiguationData":[OSD([subQ12,subQ11,sQuery(id+"F6.wireOp",EDGE,"E11")])],"isStart":false}),makeQuery(id+"F7.opExtrude","CAP_FACE",FACE,{"disambiguationData":[OSD([subQ10,subQ6,sQuery(id+"F6.wireOp",EDGE,"E12")])],"isStart":false}),makeQuery(id+"F7.opExtrude","CAP_FACE",FACE,{"disambiguationData":[OSD([subQ7,subQ6,subQ0])],"isStart":false}),makeQuery(id+"F7.opExtrude","CAP_FACE",FACE,{"disambiguationData":[OSD([subQ9,sQuery(id+"F6.wireOp",EDGE,"E14")])],"isStart":false}),makeQuery(id+"F7.opExtrude","CAP_FACE",FACE,{"disambiguationData":[OSD([subQ9,sQuery(id+"F6.wireOp",EDGE,"E15")])],"isStart":false}),makeQuery(id+"F7.opExtrude","CAP_FACE",FACE,{"disambiguationData":[OSD([subQ5,subQ8])],"isStart":false}),makeQuery(id+"F7.opExtrude","CAP_FACE",FACE,{"disambiguationData":[OSD([subQ5,sQuery(id+"F6.wireOp",EDGE,"E17")])],"isStart":false})]}),makeQuery(id+"F11.opExtrude","CAP_FACE",FACE,{"disambiguationData":[OSD([sQuery(id+"F10.wireOp",EDGE,"E26"),sQuery(id+"F10.wireOp",EDGE,"E27"),sQuery(id+"F10.wireOp",EDGE,"E28"),sQuery(id+"F10.wireOp",EDGE,"E29")])],"isStart":false}),makeQuery(id+"F11.opExtrude","CAP_FACE",FACE,{"disambiguationData":[OSD([sQuery(id+"F10.wireOp",EDGE,"E34"),sQuery(id+"F10.wireOp",EDGE,"E35"),sQuery(id+"F10.wireOp",EDGE,"E36"),sQuery(id+"F10.wireOp",EDGE,"E37")])],"isStart":false}),makeQuery(id+"F11.opExtrude","CAP_FACE",FACE,{"disambiguationData":[OSD([sQuery(id+"F10.wireOp",EDGE,"E42"),sQuery(id+"F10.wireOp",EDGE,"E43"),sQuery(id+"F10.wireOp",EDGE,"E44"),sQuery(id+"F10.wireOp",EDGE,"E45")])],"isStart":false}),makeQuery(id+"F11.opExtrude","CAP_FACE",FACE,{"disambiguationData":[OSD([sQuery(id+"F10.wireOp",EDGE,"E47"),sQuery(id+"F10.wireOp",EDGE,"E48"),sQuery(id+"F10.wireOp",EDGE,"E49"),sQuery(id+"F10.wireOp",EDGE,"E50")])],"isStart":false})]})});}
            var Q7;
            {var subQ0=sQuery(id+"F6.wireOp",EDGE,"E14");var subQ1=sQuery(id+"F10.wireOp",EDGE,"E26");var subQ2=sQuery(id+"F6.wireOp",EDGE,"E12");var subQ3=sQuery(id+"F0.wireOp",EDGE,"E0.right");var subQ4=sQuery(id+"F6.wireOp",EDGE,"E11");var subQ5=sQuery(id+"F0.wireOp",EDGE,"E0.left");var subQ6=sQuery(id+"F0.wireOp",EDGE,"E0.top");var subQ7=sQuery(id+"F0.wireOp",EDGE,"E0.bottom");var subQ9=sQuery(id+"F4.wireOp",EDGE,"E6.0");var subQ10=sQuery(id+"F6.wireOp",EDGE,"E15");var subQ11=sQuery(id+"F10.wireOp",EDGE,"E27");var subQ12=sQuery(id+"F4.wireOp",EDGE,"E5.0");var subQ13=sQuery(id+"F4.wireOp",EDGE,"E1.0");var subQ14=sQuery(id+"F4.wireOp",EDGE,"E3.0");var subQ15=sQuery(id+"F4.wireOp",EDGE,"E7.0");var subQ16=sQuery(id+"F10.wireOp",EDGE,"E43");var subQ17=sQuery(id+"F10.wireOp",EDGE,"E28");var subQ18=sQuery(id+"F10.wireOp",EDGE,"E34");var subQ19=sQuery(id+"F10.wireOp",EDGE,"E35");var subQ20=sQuery(id+"F10.wireOp",EDGE,"E36");var subQ21=sQuery(id+"F10.wireOp",EDGE,"E42");var subQ22=sQuery(id+"F10.wireOp",EDGE,"E44");var subQ23=sQuery(id+"F10.wireOp",EDGE,"E47");var subQ26=sQuery(id+"F10.wireOp",EDGE,"E48");var subQ27=sQuery(id+"F10.wireOp",EDGE,"E49");var subQ28=sQuery(id+"F4.wireOp",EDGE,"E8.0");var subQ29=sQuery(id+"F4.wireOp",EDGE,"E4.0");var subQ30=sQuery(id+"F4.wireOp",EDGE,"E2.0");Q7=makeQuery(id+"F68.boolean.opBoolean","SPLIT",FACE,{"disambiguationData":[TD([makeQuery(id+"F1.opExtrude","SWEPT_FACE",FACE,{"disambiguationData":[OSD([subQ6])]})])],"derivedFrom":makeQuery(id+"F11.boolean.opBoolean","MERGE",FACE,{"derivedFrom":[makeQuery(id+"F7.boolean.opBoolean","MERGE",FACE,{"derivedFrom":[makeQuery(id+"F5.opExtrude","CAP_FACE",FACE,{"disambiguationData":[OSD([subQ7,subQ6,subQ5,subQ3,subQ13,subQ30,subQ14,subQ29,subQ12,subQ9,subQ15,subQ28])],"isStart":false}),makeQuery(id+"F7.opExtrude","CAP_FACE",FACE,{"disambiguationData":[OSD([subQ30,subQ14,sQuery(id+"F6.wireOp",EDGE,"E9")])],"isStart":false}),makeQuery(id+"F7.opExtrude","CAP_FACE",FACE,{"disambiguationData":[OSD([subQ13,subQ14,subQ4])],"isStart":false}),makeQuery(id+"F7.opExtrude","CAP_FACE",FACE,{"disambiguationData":[OSD([subQ12,subQ9,subQ2])],"isStart":false}),makeQuery(id+"F7.opExtrude","CAP_FACE",FACE,{"disambiguationData":[OSD([subQ29,subQ9,sQuery(id+"F6.wireOp",EDGE,"E13")])],"isStart":false}),makeQuery(id+"F7.opExtrude","CAP_FACE",FACE,{"disambiguationData":[OSD([subQ15,subQ0])],"isStart":false}),makeQuery(id+"F7.opExtrude","CAP_FACE",FACE,{"disambiguationData":[OSD([subQ15,subQ10])],"isStart":false}),makeQuery(id+"F7.opExtrude","CAP_FACE",FACE,{"disambiguationData":[OSD([subQ28,sQuery(id+"F6.wireOp",EDGE,"E16")])],"isStart":false}),makeQuery(id+"F7.opExtrude","CAP_FACE",FACE,{"disambiguationData":[OSD([subQ28,sQuery(id+"F6.wireOp",EDGE,"E17")])],"isStart":false})]}),makeQuery(id+"F11.opExtrude","CAP_FACE",FACE,{"disambiguationData":[OSD([subQ1,subQ11,subQ17,sQuery(id+"F10.wireOp",EDGE,"E29")])],"isStart":false}),makeQuery(id+"F11.opExtrude","CAP_FACE",FACE,{"disambiguationData":[OSD([subQ18,subQ19,subQ20,sQuery(id+"F10.wireOp",EDGE,"E37")])],"isStart":false}),makeQuery(id+"F11.opExtrude","CAP_FACE",FACE,{"disambiguationData":[OSD([subQ21,subQ16,subQ22,sQuery(id+"F10.wireOp",EDGE,"E45")])],"isStart":false}),makeQuery(id+"F11.opExtrude","CAP_FACE",FACE,{"disambiguationData":[OSD([subQ23,subQ26,subQ27,sQuery(id+"F10.wireOp",EDGE,"E50")])],"isStart":false})]})});}
            fillet(context, id + "F100", {"entities" : qUnion([Q0, Q1, Q2, Q3, Q4, Q5, Q6, Q7]), "radius" : 0.25 * mm, "tangentPropagation" : true, "allowEdgeOverflow" : false});
        }
        {
            var Q0;
            Q0=makeQuery(id+"F75.opExtrude","CAP_FACE",FACE,{"disambiguationData":[OSD([sQuery(id+"F74.wireOp",EDGE,"E136.bottom"),sQuery(id+"F74.wireOp",EDGE,"E136.top"),sQuery(id+"F74.wireOp",EDGE,"E136.left"),sQuery(id+"F74.wireOp",EDGE,"E136.right"),sQuery(id+"F74.wireOp",EDGE,"E137.top"),sQuery(id+"F74.wireOp",EDGE,"E137.left"),sQuery(id+"F74.wireOp",EDGE,"E137.right"),sQuery(id+"F74.wireOp",EDGE,"E138.top"),sQuery(id+"F74.wireOp",EDGE,"E138.left"),sQuery(id+"F74.wireOp",EDGE,"E138.right")])],"isStart":false});
            var sketch = newSketch(context, id + "F101", { "sketchPlane" : qUnion([Q0])});
            skLineSegment(sketch, "E188.bottom", {"start": v(147.62, -82.66) * mm, "end": v(-147.62, -82.66) * mm});
            skLineSegment(sketch, "E188.top", {"start": v(147.62, -171.5) * mm, "end": v(-147.62, -171.5) * mm});
            skLineSegment(sketch, "E188.left", {"start": v(147.62, -82.66) * mm, "end": v(147.62, -171.5) * mm});
            skLineSegment(sketch, "E188.right", {"start": v(-147.62, -82.66) * mm, "end": v(-147.62, -171.5) * mm});
            skPoint(sketch, "E188.middle", {"position": v(0, -127.08) * mm});
            skPoint(sketch, "E188.middle.positionSnap0", {"position": v(-166.69, -127.08) * mm});
            skPoint(sketch, "E188.centerSnap0", {"position": v(-166.69, -127.08) * mm});
            skSolve(sketch);
        }
        {
            var Q0;
            Q0=makeQuery(id+"F101.imprint","IMPRINT",FACE,{"disambiguationData":[TD([[makeQuery(id+"F101.imprint","IMPRINT",EDGE,{"derivedFrom":sQuery(id+"F101.wireOp",EDGE,"E188.bottom")}),1.0]])]});
            extrude(context, id + "F102", {"entities" : qUnion([Q0]), "operationType" : NewBodyOperationType.REMOVE, "endBound" : BoundingType.THROUGH_ALL, "oppositeDirection" : true, "depth" : 25.4 * mm, "offsetDistance" : 25.4 * mm});
        }
        {
            var Q0;
            Q0=qCreatedBy(makeId("Top.planeOp"),FACE);
            var sketch = newSketch(context, id + "F103", { "sketchPlane" : qUnion([Q0])});
            skLineSegment(sketch, "E189.bottom", {"start": v(-161.92, -269.1) * mm, "end": v(161.93, -269.1) * mm});
            skLineSegment(sketch, "E189.top", {"start": v(-161.92, -367.52) * mm, "end": v(161.93, -367.52) * mm});
            skLineSegment(sketch, "E189.left", {"start": v(-161.92, -269.1) * mm, "end": v(-161.92, -367.52) * mm});
            skLineSegment(sketch, "E189.right", {"start": v(161.93, -269.1) * mm, "end": v(161.93, -367.52) * mm});
            skSolve(sketch);
        }
        {
            var Q0;
            Q0=qSketchRegion(id+"F103",true);
            extrude(context, id + "F104", {"entities" : qUnion([Q0]), "depth" : 50.8 * mm, "offsetDistance" : 25.4 * mm});
        }
        {
            var Q0;
            Q0=makeQuery(id+"F104.opExtrude","SWEPT_EDGE",EDGE,{"disambiguationData":[OSD([sQuery(id+"F103.wireOp",EDGE,"E189.bottom"),sQuery(id+"F103.wireOp",EDGE,"E189.right")])]});
            var Q1;
            Q1=makeQuery(id+"F104.opExtrude","SWEPT_EDGE",EDGE,{"disambiguationData":[OSD([sQuery(id+"F103.wireOp",EDGE,"E189.bottom"),sQuery(id+"F103.wireOp",EDGE,"E189.left")])]});
            fillet(context, id + "F105", {"entities" : qUnion([Q0, Q1]), "radius" : 9.52 * mm, "tangentPropagation" : true, "allowEdgeOverflow" : false});
        }
        {
            var Q0;
            Q0=makeQuery(id+"F104.opExtrude","SWEPT_EDGE",EDGE,{"disambiguationData":[OSD([sQuery(id+"F103.wireOp",EDGE,"E189.top"),sQuery(id+"F103.wireOp",EDGE,"E189.right")])]});
            var Q1;
            Q1=makeQuery(id+"F104.opExtrude","SWEPT_EDGE",EDGE,{"disambiguationData":[OSD([sQuery(id+"F103.wireOp",EDGE,"E189.top"),sQuery(id+"F103.wireOp",EDGE,"E189.left")])]});
            fillet(context, id + "F106", {"entities" : qUnion([Q0, Q1]), "radius" : 15.88 * mm, "tangentPropagation" : true, "allowEdgeOverflow" : false});
        }
        {
            var Q0;
            Q0=makeQuery(id+"F104.opExtrude","SWEPT_FACE",FACE,{"disambiguationData":[OSD([sQuery(id+"F103.wireOp",EDGE,"E189.right")])]});
            var sketch = newSketch(context, id + "F107", { "sketchPlane" : qUnion([Q0])});
            skLineSegment(sketch, "E190", {"start": v(-269.1, 4.75) * mm, "end": v(-367.52, 50.8) * mm});
            skLineSegment(sketch, "E191", {"start": v(-269.1, 4.75) * mm, "end": v(-269.1, -4.61) * mm});
            skLineSegment(sketch, "E192", {"start": v(-269.1, -4.61) * mm, "end": v(-367.52, -4.61) * mm});
            skLineSegment(sketch, "E193", {"start": v(-367.52, -4.61) * mm, "end": v(-367.52, 50.8) * mm});
            skSolve(sketch);
        }
        {
            var Q0;
            Q0=qSketchRegion(id+"F107",true);
            extrude(context, id + "F108", {"entities" : qUnion([Q0]), "operationType" : NewBodyOperationType.REMOVE, "endBound" : BoundingType.THROUGH_ALL, "oppositeDirection" : true, "depth" : 25.4 * mm, "offsetDistance" : 25.4 * mm});
        }
        {
            var Q0;
            Q0=makeQuery(id+"F104.opExtrude","SWEPT_FACE",FACE,{"disambiguationData":[OSD([sQuery(id+"F103.wireOp",EDGE,"E189.bottom")])]});
            var sketch = newSketch(context, id + "F109", { "sketchPlane" : qUnion([Q0])});
            skLineSegment(sketch, "E194", {"start": v(-106.36, 50.8) * mm, "end": v(-111.13, 14.29) * mm});
            skLineSegment(sketch, "E195", {"start": v(-111.13, 14.29) * mm, "end": v(-60.33, 14.29) * mm});
            skLineSegment(sketch, "E196", {"start": v(-60.33, 14.29) * mm, "end": v(-65.09, 50.8) * mm});
            skLineSegment(sketch, "E197", {"start": v(-65.09, 50.8) * mm, "end": v(-106.36, 50.8) * mm});
            skLineSegment(sketch, "E198", {"start": v(-85.73, 14.29) * mm, "end": v(-85.73, 50.8) * mm, "construction": true});
            skLineSegment(sketch, "E199", {"start": v(-111.13, 14.29) * mm, "end": v(-111.13, 46.62) * mm, "construction": true});
            skLineSegment(sketch, "E200", {"start": v(-60.33, 14.29) * mm, "end": v(-60.33, 82.26) * mm, "construction": true});
            skLineSegment(sketch, "E201", {"start": v(36.53, 50.8) * mm, "end": v(31.75, 14.29) * mm});
            skLineSegment(sketch, "E202", {"start": v(31.75, 14.29) * mm, "end": v(82.55, 14.29) * mm});
            skLineSegment(sketch, "E203", {"start": v(82.55, 14.29) * mm, "end": v(77.77, 50.8) * mm});
            skLineSegment(sketch, "E204", {"start": v(77.77, 50.8) * mm, "end": v(36.53, 50.8) * mm});
            skLineSegment(sketch, "E205", {"start": v(31.75, 14.29) * mm, "end": v(31.75, 42.1) * mm, "construction": true});
            skLineSegment(sketch, "E206", {"start": v(82.55, 14.29) * mm, "end": v(82.55, 85.26) * mm, "construction": true});
            skLineSegment(sketch, "E207", {"start": v(149.22, 50.8) * mm, "end": v(149.22, 14.29) * mm});
            skLineSegment(sketch, "E208", {"start": v(149.22, 14.29) * mm, "end": v(111.12, 14.29) * mm});
            skLineSegment(sketch, "E209", {"start": v(111.12, 14.29) * mm, "end": v(115.9, 50.8) * mm});
            skLineSegment(sketch, "E210", {"start": v(115.9, 50.8) * mm, "end": v(149.22, 50.8) * mm});
            skLineSegment(sketch, "E211", {"start": v(111.12, 14.29) * mm, "end": v(111.12, 60.3) * mm, "construction": true});
            skSolve(sketch);
        }
        {
            var Q0;
            Q0=qSketchRegion(id+"F109",true);
            extrude(context, id + "F110", {"entities" : qUnion([Q0]), "operationType" : NewBodyOperationType.REMOVE, "oppositeDirection" : true, "depth" : 5.5 * mm, "offsetDistance" : 25.4 * mm});
        }
        {
            var Q0;
            Q0=makeQuery(id+"F110.boolean.opBoolean","COPY",EDGE,{"derivedFrom":makeQuery(id+"F110.opExtrude","CAP_EDGE",EDGE,{"disambiguationData":[OSD([sQuery(id+"F109.wireOp",EDGE,"E203")])],"isStart":false})});
            var Q1;
            Q1=makeQuery(id+"F110.boolean.opBoolean","COPY",EDGE,{"derivedFrom":makeQuery(id+"F110.opExtrude","CAP_EDGE",EDGE,{"disambiguationData":[OSD([sQuery(id+"F109.wireOp",EDGE,"E201")])],"isStart":false})});
            var Q2;
            Q2=makeQuery(id+"F110.boolean.opBoolean","COPY",EDGE,{"derivedFrom":makeQuery(id+"F110.opExtrude","CAP_EDGE",EDGE,{"disambiguationData":[OSD([sQuery(id+"F109.wireOp",EDGE,"E209")])],"isStart":false})});
            var Q3;
            Q3=makeQuery(id+"F110.boolean.opBoolean","COPY",EDGE,{"derivedFrom":makeQuery(id+"F110.opExtrude","CAP_EDGE",EDGE,{"disambiguationData":[OSD([sQuery(id+"F109.wireOp",EDGE,"E194")])],"isStart":false})});
            var Q4;
            Q4=makeQuery(id+"F110.boolean.opBoolean","COPY",EDGE,{"derivedFrom":makeQuery(id+"F110.opExtrude","CAP_EDGE",EDGE,{"disambiguationData":[OSD([sQuery(id+"F109.wireOp",EDGE,"E196")])],"isStart":false})});
            fillet(context, id + "F111", {"entities" : qUnion([Q0, Q1, Q2, Q3, Q4]), "radius" : 22.86 * mm, "tangentPropagation" : true, "allowEdgeOverflow" : false});
        }
        {
            var Q0;
            Q0=makeQuery(id+"F110.boolean.opBoolean","COPY",EDGE,{"derivedFrom":makeQuery(id+"F110.opExtrude","CAP_EDGE",EDGE,{"disambiguationData":[OSD([sQuery(id+"F109.wireOp",EDGE,"E207")])],"isStart":false})});
            var Q1;
            Q1=makeQuery(id+"F110.boolean.opBoolean","COPY",EDGE,{"derivedFrom":makeQuery(id+"F110.opExtrude","CAP_EDGE",EDGE,{"disambiguationData":[OSD([sQuery(id+"F109.wireOp",EDGE,"E208")])],"isStart":false})});
            var Q2;
            Q2=makeQuery(id+"F110.boolean.opBoolean","COPY",EDGE,{"derivedFrom":makeQuery(id+"F110.opExtrude","CAP_EDGE",EDGE,{"disambiguationData":[OSD([sQuery(id+"F109.wireOp",EDGE,"E202")])],"isStart":false})});
            var Q3;
            Q3=makeQuery(id+"F110.boolean.opBoolean","COPY",EDGE,{"derivedFrom":makeQuery(id+"F110.opExtrude","CAP_EDGE",EDGE,{"disambiguationData":[OSD([sQuery(id+"F109.wireOp",EDGE,"E195")])],"isStart":false})});
            fillet(context, id + "F112", {"entities" : qUnion([Q0, Q1, Q2, Q3]), "radius" : 5.08 * mm, "tangentPropagation" : true, "allowEdgeOverflow" : false});
        }
        {
            var Q0;
            Q0=makeQuery(id+"F104.opExtrude","SWEPT_FACE",FACE,{"disambiguationData":[OSD([sQuery(id+"F103.wireOp",EDGE,"E189.bottom")])]});
            var sketch = newSketch(context, id + "F113", { "sketchPlane" : qUnion([Q0])});
            skLineSegment(sketch, "E212.bottom", {"start": v(-115.12, 4.75) * mm, "end": v(-117.5, 4.75) * mm});
            skLineSegment(sketch, "E212.top", {"start": v(-115.12, 26.97) * mm, "end": v(-117.5, 26.97) * mm});
            skLineSegment(sketch, "E212.left", {"start": v(-115.12, 4.75) * mm, "end": v(-115.12, 26.97) * mm});
            skLineSegment(sketch, "E212.right", {"start": v(-117.5, 4.75) * mm, "end": v(-117.5, 26.97) * mm});
            skLineSegment(sketch, "E213.bottom", {"start": v(-55.86, 4.75) * mm, "end": v(-53.48, 4.75) * mm});
            skLineSegment(sketch, "E213.top", {"start": v(-55.86, 26.97) * mm, "end": v(-53.48, 26.97) * mm});
            skLineSegment(sketch, "E213.left", {"start": v(-55.86, 4.75) * mm, "end": v(-55.86, 26.97) * mm});
            skLineSegment(sketch, "E213.right", {"start": v(-53.48, 4.75) * mm, "end": v(-53.48, 26.97) * mm});
            skLineSegment(sketch, "E214.bottom", {"start": v(28.15, 4.75) * mm, "end": v(25.76, 4.75) * mm});
            skLineSegment(sketch, "E214.top", {"start": v(28.15, 26.97) * mm, "end": v(25.76, 26.97) * mm});
            skLineSegment(sketch, "E214.left", {"start": v(28.15, 4.75) * mm, "end": v(28.15, 26.97) * mm});
            skLineSegment(sketch, "E214.right", {"start": v(25.76, 4.75) * mm, "end": v(25.76, 26.97) * mm});
            skLineSegment(sketch, "E215.bottom", {"start": v(85.56, 4.75) * mm, "end": v(87.95, 4.75) * mm});
            skLineSegment(sketch, "E215.top", {"start": v(85.56, 26.97) * mm, "end": v(87.95, 26.97) * mm});
            skLineSegment(sketch, "E215.left", {"start": v(85.56, 4.75) * mm, "end": v(85.56, 26.97) * mm});
            skLineSegment(sketch, "E215.right", {"start": v(87.95, 4.75) * mm, "end": v(87.95, 26.97) * mm});
            skLineSegment(sketch, "E216.bottom", {"start": v(108.34, 4.75) * mm, "end": v(105.96, 4.75) * mm});
            skLineSegment(sketch, "E216.top", {"start": v(108.34, 26.97) * mm, "end": v(105.96, 26.97) * mm});
            skLineSegment(sketch, "E216.left", {"start": v(108.34, 4.75) * mm, "end": v(108.34, 26.97) * mm});
            skLineSegment(sketch, "E216.right", {"start": v(105.96, 4.75) * mm, "end": v(105.96, 26.97) * mm});
            skLineSegment(sketch, "E217.bottom", {"start": v(152.4, 4.75) * mm, "end": v(150.02, 4.75) * mm});
            skLineSegment(sketch, "E217.top", {"start": v(152.4, 26.97) * mm, "end": v(150.02, 26.97) * mm});
            skLineSegment(sketch, "E217.left", {"start": v(152.4, 4.75) * mm, "end": v(152.4, 26.97) * mm});
            skLineSegment(sketch, "E217.right", {"start": v(150.02, 4.75) * mm, "end": v(150.02, 26.97) * mm});
            skSolve(sketch);
        }
        {
            var Q0;
            Q0=qSketchRegion(id+"F113",true);
            extrude(context, id + "F114", {"entities" : qUnion([Q0]), "operationType" : NewBodyOperationType.ADD, "depth" : 1.6 * mm, "offsetDistance" : 25.4 * mm});
        }
        {
            var Q0;
            Q0=makeQuery(id+"F104.opExtrude","SWEPT_FACE",FACE,{"disambiguationData":[OSD([sQuery(id+"F103.wireOp",EDGE,"E189.bottom")])]});
            var sketch = newSketch(context, id + "F115", { "sketchPlane" : qUnion([Q0])});
            skLineSegment(sketch, "E218.bottom", {"start": v(-53.48, 4.75) * mm, "end": v(25.75, 4.75) * mm});
            skLineSegment(sketch, "E218.top", {"start": v(-53.48, 50.79) * mm, "end": v(25.75, 50.79) * mm});
            skLineSegment(sketch, "E218.left", {"start": v(-53.48, 4.75) * mm, "end": v(-53.48, 50.79) * mm});
            skLineSegment(sketch, "E218.right", {"start": v(25.75, 4.75) * mm, "end": v(25.75, 50.79) * mm});
            skLineSegment(sketch, "E219.bottom", {"start": v(87.94, 4.75) * mm, "end": v(105.95, 4.75) * mm});
            skLineSegment(sketch, "E219.top", {"start": v(87.94, 50.79) * mm, "end": v(105.95, 50.79) * mm});
            skLineSegment(sketch, "E219.left", {"start": v(87.94, 4.75) * mm, "end": v(87.94, 50.79) * mm});
            skLineSegment(sketch, "E219.right", {"start": v(105.95, 4.75) * mm, "end": v(105.95, 50.79) * mm});
            skLineSegment(sketch, "E220.bottom", {"start": v(-117.5, 4.75) * mm, "end": v(-152.4, 4.75) * mm});
            skLineSegment(sketch, "E220.top", {"start": v(-117.5, 50.79) * mm, "end": v(-152.4, 50.79) * mm});
            skLineSegment(sketch, "E220.left", {"start": v(-117.5, 4.75) * mm, "end": v(-117.5, 50.79) * mm});
            skLineSegment(sketch, "E220.right", {"start": v(-152.4, 4.75) * mm, "end": v(-152.4, 50.79) * mm});
            skSolve(sketch);
        }
        {
            var Q0;
            Q0=qSketchRegion(id+"F115",true);
            extrude(context, id + "F116", {"entities" : qUnion([Q0]), "operationType" : NewBodyOperationType.ADD, "depth" : 0.79 * mm, "offsetDistance" : 25.4 * mm});
        }
        {
            var Q0;
            Q0=makeQuery(id+"F1.opExtrude","CAP_FACE",FACE,{"disambiguationData":[OSD([sQuery(id+"F0.wireOp",EDGE,"E0.bottom"),sQuery(id+"F0.wireOp",EDGE,"E0.top"),sQuery(id+"F0.wireOp",EDGE,"E0.left"),sQuery(id+"F0.wireOp",EDGE,"E0.right")])],"isStart":true});
            extrude(context, id + "F117", {"entities" : qUnion([Q0]), "operationType" : NewBodyOperationType.ADD, "depth" : 1.59 * mm, "offsetDistance" : 25.4 * mm});
        }
        {
            var Q0;
            Q0=makeQuery(id+"F117.opExtrude","CAP_FACE",FACE,{"disambiguationData":[OSD([sQuery(id+"F0.wireOp",EDGE,"E0.bottom"),sQuery(id+"F0.wireOp",EDGE,"E0.top"),sQuery(id+"F0.wireOp",EDGE,"E0.left"),sQuery(id+"F0.wireOp",EDGE,"E0.right")])],"isStart":false});
            chamfer(context, id + "F118", {"entities" : qUnion([Q0]), "width" : 0.76 * mm, "tangentPropagation" : true});
        }
        {
            var Q0;
            Q0=makeQuery(id+"F37.boolean.opBoolean","MERGE",FACE,{"derivedFrom":[makeQuery(id+"F36.boolean.opBoolean","MERGE",FACE,{"derivedFrom":[makeQuery(id+"F1.opExtrude","CAP_FACE",FACE,{"disambiguationData":[OSD([sQuery(id+"F0.wireOp",EDGE,"E0.bottom"),sQuery(id+"F0.wireOp",EDGE,"E0.top"),sQuery(id+"F0.wireOp",EDGE,"E0.left"),sQuery(id+"F0.wireOp",EDGE,"E0.right")])],"isStart":false})],"fromTools":[makeQuery(id+"F36.opExtrude","SWEPT_FACE",FACE,{"disambiguationData":[OSD([sQuery(id+"F26.wireOp",EDGE,"E60.top"),sQuery(id+"F35.wireOp",EDGE,"E78")])]})]})],"fromTools":[makeQuery(id+"F37.opExtrude","SWEPT_FACE",FACE,{"disambiguationData":[OSD([sQuery(id+"F21.wireOp",EDGE,"E56.top"),sQuery(id+"F34.wireOp",EDGE,"E70")])]})]});
            var sketch = newSketch(context, id + "F119", { "sketchPlane" : qUnion([Q0])});
            skLineSegment(sketch, "E221", {"start": v(8.62, 55.6) * mm, "end": v(8.62, -24.7) * mm});
            skPoint(sketch, "E221.endSnap0", {"position": v(8.62, -15.64) * mm});
            skLineSegment(sketch, "E222", {"start": v(8.62, -24.7) * mm, "end": v(42.1, -24.7) * mm});
            skLineSegment(sketch, "E223", {"start": v(42.1, -24.7) * mm, "end": v(42.1, -61.97) * mm});
            skLineSegment(sketch, "E224", {"start": v(8.62, 55.6) * mm, "end": v(-190.31, 56.52) * mm});
            skLineSegment(sketch, "E225", {"start": v(-190.31, 56.52) * mm, "end": v(-190.86, -61.97) * mm});
            skLineSegment(sketch, "E226", {"start": v(-190.86, -61.97) * mm, "end": v(42.1, -61.97) * mm});
            skPoint(sketch, "E227.start.orphan", {"position": v(165.68, -61.97) * mm});
            skSolve(sketch);
        }
        {
            var Q0;
            Q0 = qSketchRegion(id + "F119", true);
            extrude(context, id + "F120", {"entities" : qUnion([Q0]), "operationType" : NewBodyOperationType.REMOVE, "endBound" : BoundingType.SYMMETRIC, "oppositeDirection" : true, "depth" : 50.8 * mm, "offsetDistance" : 25.4 * mm});
        }
        {
            var Q0;
            Q0=makeQuery(id+"F120.boolean.opBoolean","COPY",FACE,{"derivedFrom":makeQuery(id+"F120.opExtrude","SWEPT_FACE",FACE,{"disambiguationData":[OSD([sQuery(id+"F119.wireOp",EDGE,"E223")])]})});
            var sketch = newSketch(context, id + "F121", { "sketchPlane" : qUnion([Q0])});
            skCircle(sketch, "E228", {"center": v(43.62, 0.7) * mm, "radius": 0.95 * mm});
            skSolve(sketch);
        }
        {
            var Q0;
            Q0 = qSketchRegion(id + "F121", true);
            extrude(context, id + "F122", {"entities" : qUnion([Q0]), "operationType" : NewBodyOperationType.REMOVE, "oppositeDirection" : true, "depth" : 3.17 * mm, "offsetDistance" : 25.4 * mm});
        }
        {
            var Q0;
            Q0=makeQuery(id+"F120.boolean.opBoolean","COPY",FACE,{"derivedFrom":makeQuery(id+"F120.opExtrude","SWEPT_FACE",FACE,{"disambiguationData":[OSD([sQuery(id+"F119.wireOp",EDGE,"E221")])]})});
            var sketch = newSketch(context, id + "F123", { "sketchPlane" : qUnion([Q0])});
            skCircle(sketch, "E229", {"center": v(19.62, 0.7) * mm, "radius": 0.95 * mm});
            skCircle(sketch, "E230", {"center": v(-43.62, 0.7) * mm, "radius": 0.95 * mm});
            skSolve(sketch);
        }
        {
            var Q0;
            Q0 = qSketchRegion(id + "F123", true);
            extrude(context, id + "F124", {"entities" : qUnion([Q0]), "operationType" : NewBodyOperationType.REMOVE, "oppositeDirection" : true, "depth" : 3.17 * mm, "offsetDistance" : 25.4 * mm});
        }
        {
            var Q0;
            Q0=makeQuery(id+"F120.boolean.opBoolean","INTERSECT",EDGE,{"derivedFrom":[makeQuery(id+"F117.opExtrude","CAP_FACE",FACE,{"disambiguationData":[OSD([sQuery(id+"F0.wireOp",EDGE,"E0.bottom"),sQuery(id+"F0.wireOp",EDGE,"E0.top"),sQuery(id+"F0.wireOp",EDGE,"E0.left"),sQuery(id+"F0.wireOp",EDGE,"E0.right")])],"isStart":false}),makeQuery(id+"F120.opExtrude","SWEPT_FACE",FACE,{"disambiguationData":[OSD([sQuery(id+"F119.wireOp",EDGE,"E223")])]})]});
            var Q1;
            Q1=makeQuery(id+"F120.boolean.opBoolean","INTERSECT",EDGE,{"derivedFrom":[makeQuery(id+"F117.opExtrude","CAP_FACE",FACE,{"disambiguationData":[OSD([sQuery(id+"F0.wireOp",EDGE,"E0.bottom"),sQuery(id+"F0.wireOp",EDGE,"E0.top"),sQuery(id+"F0.wireOp",EDGE,"E0.left"),sQuery(id+"F0.wireOp",EDGE,"E0.right")])],"isStart":false}),makeQuery(id+"F120.opExtrude","SWEPT_FACE",FACE,{"disambiguationData":[OSD([sQuery(id+"F119.wireOp",EDGE,"E222")])]})]});
            var Q2;
            Q2=makeQuery(id+"F120.boolean.opBoolean","INTERSECT",EDGE,{"derivedFrom":[makeQuery(id+"F117.opExtrude","CAP_FACE",FACE,{"disambiguationData":[OSD([sQuery(id+"F0.wireOp",EDGE,"E0.bottom"),sQuery(id+"F0.wireOp",EDGE,"E0.top"),sQuery(id+"F0.wireOp",EDGE,"E0.left"),sQuery(id+"F0.wireOp",EDGE,"E0.right")])],"isStart":false}),makeQuery(id+"F120.opExtrude","SWEPT_FACE",FACE,{"disambiguationData":[OSD([sQuery(id+"F119.wireOp",EDGE,"E221")])]})]});
            chamfer(context, id + "F125", {"entities" : qUnion([Q0, Q1, Q2]), "width" : 0.76 * mm, "tangentPropagation" : true});
        }
    });
